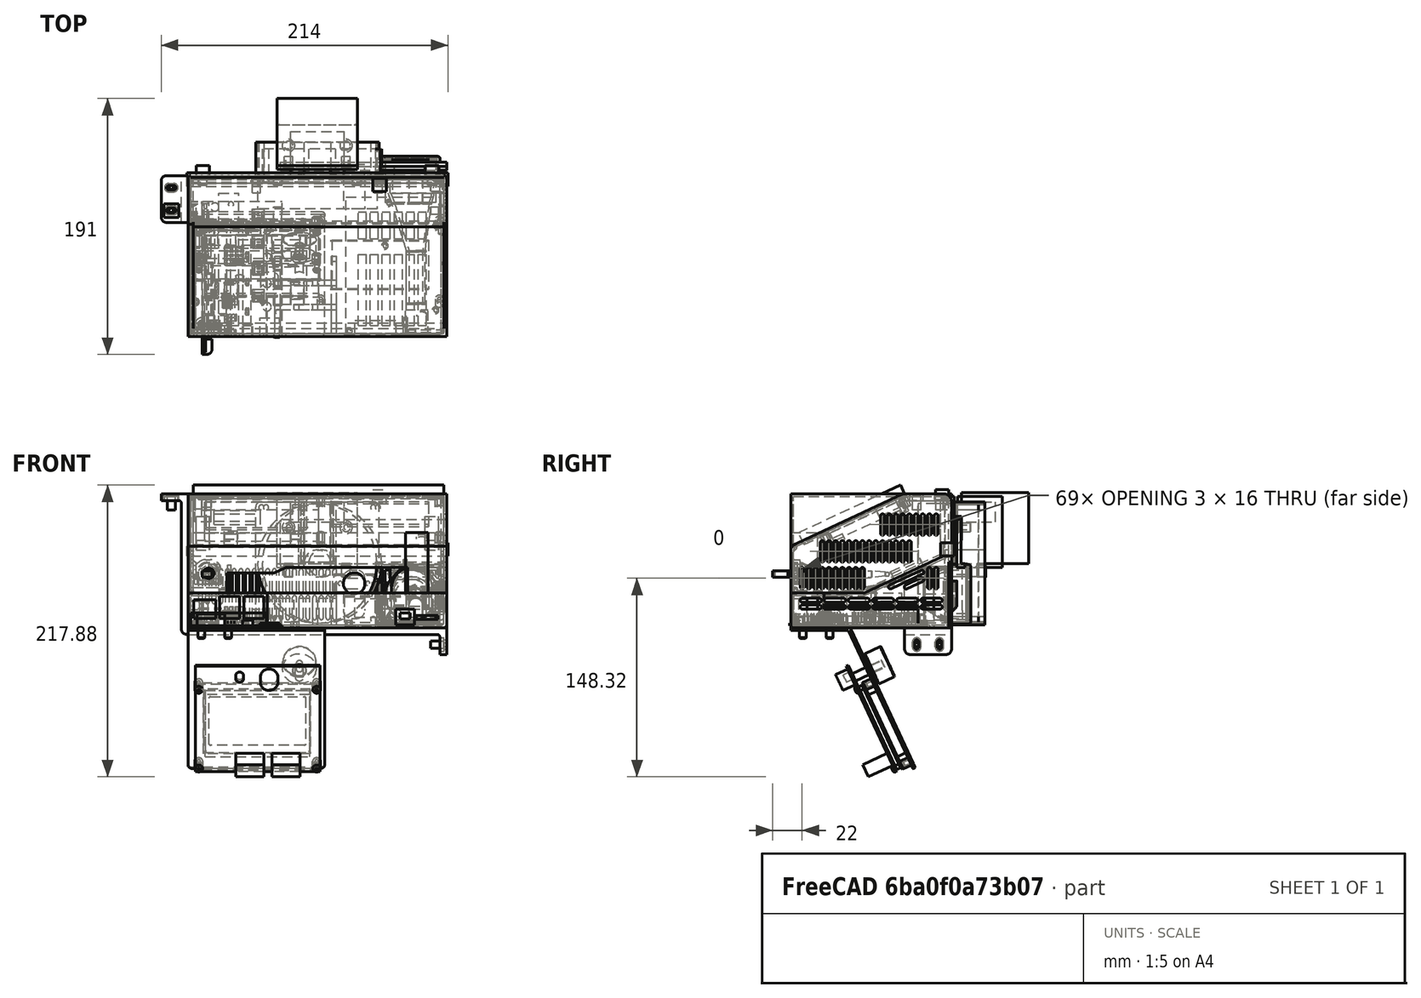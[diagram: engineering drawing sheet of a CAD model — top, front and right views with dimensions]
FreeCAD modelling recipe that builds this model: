
FCSTD DOCUMENT  (FreeCAD 0.19R24291 (Git))
Label: Ender 3 All in One Control Box
License: All rights reserved
LicenseURL: http://en.wikipedia.org/wiki/All_rights_reserved
objects: Part::Box×238, Part::Feature×143, Part::FeaturePython×143, Part::Fillet×105, Part::Cylinder×67, Part::Chamfer×64, Part::MultiFuse×60, Part::Cut×39, App::DocumentObjectGroup×21, Part::Loft×8, App::Part×4, Mesh::Feature×1, Part::Compound×1
note: 868 computed .brp shape members not serialized (recipe doc carries the construction recipe); baked Part::Feature solids carry a one-line shape summary decoded from their .brp

FEATURE [Part::Feature] Raspberry_Pi_3_B__Template001
  Placement = pos=(5.86,26.01,3) rot=(0,0,-1;1.5708rad)
  shape: bbox 58.5 x 89.15 x 20 mm, 4954 faces, 0 solids (baked)
FEATURE [Part::Feature] Part__Feature711  label="M3X8 Pan Head Screw_Standard002"
  Placement = pos=(8.05,48.2452,-46.9667) rot=(0.706961,0.647366,0.284821;3.1725rad)
  shape: bbox 7.142 x 14.51 x 10.14 mm, 23 faces (baked)
FEATURE [Part::Feature] Part__Feature712  label="M3X8 Pan Head Screw_Standard003"
  Placement = pos=(95.95,48.2452,-46.9667) rot=(0.703312,0.680906,0.204256;3.34615rad)
  shape: bbox 6.803 x 14.4 x 9.902 mm, 23 faces (baked)
FEATURE [Part::Feature] Part__Feature706  label="lcd Knob_Standard"
  Placement = pos=(83.1,60.6587,-30.6409) rot=(0.306507,-0.929305,-0.206022;1.25238rad)
  shape: bbox 25 x 22.14 x 27.94 mm, 13 faces (baked)
FEATURE [Part::Feature] Part__Feature707  label="M5X8Pan Head Screw004"
  Placement = pos=(10,9,2.75) rot=(-0.69142,-0.20947,0.69142;3.55456rad)
  shape: bbox 9.985 x 9.723 x 11.27 mm, 24 faces (baked)
FEATURE [Part::Feature] Part__Feature708  label="M5X8Pan Head Screw005"
  Placement = pos=(30,29,2.75) rot=(-0.685865,-0.243264,0.685865;3.61885rad)
  shape: bbox 9.925 x 9.785 x 11.27 mm, 24 faces (baked)
FEATURE [Part::Feature] Part__Feature709  label="M3X8 Pan Head Screw_Standard"
  Placement = pos=(95.95,75.6731,-105.786) rot=(0.698299,0.566548,0.437496;2.83001rad)
  shape: bbox 8.972 x 14.48 x 10.07 mm, 23 faces (baked)
FEATURE [Part::Feature] Part__Feature710  label="M3X8 Pan Head Screw_Standard001"
  Placement = pos=(8.05,75.6731,-105.786) rot=(0.70527,0.608703,0.36342;2.9976rad)
  shape: bbox 8.119 x 14.54 x 10.2 mm, 23 faces (baked)
FEATURE [Part::Feature] Part__Feature703  label="LCD support_Standard"
  Placement = pos=(0,0,0) rot=(0.57735,0.57735,0.57735;2.0944rad)
  shape: bbox 102 x 92.88 x 105.4 mm, 47 faces (baked)
FEATURE [Part::Feature] Part__Feature704  label="lcd_Standard"
  Placement = pos=(52,59.8623,-67.9755) rot=(-1,0,0;1.13446rad)
  shape: bbox 93 x 46.13 x 87.2 mm, 33 faces (baked)
FEATURE [Part::Feature] Part__Feature705  label="lcd_Standard001"
  Placement = pos=(52,59.8623,-67.9755) rot=(-1,0,0;1.13446rad)
  shape: bbox 93 x 34.72 x 64.08 mm, 32 faces (baked)
FEATURE [App::Part] lcd_Standard  label="lcd_Standard002"
  Group = -> [Part__Feature704,Part__Feature705]
  Origin = -> Origin078
FEATURE [App::Part] ASM_Display_Standard  label="ASM Display_Standard"
  Group = -> [Part__Feature703,lcd_Standard,Part__Feature706,Part__Feature707,Part__Feature708,Part__Feature709,Part__Feature710,Part__Feature711,Part__Feature712]
  Origin = -> Origin079
  Placement = pos=(125,1,157) rot=(0,0,1;0rad)
FEATURE [App::Part] _1_MAIN_ASM_Ender_3_Pro  label="01 MAIN ASM Ender 3 Pro"
  Group = -> [ASM_Display_Standard]
  Origin = -> Origin084
  Placement = pos=(-33.3,142.528,6.50199) rot=(1,0,0;1.5708rad)
FEATURE [Part::Box] Box005  label="Cube010"
  AttacherType = Attacher::AttachEngine3D
  Height = 9
  Length = 34.5
  Placement = pos=(7,48,0) rot=(0,0,1;0rad)
  Width = 6
FEATURE [Part::Box] Box004  label="Cube009"
  AttacherType = Attacher::AttachEngine3D
  Height = 6.5
  Length = 85
  Placement = pos=(0,0,9) rot=(0,0,1;0rad)
  Width = 55
FEATURE [Part::MultiFuse] Fusion001  label="Touchscreen"
  Placement = pos=(12.6,36,56.64) rot=(1,0,0;0.436332rad)
  Shapes = -> [Box004,Box005]
FEATURE [Part::Feature] Face034  label="Face005"
  Placement = pos=(0,55,26) rot=(1,0,0;0.436332rad)
  shape: bbox 210 x 125.1 x 58.32 mm, 1 faces, 0 solids (baked)
FEATURE [Part::Feature] Face033  label="Face004"
  Placement = pos=(0,-24,26) rot=(0,0,1;0rad)
  shape: bbox 210 x 138 x 2e-07 mm, 1 faces, 0 solids (baked)
FEATURE [Part::Feature] Face027  label="Face"
  Placement = pos=(5,-23,48.27) rot=(-1,0,0;1.13446rad)
  shape: bbox 216.4 x 183.1 x 85.37 mm, 1 faces, 0 solids (baked)
FEATURE [Part::Feature] Face032  label="Face003"
  Placement = pos=(0,-24,26) rot=(0,0,1;0rad)
  shape: bbox 210 x 2e-07 x 95 mm, 1 faces, 0 solids (baked)
FEATURE [Part::Box] Box  label="Cube"
  AttacherType = Attacher::AttachEngine3D
  Height = 100
  Length = 193
  Width = 120
FEATURE [Part::Cylinder] Cylinder
  Angle = 360
  AttacherType = Attacher::AttachEngine3D
  Height = 9.2
  Radius = 3
FEATURE [Part::Cylinder] Cylinder001
  Angle = 360
  AttacherType = Attacher::AttachEngine3D
  Height = 9.2
  Radius = 1.35
FEATURE [Part::Cut] Cut
  Base = -> Cylinder
  Placement = pos=(99.8,78.1,115.82) rot=(0,0,1;0rad)
  Tool = -> Cylinder001
FEATURE [Part::Feature] Cut001002005
  Placement = pos=(185.75,20.5,0) rot=(0,0,1;0rad)
  shape: bbox 5 x 5 x 4.2 mm, 4 faces (baked)
FEATURE [Part::Feature] Cut001002006
  Placement = pos=(185.75,82.85,0) rot=(0,0,1;0rad)
  shape: bbox 5 x 5 x 4.2 mm, 4 faces (baked)
FEATURE [Part::Feature] Cut001002007
  Placement = pos=(147.9,68.58,0) rot=(0,0,1;0rad)
  shape: bbox 5 x 5 x 4.2 mm, 4 faces (baked)
FEATURE [Part::Feature] Cut001002008
  Placement = pos=(150.5,100.5,0) rot=(0,0,1;0rad)
  shape: bbox 5 x 5 x 4.2 mm, 4 faces (baked)
FEATURE [Part::Cylinder] Cylinder015
  Angle = 360
  AttacherType = Attacher::AttachEngine3D
  Height = 4.2
  Radius = 2.5
FEATURE [Part::Feature] Cut001002004
  Placement = pos=(121.1,4.85,0) rot=(0,0,1;0rad)
  shape: bbox 5 x 5 x 4.2 mm, 4 faces (baked)
FEATURE [Part::Cylinder] Cylinder014
  Angle = 360
  AttacherType = Attacher::AttachEngine3D
  Height = 4.2
  Radius = 1.3
FEATURE [Part::Cut] Cut001002  label="Cut001003"
  Base = -> Cylinder015
  Placement = pos=(6,25.73,0) rot=(0,0,1;0rad)
  Tool = -> Cylinder014
FEATURE [Part::MultiFuse] Fusion002  label="SKR Mini E3 Screw Holes"
  Placement = pos=(-1,-1,1) rot=(0,0,1;0rad)
  Shapes = -> [Cut001002005,Cut001002006,Cut001002007,Cut001002008,Cut001002004]
FEATURE [Part::Cylinder] Cylinder018
  Angle = 360
  AttacherType = Attacher::AttachEngine3D
  Height = 3
  Placement = pos=(150.25,131.4,8) rot=(-1,0,0;1.5708rad)
  Radius = 1.3
FEATURE [Part::Cylinder] Cylinder019
  Angle = 360
  AttacherType = Attacher::AttachEngine3D
  Height = 3
  Placement = pos=(181.75,131.4,9) rot=(-1,0,0;1.5708rad)
  Radius = 1.3
FEATURE [Part::Cylinder] Cylinder020
  Angle = 360
  AttacherType = Attacher::AttachEngine3D
  Height = 3
  Placement = pos=(181.75,131.4,40.5) rot=(-1,0,0;1.5708rad)
  Radius = 1.3
FEATURE [Part::Cylinder] Cylinder021
  Angle = 360
  AttacherType = Attacher::AttachEngine3D
  Height = 3
  Placement = pos=(150.25,131.4,40.5) rot=(-1,0,0;1.5708rad)
  Radius = 1.3
FEATURE [Part::MultiFuse] Fusion004008003  label="Fan Screw Holes"
  Placement = pos=(0.2,0,-0.2) rot=(0,0,1;0rad)
  Shapes = -> [Cylinder018,Cylinder019,Cylinder020,Cylinder021]
FEATURE [Part::Cylinder] Cylinder017  label="Fan Hole"
  Angle = 360
  AttacherType = Attacher::AttachEngine3D
  Height = 25
  Placement = pos=(96.5,120,48) rot=(1,0,0;1.5708rad)
  Radius = 44.5
FEATURE [Part::Box] Box014  label="USB 1"
  AttacherType = Attacher::AttachEngine3D
  Height = 16.7
  Length = 15
  Placement = pos=(23.6,-2,6.788) rot=(0,0,1;0rad)
  Width = 10
FEATURE [Part::Box] Box015  label="USB 2"
  AttacherType = Attacher::AttachEngine3D
  Height = 16.7
  Length = 15
  Placement = pos=(41.7,-2,6.788) rot=(0,0,1;0rad)
  Width = 10
FEATURE [Part::Cylinder] Cylinder010  label="Cable Bundle Hole"
  Angle = 360
  AttacherType = Attacher::AttachEngine3D
  Height = 25
  Placement = pos=(124,120,33) rot=(1,0,0;1.5708rad)
  Radius = 8
FEATURE [Part::Box] Box010  label="MicroSD Slot"
  AttacherType = Attacher::AttachEngine3D
  Height = 2.8
  Length = 16.06
  Placement = pos=(170.4,-2,6.4) rot=(0,0,1;0rad)
  Width = 10
FEATURE [Part::Box] Box011  label="Cube016"
  AttacherType = Attacher::AttachEngine3D
  Height = 4
  Length = 10
  Placement = pos=(-2,72.75,4.94) rot=(0,0,1;0rad)
  Width = 8
FEATURE [Part::Box] Box012  label="Cube017"
  AttacherType = Attacher::AttachEngine3D
  Height = 6
  Length = 10
  Placement = pos=(-2,47.5,6) rot=(0,0,1;0rad)
  Width = 16
FEATURE [Part::Chamfer] Chamfer005  label="HDMI Port"
  Base = -> Box012
  Edges = 2 edges r=2: [Edge9,Edge11]
  Placement = pos=(0,0,1) rot=(0,0,1;0rad)
FEATURE [Part::Cylinder] Cylinder005  label="Headphone Jack"
  Angle = 360
  AttacherType = Attacher::AttachEngine3D
  Height = 10
  Placement = pos=(-1,33.75,9.498) rot=(0,1,0;1.5708rad)
  Radius = 3.75
FEATURE [Part::Box] Box013  label="Ethernet"
  AttacherType = Attacher::AttachEngine3D
  Height = 14
  Length = 16.4
  Placement = pos=(4.3,-2,6.998) rot=(0,0,1;0rad)
  Width = 10
FEATURE [Part::Box] Box007  label="Cube012"
  AttacherType = Attacher::AttachEngine3D
  Height = 6.5
  Length = 74.75
  Placement = pos=(0,-0.5,9) rot=(0,0,1;0rad)
  Width = 50
FEATURE [Part::Box] Box008  label="Cube013"
  AttacherType = Attacher::AttachEngine3D
  Height = 9
  Length = 34.5
  Placement = pos=(7.5,48,0) rot=(0,0,1;0rad)
  Width = 6
FEATURE [Part::MultiFuse] Fusion004008002002  label="Touchscreen Hole"
  Placement = pos=(13.5,36,62.7) rot=(1,0,0;0.436332rad)
  Shapes = -> [Box007,Box008]
FEATURE [Part::Box] Box009  label="Cube248"
  AttacherType = Attacher::AttachEngine3D
  Height = 20
  Length = 71
  Placement = pos=(117,1,4) rot=(0,0,1;0rad)
  Width = 1
FEATURE [Part::Box] Box029  label="Cube034"
  AttacherType = Attacher::AttachEngine3D
  Height = 16
  Length = 2
  Placement = pos=(0,12,29) rot=(0,0,1;0rad)
  Width = 3
FEATURE [Part::Fillet] Fillet005011
  Base = -> Box029
  Edges = 4 edges r=1.49: [Edge9,Edge10,Edge11,Edge12]
FEATURE [Part::Cylinder] Cylinder016
  Angle = 360
  AttacherType = Attacher::AttachEngine3D
  Height = 25
  Placement = pos=(100,140,48) rot=(1,0,0;1.5708rad)
  Radius = 44.5
FEATURE [Part::Box] Box002  label="Cube007"
  AttacherType = Attacher::AttachEngine3D
  Height = 92
  Length = 92
  Placement = pos=(54,115,2) rot=(0,0,1;0rad)
  Width = 25
FEATURE [Part::Fillet] Fillet
  Base = -> Box002
  Edges = 4 edges r=4: [Edge2,Edge4,Edge6,Edge8]
FEATURE [Part::Cylinder] Cylinder022
  Angle = 360
  AttacherType = Attacher::AttachEngine3D
  Height = 25
  Placement = pos=(58.25,140,6.25) rot=(1,0,0;1.5708rad)
  Radius = 2
FEATURE [Part::Cylinder] Cylinder023
  Angle = 360
  AttacherType = Attacher::AttachEngine3D
  Height = 25
  Placement = pos=(141.75,140,6.25) rot=(1,0,0;1.5708rad)
  Radius = 2
FEATURE [Part::Cylinder] Cylinder002
  Angle = 360
  AttacherType = Attacher::AttachEngine3D
  Height = 25
  Placement = pos=(141.75,140,89.75) rot=(1,0,0;1.5708rad)
  Radius = 2
FEATURE [Part::Cylinder] Cylinder003
  Angle = 360
  AttacherType = Attacher::AttachEngine3D
  Height = 25
  Placement = pos=(58.25,140,89.75) rot=(1,0,0;1.5708rad)
  Radius = 2
FEATURE [Part::Cylinder] Cylinder004
  Angle = 360
  AttacherType = Attacher::AttachEngine3D
  Height = 25
  Placement = pos=(100,140,48) rot=(1,0,0;1.5708rad)
  Radius = 10
FEATURE [Part::FeaturePython] Slice  # WARN: FeaturePython — macro-defined, semantics opaque (R4)
  Base = -> Fillet
  Mode = 1
  Tolerance = 0
  Tools = -> [Cylinder016,Cylinder022,Cylinder023,Cylinder002,Cylinder003,Cylinder004]
FEATURE [Part::FeaturePython] Slice_child6  label="Slice.6"  # WARN: FeaturePython — macro-defined, semantics opaque (R4)
  Base = -> Slice
  FilterType = 1
  Invert = false
  OverrideMaxVal = 0
  WindowFrom = 80
  WindowTo = 100
  items = 6
FEATURE [Part::FeaturePython] Slice_child0  label="Slice.0"  # WARN: FeaturePython — macro-defined, semantics opaque (R4)
  Base = -> Slice
  FilterType = 1
  Invert = false
  OverrideMaxVal = 0
  WindowFrom = 80
  WindowTo = 100
  items = 0
FEATURE [Part::MultiFuse] Fusion004008002002002001007002  label="92mm Fan"
  Placement = pos=(-3.5,5,0) rot=(0,0,1;0rad)
  Shapes = -> [Slice_child6,Slice_child0]
FEATURE [Part::Chamfer] Chamfer  label="Micro USB Port"
  Base = -> Box011
  Edges = 2 edges r=1: [Edge9,Edge11]
  Placement = pos=(0,0,1) rot=(0,0,1;0rad)
FEATURE [Part::Box] Box030  label="Cube035"
  AttacherType = Attacher::AttachEngine3D
  Height = 96
  Length = 189
  Placement = pos=(2,2,2) rot=(0,0,1;0rad)
  Width = 116
FEATURE [Part::Feature] Face081
  Placement = pos=(5,-23,50.27) rot=(-1,0,0;1.13446rad)
  shape: bbox 216.4 x 183.1 x 85.37 mm, 1 faces, 0 solids (baked)
FEATURE [Part::Box] Box068  label="Cube073"
  AttacherType = Attacher::AttachEngine3D
  Height = 12.2
  Length = 10
  Placement = pos=(6,-5,0) rot=(0,0,1;0rad)
  Width = 14
FEATURE [Part::Box] Box067  label="Cube072"
  AttacherType = Attacher::AttachEngine3D
  Height = 9.3
  Length = 86
  Placement = pos=(0,0,4.5) rot=(0,0,1;0rad)
  Width = 56
FEATURE [Part::Cut] Cut001002016
  Base = -> Box068
  Placement = pos=(10,0.25,1) rot=(0,0,1;0rad)
  Tool = -> Box067
FEATURE [Part::Box] Box073  label="Ender LCD Hole"
  AttacherType = Attacher::AttachEngine3D
  Height = 10
  Length = 72
  Placement = pos=(107.5,38.85,68.9) rot=(1,0,0;0.436332rad)
  Width = 40
FEATURE [Part::Cylinder] Cylinder024  label="LCD Control Knob Hole"
  Angle = 360
  AttacherType = Attacher::AttachEngine3D
  Height = 10
  Placement = pos=(174.5,17.75,61.25) rot=(1,0,0;0.436332rad)
  Radius = 4
FEATURE [Part::Box] Box074  label="Cube078"
  AttacherType = Attacher::AttachEngine3D
  Height = 4
  Length = 2
  Placement = pos=(2,4,24) rot=(0,0,1;0rad)
  Width = 51
FEATURE [Part::Box] Box075  label="Cube079"
  AttacherType = Attacher::AttachEngine3D
  Height = 4
  Length = 2
  Placement = pos=(189,4,24) rot=(0,0,1;0rad)
  Width = 51
FEATURE [Part::Box] Box076  label="Cube080"
  AttacherType = Attacher::AttachEngine3D
  Height = 4
  Length = 2
  Placement = pos=(2,55,24) rot=(1,0,0;0.436332rad)
  Width = 67.25
FEATURE [Part::Box] Box077  label="Cube081"
  AttacherType = Attacher::AttachEngine3D
  Height = 4
  Length = 2
  Placement = pos=(189,55,24) rot=(1,0,0;0.436332rad)
  Width = 67.25
FEATURE [Part::Box] Box078  label="Cube082"
  AttacherType = Attacher::AttachEngine3D
  Height = 43.5
  Length = 2
  Placement = pos=(2,112,52.5) rot=(0,0,1;0rad)
  Width = 6
FEATURE [Part::Box] Box079  label="Cube083"
  AttacherType = Attacher::AttachEngine3D
  Height = 43.5
  Length = 2
  Placement = pos=(189,112,52.5) rot=(0,0,1;0rad)
  Width = 6
FEATURE [Part::Box] Box081  label="Cube085"
  AttacherType = Attacher::AttachEngine3D
  Height = 6
  Length = 28.75
  Placement = pos=(162.25,2,24) rot=(0,0,1;0rad)
  Width = 3
FEATURE [Part::Fillet] Fillet005011013
  Base = -> Box081
  Edges = 1 edges r=1.999: [Edge5]
FEATURE [Part::Chamfer] Chamfer006
  Base = -> Box075
  Edges = 1 edges r=1.99: [Edge4]
FEATURE [Part::Chamfer] Chamfer007
  Base = -> Box077
  Edges = 1 edges r=1.99: [Edge4]
FEATURE [Part::Chamfer] Chamfer008
  Base = -> Box074
  Edges = 1 edges r=1.99: [Edge8]
FEATURE [Part::Chamfer] Chamfer009
  Base = -> Box076
  Edges = 1 edges r=1.99: [Edge8]
FEATURE [Part::Box] Box083  label="Cube087"
  AttacherType = Attacher::AttachEngine3D
  Height = 14
  Length = 31
  Placement = pos=(124.5,2,7.8) rot=(0,0,1;0rad)
  Width = 10
FEATURE [Part::Box] Box085004  label="Screen Slicin' Cube"
  AttacherType = Attacher::AttachEngine3D
  Height = 10
  Length = 187
  Placement = pos=(4,10,62) rot=(1,0,0;0.436332rad)
  Width = 84
FEATURE [Part::Cylinder] Cylinder025
  Angle = 360
  AttacherType = Attacher::AttachEngine3D
  Height = 72.5
  Radius = 2.4
FEATURE [Part::Chamfer] Chamfer011002
  Base = -> Cylinder025
  Edges = 1 edges: [Edge1 r1=10 r2=1]
FEATURE [Part::Cylinder] Cylinder026
  Angle = 360
  AttacherType = Attacher::AttachEngine3D
  Height = 3
  Placement = pos=(0,0,72.5) rot=(0,0,1;0rad)
  Radius = 1.4
FEATURE [Part::Fillet] Fillet005011017004
  Base = -> Cylinder026
  Edges = 1 edges r=1: [Edge1]
FEATURE [Part::Box] Box085008  label="Cube096"
  AttacherType = Attacher::AttachEngine3D
  Height = 11.5
  Length = 7.4
  Placement = pos=(-2.4,-2.4,-11.5) rot=(0,0,1;0rad)
  Width = 4.8
FEATURE [Part::Fillet] Fillet005011017005
  Base = -> Box085008
  Edges = 2 edges r=1: [Edge1,Edge3]
FEATURE [Part::Fillet] Fillet005011017006
  Base = -> Fillet005011017005
  Edges = 1 edges r=4: [Edge15]
FEATURE [Part::Box] Box085009  label="Cube097"
  AttacherType = Attacher::AttachEngine3D
  Height = 10
  Length = 1
  Placement = pos=(-1,-2.4,-10) rot=(0,0,1;0rad)
  Width = 4.8
FEATURE [Part::Cut] Cut001002016002
  Base = -> Fillet005011017006
  Tool = -> Box085009
FEATURE [Part::MultiFuse] Fusion004008002002002001007002002008  label="Stylus"
  Placement = pos=(13,-2,40) rot=(-1,0,0;1.5708rad)
  Shapes = -> [Chamfer011002,Fillet005011017004,Cut001002016002]
FEATURE [Part::Feature] Part__Feature713  label="X_Stepper_Connector001"
  Placement = pos=(64,84.3,1.6) rot=(0,0,1;0rad)
  shape: bbox 5.8 x 12.45 x 7.1 mm, 6 faces (baked)
FEATURE [Part::Feature] Part__Feature714  label="Y_Stepper_Connector001"
  Placement = pos=(64,63.45,1.6) rot=(0,0,1;0rad)
  shape: bbox 5.8 x 12.45 x 7.1 mm, 6 faces (baked)
FEATURE [Part::Feature] Part__Feature715  label="ZA_Stepper_Connector001"
  Placement = pos=(64,50,1.6) rot=(0,0,1;0rad)
  shape: bbox 5.8 x 12.45 x 7.1 mm, 6 faces (baked)
FEATURE [Part::Feature] Part__Feature716  label="ZB_Stepper_Connector001"
  Placement = pos=(64,36.55,1.6) rot=(0,0,1;0rad)
  shape: bbox 5.8 x 12.45 x 7.1 mm, 6 faces (baked)
FEATURE [Part::Feature] Part__Feature717  label="E_Stepper_Connector001"
  Placement = pos=(64,23.1,1.6) rot=(0,0,1;0rad)
  shape: bbox 5.8 x 12.45 x 7.1 mm, 6 faces (baked)
FEATURE [Part::Feature] Part__Feature718  label="Capacitor005"
  shape: bbox 6.711 x 6.711 x 7.9 mm, 4 faces (baked)
FEATURE [Part::Feature] Part__Feature719  label="Capacitor006"
  Placement = pos=(0,17.5,0) rot=(0,0,1;0rad)
  shape: bbox 6.711 x 6.711 x 7.9 mm, 4 faces (baked)
FEATURE [Part::Feature] Part__Feature720  label="Capacitor007"
  Placement = pos=(0,37,0) rot=(0,0,1;0rad)
  shape: bbox 6.711 x 6.711 x 7.9 mm, 4 faces (baked)
FEATURE [Part::Feature] Part__Feature721  label="Capacitor008"
  Placement = pos=(0,57.5,0) rot=(0,0,1;0rad)
  shape: bbox 6.711 x 6.711 x 7.9 mm, 4 faces (baked)
FEATURE [Part::Feature] Part__Feature722  label="Capacitor009"
  Placement = pos=(-39,74.5,0) rot=(0,0,1;0rad)
  shape: bbox 6.711 x 6.711 x 7.9 mm, 4 faces (baked)
FEATURE [Part::Feature] Part__Feature723  label="Board001"
  shape: bbox 70.25 x 100.8 x 1.6 mm, 11 faces (baked)
FEATURE [Part::Feature] Part__Feature724  label="X_Stepper_Driver001"
  Placement = pos=(50,88,1.6) rot=(0,0,1;0rad)
  shape: bbox 5 x 5 x 0.9 mm, 6 faces (baked)
FEATURE [Part::Feature] Part__Feature725  label="Y_Stepper_Driver001"
  Placement = pos=(50,67.5,1.6) rot=(0,0,1;0rad)
  shape: bbox 5 x 5 x 0.9 mm, 6 faces (baked)
FEATURE [Part::Feature] Part__Feature726  label="Z_Stepper_Driver001"
  Placement = pos=(50,47,1.6) rot=(0,0,1;0rad)
  shape: bbox 5 x 5 x 0.9 mm, 6 faces (baked)
FEATURE [Part::Feature] Part__Feature727  label="E_Stepper_Driver001"
  Placement = pos=(50,28,1.6) rot=(0,0,1;0rad)
  shape: bbox 5 x 5 x 0.9 mm, 6 faces (baked)
FEATURE [Part::Feature] Part__Feature728  label="Tall_Terminal003"
  Placement = pos=(-90.35,100.75,0) rot=(0,0,-1;1.5708rad)
  shape: bbox 10.4 x 10.6 x 18.4 mm, 17 faces (baked)
FEATURE [Part::Feature] Part__Feature729  label="Tall_Terminal004"
  Placement = pos=(0,-23.3,0) rot=(0,0,1;0rad)
  shape: bbox 10.6 x 10.4 x 18.4 mm, 17 faces (baked)
FEATURE [Part::Feature] Part__Feature730  label="Tall_Terminal005"
  Placement = pos=(0,-12.6,0) rot=(0,0,1;0rad)
  shape: bbox 10.6 x 10.4 x 18.4 mm, 17 faces (baked)
FEATURE [Part::Feature] Part__Feature731  label="Short_Terminal001"
  Placement = pos=(1.6,0,0) rot=(0,0,1;0rad)
  shape: bbox 7.5 x 9.9 x 10.55 mm, 12 faces (baked)
FEATURE [Part::Feature] Part__Feature732  label="Fan0_Terminal001"
  Placement = pos=(0,47.5,1.6) rot=(0,0,1;0rad)
  shape: bbox 5.8 x 7.5 x 7.2 mm, 6 faces (baked)
FEATURE [Part::Feature] Part__Feature733  label="X-Stop001"
  Placement = pos=(0,39,1.6) rot=(0,0,1;0rad)
  shape: bbox 5.8 x 7.5 x 7.2 mm, 6 faces (baked)
FEATURE [Part::Feature] Part__Feature734  label="Y-Stop001"
  Placement = pos=(0,30.5,1.6) rot=(0,0,1;0rad)
  shape: bbox 5.8 x 7.5 x 7.2 mm, 6 faces (baked)
FEATURE [Part::Feature] Part__Feature735  label="Z-Stop001"
  Placement = pos=(0,22,1.6) rot=(0,0,1;0rad)
  shape: bbox 5.8 x 7.5 x 7.2 mm, 6 faces (baked)
FEATURE [Part::Feature] Part__Feature736  label="THB001"
  Placement = pos=(0,13.5,1.6) rot=(0,0,1;0rad)
  shape: bbox 5.8 x 7.5 x 7.2 mm, 6 faces (baked)
FEATURE [Part::Feature] Part__Feature737  label="TH001"
  Placement = pos=(0,5,1.6) rot=(0,0,1;0rad)
  shape: bbox 5.8 x 7.5 x 7.2 mm, 6 faces (baked)
FEATURE [Part::Feature] Part__Feature738  label="Fan1_Terminal001"
  Placement = pos=(12.55,47.5,1.6) rot=(0,0,1;0rad)
  shape: bbox 5.8 x 7.5 x 7.2 mm, 6 faces (baked)
FEATURE [Part::Feature] Part__Feature739  label="PS-ON001"
  Placement = pos=(12.55,39,1.6) rot=(0,0,1;0rad)
  shape: bbox 5.8 x 7.5 x 7.2 mm, 6 faces (baked)
FEATURE [Part::Feature] Part__Feature740  label="PWR-DET001"
  Placement = pos=(12.55,28,1.6) rot=(0,0,1;0rad)
  shape: bbox 5.8 x 10 x 7.2 mm, 6 faces (baked)
FEATURE [Part::Feature] Part__Feature741  label="E0-STOP001"
  Placement = pos=(12.55,17,1.6) rot=(0,0,1;0rad)
  shape: bbox 5.8 x 10 x 7.2 mm, 6 faces (baked)
FEATURE [Part::Feature] Part__Feature742  label="Neopixel001"
  Placement = pos=(22.85,17,1.6) rot=(0,0,1;0rad)
  shape: bbox 5.8 x 10 x 7.2 mm, 6 faces (baked)
FEATURE [Part::Feature] Part__Feature743  label="Z-Probe001"
  Placement = pos=(12.55,10,1.6) rot=(0,0,1;0rad)
  shape: bbox 15 x 5.75 x 7.2 mm, 6 faces (baked)
FEATURE [Part::Feature] Part__Feature744  label="EXP002"
  Placement = pos=(6.8,0,1.6) rot=(0,0,1;0rad)
  shape: bbox 20.45 x 8.9 x 8.9 mm, 6 faces (baked)
FEATURE [Part::Feature] Part__Feature745  label="CPU001"
  Placement = pos=(28,39.5,1.6) rot=(0,0,1;0rad)
  shape: bbox 10 x 10 x 2 mm, 6 faces (baked)
FEATURE [Part::Feature] Part__Feature746  label="Q004"
  Placement = pos=(12.2,69.15,1.6) rot=(0,0,1;0rad)
  shape: bbox 10 x 10 x 6.4 mm, 6 faces (baked)
FEATURE [Part::Feature] Part__Feature747  label="Q005"
  Placement = pos=(11,59.65,1.6) rot=(0,0,1;0rad)
  shape: bbox 6.2 x 6.2 x 2.4 mm, 6 faces (baked)
FEATURE [Part::Feature] Part__Feature748  label="E_Stepper_Driver_Heatsink001"
  Placement = pos=(48,26,0) rot=(0,0,1;0rad)
  shape: bbox 9 x 9.15 x 12.17 mm, 94 faces (baked)
FEATURE [Part::Feature] Part__Feature749  label="Z_Stepper_Driver_Heatsink002"
  Placement = pos=(48,46,0) rot=(0,0,1;0rad)
  shape: bbox 9 x 9.15 x 12.17 mm, 94 faces (baked)
FEATURE [Part::Feature] Part__Feature750  label="Y_Stepper_Driver_Heatsink003"
  Placement = pos=(48,66,0) rot=(0,0,1;0rad)
  shape: bbox 9 x 9.15 x 12.17 mm, 94 faces (baked)
FEATURE [Part::Feature] Part__Feature751  label="X_Stepper_Driver_Heatsink004"
  Placement = pos=(48,86,0) rot=(0,0,1;0rad)
  shape: bbox 9 x 9.15 x 12.17 mm, 94 faces (baked)
FEATURE [Part::Feature] Part__Feature752  label="SPI002"
  Placement = pos=(0.6,0,0) rot=(0,0,1;0rad)
  shape: bbox 7.5 x 5 x 8.9 mm, 64 faces (baked)
FEATURE [Part::Feature] Part__Feature753  label="E0-DIAG001"
  Placement = pos=(43,16,0) rot=(0,0,1;0rad)
  shape: bbox 2.5 x 5 x 8.9 mm, 24 faces (baked)
FEATURE [Part::Feature] Part__Feature754  label="Z-DIAG001"
  Placement = pos=(43,38,0) rot=(0,0,1;0rad)
  shape: bbox 2.5 x 5 x 8.9 mm, 24 faces (baked)
FEATURE [Part::Feature] Part__Feature755  label="Y-DIAG001"
  Placement = pos=(43,58,0) rot=(0,0,1;0rad)
  shape: bbox 2.5 x 5 x 8.9 mm, 24 faces (baked)
FEATURE [Part::Feature] Part__Feature756  label="X-DIAG001"
  Placement = pos=(43,77,0) rot=(0,0,1;0rad)
  shape: bbox 2.5 x 5 x 8.9 mm, 24 faces (baked)
FEATURE [Part::Feature] Part__Feature757  label="SWD001"
  shape: bbox 12.5 x 2.5 x 8.9 mm, 57 faces (baked)
FEATURE [Part::Feature] Part__Feature758  label="TFT001"
  Placement = pos=(78,-5,0) rot=(0,0,1;1.5708rad)
  shape: bbox 2.5 x 12.5 x 8.9 mm, 57 faces (baked)
FEATURE [Part::Feature] Part__Feature759  label="GND-VOUT001"
  shape: bbox 7.5 x 7.5 x 8.9 mm, 75 faces (baked)
FEATURE [Part::Feature] Part__Feature760  label="VIN001"
  Placement = pos=(17,81.02,0) rot=(0,0,1;0rad)
  shape: bbox 5 x 5 x 8.9 mm, 44 faces (baked)
FEATURE [Part::Feature] Part__Feature761  label="Fuse001"
  shape: bbox 4.55 x 14.85 x 17.8 mm, 22 faces (baked)
FEATURE [Part::Feature] Part__Feature762  label="Mini-USB_Port001"
  shape: bbox 7.5 x 9.2 x 4.05 mm, 8 faces (baked)
FEATURE [Part::Feature] Part__Feature763  label="Micro-SD_Card_Reader001"
  shape: bbox 14.7 x 14.5 x 1.93 mm, 8 faces (baked)
FEATURE [App::Part] SKR_Mini_E3_v2_0_Dummy001  label="SKR_Mini_E3_v2_0_Dummy"
  Group = -> [Part__Feature713,Part__Feature714,Part__Feature715,Part__Feature716,Part__Feature717,Part__Feature718,Part__Feature719,Part__Feature720,Part__Feature721,Part__Feature722,Part__Feature723,Part__Feature724,Part__Feature725,Part__Feature726,Part__Feature727,Part__Feature728,Part__Feature729,Part__Feature730,Part__Feature731,Part__Feature732,Part__Feature733,Part__Feature734,Part__Feature735,+28 more]
  Origin = -> Origin085
  Placement = pos=(117.5,1,5.2) rot=(0,0,1;0rad)
FEATURE [Part::FeaturePython] Slice001  # WARN: FeaturePython — macro-defined, semantics opaque (R4)
  Base = -> Box030
  Mode = 1
  Tolerance = 0
  Tools = -> [Face027]
FEATURE [Part::FeaturePython] Slice001_child0  label="Slice001.0"  # WARN: FeaturePython — macro-defined, semantics opaque (R4)
  Base = -> Slice001
  FilterType = 1
  Invert = false
  OverrideMaxVal = 0
  WindowFrom = 80
  WindowTo = 100
  items = 0
FEATURE [Part::FeaturePython] Slice001_child1  label="Slice001.1"  # WARN: FeaturePython — macro-defined, semantics opaque (R4)
  Base = -> Slice001
  FilterType = 1
  Invert = false
  OverrideMaxVal = 0
  WindowFrom = 80
  WindowTo = 100
  items = 1
FEATURE [App::DocumentObjectGroup] GrExplode_Slice001  label="Exploded Slice001"
  Group = -> [Slice001_child0,Slice001_child1]
FEATURE [Part::Box] Box085012  label="Cube100"
  AttacherType = Attacher::AttachEngine3D
  Height = 9.3
  Length = 86
  Placement = pos=(0,0,4.5) rot=(0,0,1;0rad)
  Width = 56
FEATURE [Part::Box] Box085013  label="Cube101"
  AttacherType = Attacher::AttachEngine3D
  Height = 12.2
  Length = 20
  Placement = pos=(70,49,0) rot=(0,0,1;0rad)
  Width = 12
FEATURE [Part::Cut] Cut001002016004
  Base = -> Box085013
  Placement = pos=(55.25,-30.25,1) rot=(0,0,1;1.5708rad)
  Tool = -> Box085012
FEATURE [Part::Cylinder] Cylinder027
  Angle = 360
  AttacherType = Attacher::AttachEngine3D
  Height = 9.2
  Radius = 3
FEATURE [Part::Cylinder] Cylinder028
  Angle = 360
  AttacherType = Attacher::AttachEngine3D
  Height = 9.2
  Radius = 1.35
FEATURE [Part::Cut] Cut001002016005
  Base = -> Cylinder027
  Placement = pos=(188.15,78.1,115.82) rot=(0,0,1;0rad)
  Tool = -> Cylinder028
FEATURE [Part::Cylinder] Cylinder029
  Angle = 360
  AttacherType = Attacher::AttachEngine3D
  Height = 8.2
  Radius = 3
FEATURE [Part::Cylinder] Cylinder030
  Angle = 360
  AttacherType = Attacher::AttachEngine3D
  Height = 9.2
  Radius = 1.35
FEATURE [Part::Cut] Cut001002016006
  Base = -> Cylinder029
  Placement = pos=(188.15,143.2,115.82) rot=(0,0,1;0rad)
  Tool = -> Cylinder030
FEATURE [Part::Cylinder] Cylinder031
  Angle = 360
  AttacherType = Attacher::AttachEngine3D
  Height = 9.2
  Radius = 1.35
FEATURE [Part::Cylinder] Cylinder032
  Angle = 360
  AttacherType = Attacher::AttachEngine3D
  Height = 9.2
  Radius = 3
FEATURE [Part::Cut] Cut001002016007
  Base = -> Cylinder032
  Placement = pos=(99.8,143.2,115.82) rot=(0,0,1;0rad)
  Tool = -> Cylinder031
FEATURE [Part::MultiFuse] Fusion  label="Ender LED Screw Holes"
  Placement = pos=(-0.65,6.1,-75.25) rot=(1,0,0;0.436332rad)
  Shapes = -> [Cut,Cut001002016005,Cut001002016006,Cut001002016007]
FEATURE [Part::FeaturePython] Slice002  # WARN: FeaturePython — macro-defined, semantics opaque (R4)
  Base = -> Box
  Mode = 1
  Tolerance = 0
  Tools = -> [Face081]
FEATURE [Part::FeaturePython] Slice002_child0  label="Slice002.0"  # WARN: FeaturePython — macro-defined, semantics opaque (R4)
  Base = -> Slice002
  FilterType = 1
  Invert = false
  OverrideMaxVal = 0
  WindowFrom = 80
  WindowTo = 100
  items = 0
FEATURE [Part::FeaturePython] Slice002_child1  label="Slice002.1"  # WARN: FeaturePython — macro-defined, semantics opaque (R4)
  Base = -> Slice002
  FilterType = 1
  Invert = false
  OverrideMaxVal = 0
  WindowFrom = 80
  WindowTo = 100
  items = 1
FEATURE [App::DocumentObjectGroup] GrExplode_Slice002  label="Exploded Slice002"
  Group = -> [Slice002_child0,Slice002_child1]
FEATURE [Part::Chamfer] Chamfer011003
  Base = -> Slice001_child0
  Edges = 1 edges r=6: [Edge11]
FEATURE [Part::Fillet] Fillet005011017009
  Base = -> Chamfer011003
  Edges = 16 edges r=2: [Edge1,Edge2,Edge3,Edge4,Edge5,Edge6,Edge8,Edge9,Edge10,Edge11,Edge13,Edge14,Edge15,Edge16,Edge17,Edge18]
FEATURE [Part::Fillet] Fillet005011017010
  Base = -> Fillet005011017009
  Edges = 1 edges r=4: [Edge28]
FEATURE [Part::Fillet] Fillet005011017011
  Base = -> Fillet005011017010
  Edges = 1 edges r=8: [Edge5]
FEATURE [Part::Fillet] Fillet005011017012
  Base = -> Slice002_child0
  Edges = 2 edges r=6: [Edge7,Edge11]
FEATURE [Part::Fillet] Fillet005011017013
  Base = -> Fillet005011017012
  Edges = 1 edges r=8: [Edge16]
FEATURE [Part::Fillet] Fillet005011017014
  Base = -> Fillet005011017013
  Edges = 18 edges r=2: [Edge1,Edge2,Edge3,Edge4,Edge5,Edge6,Edge7,Edge8,Edge10,Edge12,Edge15,Edge16,Edge18,Edge19,Edge20,Edge22,Edge23,Edge24]
FEATURE [Part::Cut] Cut001002016008
  Base = -> Fillet005011017014
  Tool = -> Fillet005011017011
FEATURE [Part::Box] Box085014  label="Cube102"
  AttacherType = Attacher::AttachEngine3D
  Height = 6.2
  Length = 2.4
  Placement = pos=(47.9,107.2,98.2) rot=(0,1,0;1.5708rad)
  Width = 10.2
FEATURE [Part::Box] Box085015  label="Cube103"
  AttacherType = Attacher::AttachEngine3D
  Height = 6
  Length = 2
  Placement = pos=(1,95,38) rot=(0,0,1;0rad)
  Width = 5
FEATURE [Part::Chamfer] Chamfer011004
  Base = -> Box085015
  Edges = 2 edges: [Edge11 r1=0.5 r2=2.75,Edge12 r1=0.5 r2=2.75]
  Placement = pos=(10,17.2,99.001) rot=(0,1,0;1.5708rad)
FEATURE [Part::Box] Box085016  label="Cube104"
  AttacherType = Attacher::AttachEngine3D
  Height = 6
  Length = 2
  Placement = pos=(1,95,38) rot=(0,0,1;0rad)
  Width = 5
FEATURE [Part::Chamfer] Chamfer011005
  Base = -> Box085016
  Edges = 2 edges: [Edge11 r1=0.5 r2=2.75,Edge12 r1=0.5 r2=2.75]
  Placement = pos=(101,17.2,99.001) rot=(0,1,0;1.5708rad)
FEATURE [Part::Box] Box085017  label="Cube105"
  AttacherType = Attacher::AttachEngine3D
  Height = 6.23
  Length = 2.4
  Placement = pos=(138.9,107.2,98.2) rot=(0,1,0;1.5708rad)
  Width = 10.2
FEATURE [Part::Box] Box085023  label="Cube110"
  AttacherType = Attacher::AttachEngine3D
  Height = 1.7
  Length = 14.1
  Placement = pos=(27.4,53.2155,9.6005) rot=(0,0,1;0rad)
  Width = 14.1
FEATURE [Part::Box] Box085024  label="Cube111"
  AttacherType = Attacher::AttachEngine3D
  Height = 5.55
  Length = 2.3
  Placement = pos=(27.4,53.2155,11.3) rot=(0,0,1;0rad)
  Width = 1.55
FEATURE [Part::Chamfer] Chamfer011006
  Base = -> Box085024
  Edges = 2 edges: [Edge10 r1=5.5 r2=0.5,Edge12 r1=5.5 r2=0.5]
FEATURE [Part::Feature] Chamfer011006001
  Placement = pos=(3.93,0,0) rot=(0,0,1;0rad)
  shape: bbox 2.3 x 1.55 x 5.55 mm, 8 faces (baked)
FEATURE [Part::Feature] Chamfer011006002
  Placement = pos=(7.86,0,0) rot=(0,0,1;0rad)
  shape: bbox 2.3 x 1.55 x 5.55 mm, 8 faces (baked)
FEATURE [Part::Feature] Chamfer011006003
  Placement = pos=(11.8,0,0) rot=(0,0,1;0rad)
  shape: bbox 2.3 x 1.55 x 5.55 mm, 8 faces (baked)
FEATURE [Part::Feature] Chamfer011006004
  Placement = pos=(0,3.14,0) rot=(0,0,1;0rad)
  shape: bbox 2.3 x 1.55 x 5.55 mm, 8 faces (baked)
FEATURE [Part::Feature] Chamfer011006001001
  Placement = pos=(3.93,3.14,0) rot=(0,0,1;0rad)
  shape: bbox 2.3 x 1.55 x 5.55 mm, 8 faces (baked)
FEATURE [Part::Feature] Chamfer011006002001
  Placement = pos=(7.86,3.14,0) rot=(0,0,1;0rad)
  shape: bbox 2.3 x 1.55 x 5.55 mm, 8 faces (baked)
FEATURE [Part::Feature] Chamfer011006003001
  Placement = pos=(11.8,3.14,0) rot=(0,0,1;0rad)
  shape: bbox 2.3 x 1.55 x 5.55 mm, 8 faces (baked)
FEATURE [Part::Feature] Chamfer011006003002
  Placement = pos=(11.8,6.28,0) rot=(0,0,1;0rad)
  shape: bbox 2.3 x 1.55 x 5.55 mm, 8 faces (baked)
FEATURE [Part::Feature] Chamfer011006003003
  Placement = pos=(7.86,6.28,0) rot=(0,0,1;0rad)
  shape: bbox 2.3 x 1.55 x 5.55 mm, 8 faces (baked)
FEATURE [Part::Feature] Chamfer011006003004
  Placement = pos=(3.93,6.28,0) rot=(0,0,1;0rad)
  shape: bbox 2.3 x 1.55 x 5.55 mm, 8 faces (baked)
FEATURE [Part::Feature] Chamfer011006003005
  Placement = pos=(0,6.28,0) rot=(0,0,1;0rad)
  shape: bbox 2.3 x 1.55 x 5.55 mm, 8 faces (baked)
FEATURE [Part::Feature] Chamfer011006003006
  Placement = pos=(11.8,9.42,0) rot=(0,0,1;0rad)
  shape: bbox 2.3 x 1.55 x 5.55 mm, 8 faces (baked)
FEATURE [Part::Feature] Chamfer011006003007
  Placement = pos=(7.86,9.42,0) rot=(0,0,1;0rad)
  shape: bbox 2.3 x 1.55 x 5.55 mm, 8 faces (baked)
FEATURE [Part::Feature] Chamfer011006003008
  Placement = pos=(3.93,9.42,0) rot=(0,0,1;0rad)
  shape: bbox 2.3 x 1.55 x 5.55 mm, 8 faces (baked)
FEATURE [Part::Feature] Chamfer011006003009
  Placement = pos=(0,9.17,0) rot=(0,0,1;0rad)
  shape: bbox 2.3 x 1.55 x 5.55 mm, 8 faces (baked)
FEATURE [Part::Feature] Chamfer011006003010
  Placement = pos=(11.8,12.55,0) rot=(0,0,1;0rad)
  shape: bbox 2.3 x 1.55 x 5.55 mm, 8 faces (baked)
FEATURE [Part::Feature] Chamfer011006003011
  Placement = pos=(7.86,12.55,0) rot=(0,0,1;0rad)
  shape: bbox 2.3 x 1.55 x 5.55 mm, 8 faces (baked)
FEATURE [Part::Feature] Chamfer011006003012
  Placement = pos=(3.93,12.55,0) rot=(0,0,1;0rad)
  shape: bbox 2.3 x 1.55 x 5.55 mm, 8 faces (baked)
FEATURE [Part::Feature] Chamfer011006003013
  Placement = pos=(0,12.55,0) rot=(0,0,1;0rad)
  shape: bbox 2.3 x 1.55 x 5.55 mm, 8 faces (baked)
FEATURE [Part::MultiFuse] Fusion004008002002002001007002002013  label="RPi CPU Heatsink"
  Placement = pos=(0,0,-1) rot=(0,0,1;0rad)
  Shapes = -> [Box085023,Chamfer011006,Chamfer011006001,Chamfer011006002,Chamfer011006003,Chamfer011006004,Chamfer011006001001,Chamfer011006002001,Chamfer011006003001,Chamfer011006003002,Chamfer011006003003,Chamfer011006003004,Chamfer011006003005,Chamfer011006003006,Chamfer011006003007,Chamfer011006003008,Chamfer011006003009,Chamfer011006003010,Chamfer011006003011,Chamfer011006003012,Chamfer011006003013]
FEATURE [Part::Box] Box085025  label="Cube112"
  AttacherType = Attacher::AttachEngine3D
  Height = 1.7
  Length = 9
  Placement = pos=(25.897,21.115,8.3) rot=(0,0,1;0rad)
  Width = 9
FEATURE [Part::Box] Box085026  label="Cube113"
  AttacherType = Attacher::AttachEngine3D
  Height = 3.85
  Length = 9
  Placement = pos=(25.897,21.115,10) rot=(0,0,1;0rad)
  Width = 1
FEATURE [Part::Fillet] Fillet005011017017
  Base = -> Box085026
  Edges = 2 edges r=0.49: [Edge10,Edge12]
FEATURE [Part::Box] Box085027  label="Cube114"
  AttacherType = Attacher::AttachEngine3D
  Height = 3.85
  Length = 9
  Placement = pos=(25.897,21.115,10) rot=(0,0,1;0rad)
  Width = 1
FEATURE [Part::Fillet] Fillet005011017018
  Base = -> Box085027
  Edges = 2 edges r=0.49: [Edge10,Edge12]
  Placement = pos=(0,2,0) rot=(0,0,1;0rad)
FEATURE [Part::Box] Box085028  label="Cube115"
  AttacherType = Attacher::AttachEngine3D
  Height = 3.85
  Length = 9
  Placement = pos=(25.897,21.115,10) rot=(0,0,1;0rad)
  Width = 1
FEATURE [Part::Fillet] Fillet005011017019
  Base = -> Box085028
  Edges = 2 edges r=0.49: [Edge10,Edge12]
  Placement = pos=(0,4,0) rot=(0,0,1;0rad)
FEATURE [Part::Box] Box085029  label="Cube116"
  AttacherType = Attacher::AttachEngine3D
  Height = 3.85
  Length = 9
  Placement = pos=(25.897,21.115,10) rot=(0,0,1;0rad)
  Width = 1
FEATURE [Part::Fillet] Fillet005011017020
  Base = -> Box085029
  Edges = 2 edges r=0.49: [Edge10,Edge12]
  Placement = pos=(0,6,0) rot=(0,0,1;0rad)
FEATURE [Part::Box] Box085030  label="Cube117"
  AttacherType = Attacher::AttachEngine3D
  Height = 3.85
  Length = 9
  Placement = pos=(25.897,21.115,10) rot=(0,0,1;0rad)
  Width = 1
FEATURE [Part::Fillet] Fillet005011017021
  Base = -> Box085030
  Edges = 2 edges r=0.49: [Edge10,Edge12]
  Placement = pos=(0,8,0) rot=(0,0,1;0rad)
FEATURE [Part::MultiFuse] Fusion004008002002002001007002002014  label="Rpi LAN Heatsink"
  Placement = pos=(0,0,-1) rot=(0,0,1;0rad)
  Shapes = -> [Box085025,Fillet005011017017,Fillet005011017018,Fillet005011017019,Fillet005011017020,Fillet005011017021]
FEATURE [App::DocumentObjectGroup] Group007  label="Raspberry Pi"
  Group = -> [Fusion004008002002002001007002002013,Fusion004008002002002001007002002014,Raspberry_Pi_3_B__Template001]
FEATURE [Part::Box] Box085036  label="PiCam Ribbon Cable Slot"
  AttacherType = Attacher::AttachEngine3D
  Height = 1
  Length = 17
  Placement = pos=(8,118,14) rot=(0,0,1;0rad)
  Width = 2
FEATURE [Mesh::Feature] Drawer_Upper  label="Drawer Upper"
FEATURE [Part::Feature] Drawer_Upper001
  Placement = pos=(30.5,0,26) rot=(0,0,1;0rad)
  shape: bbox 134.6 x 72 x 18.75 mm, 540 faces, 0 solids (baked)
FEATURE [Part::Box] Box085041  label="Cube128"
  AttacherType = Attacher::AttachEngine3D
  Height = 12.2
  Length = 10
  Placement = pos=(6,-5,0) rot=(0,0,1;0rad)
  Width = 14
FEATURE [Part::Box] Box085042  label="Cube129"
  AttacherType = Attacher::AttachEngine3D
  Height = 9.3
  Length = 86
  Placement = pos=(0,0,4.5) rot=(0,0,1;0rad)
  Width = 56
FEATURE [Part::Cut] Cut001002016010
  Base = -> Box085041
  Placement = pos=(59.5,0.25,1) rot=(0,0,1;0rad)
  Tool = -> Box085042
FEATURE [Part::Cylinder] Cylinder033
  Angle = 360
  AttacherType = Attacher::AttachEngine3D
  Height = 10
  Placement = pos=(75,-2.5,0) rot=(1,0,0;0rad)
  Radius = 1.35
FEATURE [Part::Box] Box069  label="Cube074"
  AttacherType = Attacher::AttachEngine3D
  Height = 12.2
  Length = 10
  Placement = pos=(70,-5,0) rot=(0,0,1;0rad)
  Width = 5
FEATURE [Part::Box] Box085047  label="Cube134"
  AttacherType = Attacher::AttachEngine3D
  Height = 4.25
  Length = 98
  Placement = pos=(43.75,0,41.75) rot=(0,0,1;0rad)
  Width = 2
FEATURE [Part::Chamfer] Chamfer011006003014
  Base = -> Box085047
  Edges = 1 edges: [Edge2 r1=3.99 r2=9]
FEATURE [Part::Box] Box085046  label="Cube133"
  AttacherType = Attacher::AttachEngine3D
  Height = 15
  Length = 1.75
  Placement = pos=(8.5,0,27) rot=(0,0,1;0rad)
  Width = 1.5
FEATURE [Part::Box] Box085048  label="Cube135"
  AttacherType = Attacher::AttachEngine3D
  Height = 15
  Length = 131.5
  Placement = pos=(10.25,0,27) rot=(0,0,1;0rad)
  Width = 2
FEATURE [Part::Box] Box085049  label="Cube136"
  AttacherType = Attacher::AttachEngine3D
  Height = 19
  Length = 1.75
  Placement = pos=(141.75,0,27) rot=(0,0,1;0rad)
  Width = 1.5
FEATURE [Part::MultiFuse] Fusion004008002002002001007002002015  label="Drawer Hole"
  Placement = pos=(20.5,0,-1) rot=(0,0,1;0rad)
  Shapes = -> [Box085046,Chamfer011006003014,Box085048,Box085049]
FEATURE [Part::Box] Box085050  label="Cube137"
  AttacherType = Attacher::AttachEngine3D
  Height = 5.5
  Length = 6.2
  Placement = pos=(71.8,-5,0) rot=(0,0,1;0rad)
  Width = 5
FEATURE [Part::Box] Box085051  label="Cube138"
  AttacherType = Attacher::AttachEngine3D
  Height = 4.5
  Length = 6
  Placement = pos=(72,-5,0) rot=(0,0,1;0rad)
  Width = 11
FEATURE [Part::Cut] Cut001002016013
  Base = -> Box069
  Tool = -> Box085050
FEATURE [Part::Cylinder] Cylinder034
  Angle = 360
  AttacherType = Attacher::AttachEngine3D
  Height = 10
  Placement = pos=(75,-2.5,0) rot=(1,0,0;0rad)
  Radius = 1.35
FEATURE [Part::Cut] Cut001002016014  label="Touchscreen Stay Screw Top Base"
  Base = -> Box085051
  Placement = pos=(155,58,0) rot=(0,0,1;3.14159rad)
  Tool = -> Cylinder033
FEATURE [Part::Cut] Cut001002016015
  Base = -> Cut001002016013
  Placement = pos=(-4.5,61.25,0) rot=(0,0,1;0rad)
  Tool = -> Cylinder034
FEATURE [Part::MultiFuse] Fusion004008002002002001007002002006  label="Touchscreen Stays"
  Placement = pos=(11,32.55,61.25) rot=(1,0,0;0.436332rad)
  Shapes = -> [Cut001002016,Cut001002016004,Cut001002016010,Cut001002016015]
FEATURE [Part::Chamfer] Chamfer011006003015
  Base = -> Chamfer011004
  Edges = 4 edges r=0.5: [Edge1,Edge3,Edge8,Edge16]
FEATURE [Part::Chamfer] Chamfer011006003016
  Base = -> Chamfer011005
  Edges = 4 edges r=0.5: [Edge1,Edge3,Edge8,Edge16]
FEATURE [Part::Chamfer] Chamfer011006003017002
  Base = -> Fillet005011013
  Edges = 1 edges r=1.99: [Edge11]
FEATURE [Part::Box] Box085055  label="Cube141"
  AttacherType = Attacher::AttachEngine3D
  Height = 4
  Length = 4
  Placement = pos=(65,2,22) rot=(0,0,1;0rad)
  Width = 58
FEATURE [Part::Box] Box085056  label="Cube142"
  AttacherType = Attacher::AttachEngine3D
  Height = 4
  Length = 4
  Placement = pos=(107,2,22) rot=(0,0,1;0rad)
  Width = 58
FEATURE [Part::Box] Box085057  label="Cube143"
  AttacherType = Attacher::AttachEngine3D
  Height = 20
  Length = 4
  Placement = pos=(65,38,2) rot=(0,0,1;0rad)
  Width = 4
FEATURE [Part::Box] Box085058  label="Cube144"
  AttacherType = Attacher::AttachEngine3D
  Height = 20
  Length = 4
  Placement = pos=(65,2,2) rot=(0,0,1;0rad)
  Width = 4
FEATURE [Part::Box] Box085059  label="Cube145"
  AttacherType = Attacher::AttachEngine3D
  Height = 20
  Length = 4
  Placement = pos=(65,56,2) rot=(0,0,1;0rad)
  Width = 4
FEATURE [Part::Box] Box085060  label="Cube146"
  AttacherType = Attacher::AttachEngine3D
  Height = 20
  Length = 4
  Placement = pos=(107,38,2) rot=(0,0,1;0rad)
  Width = 4
FEATURE [Part::Box] Box085061  label="Cube147"
  AttacherType = Attacher::AttachEngine3D
  Height = 20
  Length = 4
  Placement = pos=(107,2,2) rot=(0,0,1;0rad)
  Width = 4
FEATURE [Part::Box] Box085062  label="Cube148"
  AttacherType = Attacher::AttachEngine3D
  Height = 20
  Length = 4
  Placement = pos=(107,56,2) rot=(0,0,1;0rad)
  Width = 4
FEATURE [Part::Box] Box085063  label="Cube149"
  AttacherType = Attacher::AttachEngine3D
  Height = 20
  Length = 4
  Placement = pos=(65,20,2) rot=(0,0,1;0rad)
  Width = 4
FEATURE [Part::Box] Box085064  label="Cube150"
  AttacherType = Attacher::AttachEngine3D
  Height = 20
  Length = 4
  Placement = pos=(107,20,2) rot=(0,0,1;0rad)
  Width = 4
FEATURE [Part::Box] Box085065  label="Cube151"
  AttacherType = Attacher::AttachEngine3D
  Height = 4
  Length = 38
  Placement = pos=(69,20,22) rot=(0,0,1;0rad)
  Width = 4
FEATURE [Part::Box] Box085066  label="Cube152"
  AttacherType = Attacher::AttachEngine3D
  Height = 4
  Length = 38
  Placement = pos=(69,38,22) rot=(0,0,1;0rad)
  Width = 4
FEATURE [Part::Box] Box085067  label="Cube153"
  AttacherType = Attacher::AttachEngine3D
  Height = 20
  Length = 4
  Placement = pos=(79,20,2) rot=(0,0,1;0rad)
  Width = 4
FEATURE [Part::Box] Box085068  label="Cube154"
  AttacherType = Attacher::AttachEngine3D
  Height = 20
  Length = 4
  Placement = pos=(93,20,2) rot=(0,0,1;0rad)
  Width = 4
FEATURE [Part::Box] Box085069  label="Cube155"
  AttacherType = Attacher::AttachEngine3D
  Height = 20
  Length = 4
  Placement = pos=(79,38,2) rot=(0,0,1;0rad)
  Width = 4
FEATURE [Part::Box] Box085070  label="Cube156"
  AttacherType = Attacher::AttachEngine3D
  Height = 20
  Length = 4
  Placement = pos=(93,38,2) rot=(0,0,1;0rad)
  Width = 4
FEATURE [Part::MultiFuse] Fusion004008002002002001007002002018  label="Drawer Rails"
  Shapes = -> [Box085055,Box085056,Box085057,Box085058,Box085059,Box085060,Box085061,Box085062,Box085063,Box085064,Box085065,Box085066,Box085067,Box085068,Box085069,Box085070]
FEATURE [Part::Cylinder] Cylinder035
  Angle = 360
  AttacherType = Attacher::AttachEngine3D
  Height = 50
  Placement = pos=(2.35,0,-2) rot=(0,0,1;0rad)
  Radius = 2.52
FEATURE [Part::Cylinder] Cylinder036
  Angle = 360
  AttacherType = Attacher::AttachEngine3D
  Height = 50
  Placement = pos=(2.35,0,-2) rot=(0,0,1;0rad)
  Radius = 4
FEATURE [Part::Cut] Cut001002016019
  Base = -> Cylinder036
  Placement = pos=(13,7,40) rot=(-1,0,0;1.5708rad)
  Tool = -> Cylinder035
FEATURE [Part::Box] Box082  label="Cube086"
  AttacherType = Attacher::AttachEngine3D
  Height = 6
  Length = 28.75
  Placement = pos=(2,2,24) rot=(0,0,1;0rad)
  Width = 3
FEATURE [Part::Cylinder] Cylinder039
  Angle = 360
  AttacherType = Attacher::AttachEngine3D
  Height = 3
  Placement = pos=(15.35,5,40) rot=(1,0,0;1.5708rad)
  Radius = 7.75
FEATURE [Part::Cylinder] Cylinder040
  Angle = 360
  AttacherType = Attacher::AttachEngine3D
  Height = 30
  Placement = pos=(15.35,32,40) rot=(1,0,0;1.5708rad)
  Radius = 2.52
FEATURE [Part::Cylinder] Cylinder041  label="Stylus Holder Hole"
  Angle = 360
  AttacherType = Attacher::AttachEngine3D
  Height = 7
  Placement = pos=(14.88,7,40.59) rot=(1,0,0;1.5708rad)
  Radius = 2.52
FEATURE [Part::Box] Box085073  label="Cube158"
  AttacherType = Attacher::AttachEngine3D
  Height = 2
  Length = 2
  Placement = pos=(2,77.06,36.5) rot=(1,0,0;0.436332rad)
  Width = 24
FEATURE [Part::Box] Box085074  label="Cube159"
  AttacherType = Attacher::AttachEngine3D
  Height = 6
  Length = 4
  Placement = pos=(2,77.06,36.5) rot=(1,0,0;0.436332rad)
  Width = 24
FEATURE [Part::Cut] Cut001002016021
  Base = -> Box085074
  Tool = -> Box085073
FEATURE [Part::Box] Box085075  label="Cube160"
  AttacherType = Attacher::AttachEngine3D
  Height = 4
  Length = 4
  Placement = pos=(187,77.06,36.5) rot=(1,0,0;0.436332rad)
  Width = 24
FEATURE [Part::Box] Box085076  label="Cube161"
  AttacherType = Attacher::AttachEngine3D
  Height = 2
  Length = 2
  Placement = pos=(189,77.06,36.5) rot=(1,0,0;0.436332rad)
  Width = 24
FEATURE [Part::Cut] Cut001002016022
  Base = -> Box085075
  Tool = -> Box085076
FEATURE [Part::Chamfer] Chamfer011006003017009
  Base = -> Cut001002016022
  Edges = 1 edges: [Edge2 r1=2 r2=3.99]
FEATURE [Part::Chamfer] Chamfer011006003017010
  Base = -> Cut001002016021
  Edges = 1 edges r=3.99: [Edge11]
FEATURE [Part::Feature] Fillet005011017034
  Placement = pos=(0,5,0) rot=(0,0,1;0rad)
  shape: bbox 2 x 3 x 16 mm, 10 faces (baked)
FEATURE [Part::Feature] Fillet005011017035
  Placement = pos=(0,10,0) rot=(0,0,1;0rad)
  shape: bbox 2 x 3 x 16 mm, 10 faces (baked)
FEATURE [Part::Feature] Fillet005011017036
  Placement = pos=(0,15,0) rot=(0,0,1;0rad)
  shape: bbox 2 x 3 x 16 mm, 10 faces (baked)
FEATURE [Part::MultiFuse] Fusion004008002002002001007002002026
  Placement = pos=(0,-5,0) rot=(0,0,1;0rad)
  Shapes = -> [Fillet005011,Fillet005011017034,Fillet005011017035,Fillet005011017036]
FEATURE [Part::Feature] Fusion004008002002002001007002002026001
  Placement = pos=(0,15,0) rot=(0,0,1;0rad)
  shape: bbox 2 x 18 x 16 mm, 40 faces, 4 solids (baked)
FEATURE [Part::Feature] Fusion004008002002002001007002002026002
  Placement = pos=(0,25,0) rot=(0,0,1;0rad)
  shape: bbox 2 x 18 x 16 mm, 40 faces, 4 solids (baked)
FEATURE [Part::MultiFuse] Fusion004008002002002001007002002026003
  Shapes = -> [Fusion004008002002002001007002002026002,Fusion004008002002002001007002002026,Fusion004008002002002001007002002026001]
FEATURE [Part::Feature] Fusion004008002002002001007002002026004
  Placement = pos=(0,10,20) rot=(0,0,1;0rad)
  shape: bbox 2 x 18 x 16 mm, 40 faces, 4 solids (baked)
FEATURE [Part::Feature] Fusion004008002002002001007002002026005
  Placement = pos=(0,30,20) rot=(0,0,1;0rad)
  shape: bbox 2 x 18 x 16 mm, 40 faces, 4 solids (baked)
FEATURE [Part::Feature] Fusion004008002002002001007002002026006
  Placement = pos=(0,50,20) rot=(0,0,1;0rad)
  shape: bbox 2 x 18 x 16 mm, 40 faces, 4 solids (baked)
FEATURE [Part::Feature] Fusion004008002002002001007002002026007
  Placement = pos=(0,60,20) rot=(0,0,1;0rad)
  shape: bbox 2 x 18 x 16 mm, 40 faces, 4 solids (baked)
FEATURE [Part::Feature] Fusion004008002002002001007002002026009
  Placement = pos=(0,55,40) rot=(0,0,1;0rad)
  shape: bbox 2 x 18 x 16 mm, 40 faces, 4 solids (baked)
FEATURE [Part::Feature] Fusion004008002002002001007002002026010
  Placement = pos=(0,75,40) rot=(0,0,1;0rad)
  shape: bbox 2 x 18 x 16 mm, 40 faces, 4 solids (baked)
FEATURE [Part::Feature] Fusion004008002002002001007002002026011
  Placement = pos=(0,80,40) rot=(0,0,1;0rad)
  shape: bbox 2 x 18 x 16 mm, 40 faces, 4 solids (baked)
FEATURE [Part::Cylinder] Cylinder046
  Angle = 360
  AttacherType = Attacher::AttachEngine3D
  Height = 4.2
  Radius = 2.5
FEATURE [Part::Cylinder] Cylinder047
  Angle = 360
  AttacherType = Attacher::AttachEngine3D
  Height = 4.2
  Radius = 1.3
FEATURE [Part::Cut] Cut001002016023
  Base = -> Cylinder046
  Placement = pos=(55,25.73,0) rot=(0,0,1;0rad)
  Tool = -> Cylinder047
FEATURE [Part::Cylinder] Cylinder048
  Angle = 360
  AttacherType = Attacher::AttachEngine3D
  Height = 4.2
  Radius = 2.5
FEATURE [Part::Cylinder] Cylinder049
  Angle = 360
  AttacherType = Attacher::AttachEngine3D
  Height = 4.2
  Radius = 1.3
FEATURE [Part::Cut] Cut001002016024
  Base = -> Cylinder048
  Placement = pos=(55,83.73,0) rot=(0,0,1;0rad)
  Tool = -> Cylinder049
FEATURE [Part::Cylinder] Cylinder050
  Angle = 360
  AttacherType = Attacher::AttachEngine3D
  Height = 4.2
  Radius = 2.5
FEATURE [Part::Cylinder] Cylinder051
  Angle = 360
  AttacherType = Attacher::AttachEngine3D
  Height = 4.2
  Radius = 1.3
FEATURE [Part::Cut] Cut001002016025
  Base = -> Cylinder050
  Placement = pos=(6,83.73,0) rot=(0,0,1;0rad)
  Tool = -> Cylinder051
FEATURE [Part::MultiFuse] Fusion003  label="Raspberry Pi 3B+ Screw Holes"
  Placement = pos=(0,0,1) rot=(0,0,1;0rad)
  Shapes = -> [Cut001002,Cut001002016023,Cut001002016024,Cut001002016025]
FEATURE [App::DocumentObjectGroup] Group002  label="Screw Holes"
  Group = -> [Fusion002,Fusion003]
FEATURE [App::DocumentObjectGroup] GrExplode_Slice016  label="Exploded Slice016"
FEATURE [Part::MultiFuse] Fusion004008002002002001007002002026012005  label="Tab Holes"
  Shapes = -> [Box085014,Box085017]
FEATURE [Part::MultiFuse] Fusion004008002002002001007002002026012007  label="Tabs"
  Shapes = -> [Chamfer011006003015,Chamfer011006003016]
FEATURE [Part::Box] Box085078  label="Cube163"
  AttacherType = Attacher::AttachEngine3D
  Height = 16
  Length = 15.75
  Placement = pos=(7.5,2,32.75) rot=(0,0,1;0rad)
  Width = 3.15
FEATURE [Part::Box] Box085079  label="Cube164"
  AttacherType = Attacher::AttachEngine3D
  Height = 18
  Length = 19.75
  Placement = pos=(5.5,2,32.75) rot=(0,0,1;0rad)
  Width = 5.2
FEATURE [Part::Fillet] Fillet005011017037
  Base = -> Box085078
  Edges = 2 edges r=7: [Edge2,Edge6]
FEATURE [Part::Fillet] Fillet005011017038
  Base = -> Box085079
  Edges = 2 edges r=8: [Edge2,Edge6]
FEATURE [Part::Cylinder] Cylinder052
  Angle = 360
  AttacherType = Attacher::AttachEngine3D
  Height = 30
  Placement = pos=(15.38,0,40.6) rot=(-1,0,0;1.5708rad)
  Radius = 4
FEATURE [Part::Box] Box085080  label="Cube165"
  AttacherType = Attacher::AttachEngine3D
  Height = 8
  Length = 8
  Placement = pos=(11.4,5.15,32.62) rot=(0,0,1;0rad)
  Width = 2.05
FEATURE [Part::Box] Box085084  label="Cube169"
  AttacherType = Attacher::AttachEngine3D
  Height = 15.8
  Length = 8.1
  Placement = pos=(15.9,118,17.9) rot=(0,0,1;0rad)
  Width = 10
FEATURE [Part::Fillet] Fillet005011017044
  Base = -> Box085084
  Edges = 2 edges r=3.25: [Edge2,Edge6]
FEATURE [Part::Cylinder] Cylinder053
  Angle = 360
  AttacherType = Attacher::AttachEngine3D
  Height = 10
  Placement = pos=(20,128,15.5) rot=(1,0,0;1.5708rad)
  Radius = 1.6
FEATURE [Part::Cylinder] Cylinder054
  Angle = 360
  AttacherType = Attacher::AttachEngine3D
  Height = 10
  Placement = pos=(20,128,36.1) rot=(1,0,0;1.5708rad)
  Radius = 1.6
FEATURE [Part::MultiFuse] Fusion004008002002002001007002002026012008  label="XT60E-M Holes"
  Placement = pos=(149.7,-4,13.1) rot=(0,-1,0;1.5708rad)
  Shapes = -> [Cylinder054,Fillet005011017044,Cylinder053]
FEATURE [Part::Box] Box085085  label="Cube170"
  AttacherType = Attacher::AttachEngine3D
  Height = 14
  Length = 8
  Placement = pos=(15.5,3,33.62) rot=(0,0,1;0rad)
  Width = 9.2
FEATURE [Part::Chamfer] Chamfer011006003017013
  Base = -> Box085085
  Edges = 2 edges r=3: [Edge11,Edge12]
FEATURE [Part::Cylinder] Cylinder055
  Angle = 360
  AttacherType = Attacher::AttachEngine3D
  Height = 4
  Placement = pos=(15.38,7.2,40.6) rot=(-1,0,0;1.5708rad)
  Radius = 7.75
FEATURE [Part::Chamfer] Chamfer011006003017014
  Base = -> Cylinder055
  Edges = 1 edges: [Edge1 r1=3 r2=2]
FEATURE [Part::FeaturePython] Slice017  # WARN: FeaturePython — macro-defined, semantics opaque (R4)
  Base = -> Fillet005011017038
  Mode = 1
  Tolerance = 0
  Tools = -> [Fillet005011017037,Cylinder052,Box085080]
FEATURE [Part::FeaturePython] Slice017_child0  label="Slice017.0"  # WARN: FeaturePython — macro-defined, semantics opaque (R4)
  Base = -> Slice017
  FilterType = 1
  Invert = false
  OverrideMaxVal = 0
  Placement = pos=(-0.5,0,0) rot=(0,0,1;0rad)
  WindowFrom = 80
  WindowTo = 100
  items = 0
FEATURE [Part::FeaturePython] Slice017_child1  label="Slice017.1"  # WARN: FeaturePython — macro-defined, semantics opaque (R4)
  Base = -> Slice017
  FilterType = 1
  Invert = false
  OverrideMaxVal = 0
  WindowFrom = 80
  WindowTo = 100
  items = 1
FEATURE [Part::FeaturePython] Slice017_child2  label="Slice017.2"  # WARN: FeaturePython — macro-defined, semantics opaque (R4)
  Base = -> Slice017
  FilterType = 1
  Invert = false
  OverrideMaxVal = 0
  WindowFrom = 80
  WindowTo = 100
  items = 2
FEATURE [Part::FeaturePython] Slice017_child3  label="Slice017.3"  # WARN: FeaturePython — macro-defined, semantics opaque (R4)
  Base = -> Slice017
  FilterType = 1
  Invert = false
  OverrideMaxVal = 0
  WindowFrom = 80
  WindowTo = 100
  items = 3
FEATURE [Part::FeaturePython] Slice017_child4  label="Slice017.4"  # WARN: FeaturePython — macro-defined, semantics opaque (R4)
  Base = -> Slice017
  FilterType = 1
  Invert = false
  OverrideMaxVal = 0
  WindowFrom = 80
  WindowTo = 100
  items = 4
FEATURE [Part::FeaturePython] Slice017_child5  label="Slice017.5"  # WARN: FeaturePython — macro-defined, semantics opaque (R4)
  Base = -> Slice017
  FilterType = 1
  Invert = false
  OverrideMaxVal = 0
  WindowFrom = 80
  WindowTo = 100
  items = 5
FEATURE [App::DocumentObjectGroup] GrExplode_Slice017  label="Exploded Slice017"
  Group = -> [Slice017_child1,Slice017_child2,Slice017_child3,Slice017_child4,Slice017_child5]
FEATURE [Part::Box] Box085101  label="Cube186"
  AttacherType = Attacher::AttachEngine3D
  Height = 6
  Length = 2.75
  Placement = pos=(160.75,2,45) rot=(0,0,1;0rad)
  Width = 12
FEATURE [Part::Chamfer] Chamfer011006003017037
  Base = -> Box085101
  Edges = 1 edges: [Edge12 r1=4.99 r2=11.99]
FEATURE [Part::Box] Box085102  label="Cube187"
  AttacherType = Attacher::AttachEngine3D
  Height = 6
  Length = 2.75
  Placement = pos=(29.5,2,41) rot=(0,1,0;0rad)
  Width = 12
FEATURE [Part::Chamfer] Chamfer011006003017038
  Base = -> Box085102
  Edges = 1 edges: [Edge12 r1=4.99 r2=11.99]
FEATURE [Part::Box] Box085103  label="False wall"
  AttacherType = Attacher::AttachEngine3D
  Height = 12
  Length = 14
  Placement = pos=(155,0,2) rot=(0,0,1;0rad)
  Width = 2
FEATURE [Part::Box] Box085104  label="False floor"
  AttacherType = Attacher::AttachEngine3D
  Height = 1
  Length = 71
  Placement = pos=(118,2,1) rot=(0,0,1;0rad)
  Width = 102
FEATURE [Part::Box] Box085105  label="False wall001"
  AttacherType = Attacher::AttachEngine3D
  Height = 10
  Length = 56.5
  Placement = pos=(2,0,1) rot=(0,0,1;0rad)
  Width = 2
FEATURE [Part::Box] Box085106  label="False floor001"
  AttacherType = Attacher::AttachEngine3D
  Height = 1
  Length = 56.5
  Placement = pos=(2,2,1) rot=(0,0,1;0rad)
  Width = 85
FEATURE [Part::Box] Box085107  label="Cube188"
  AttacherType = Attacher::AttachEngine3D
  Height = 26
  Length = 59
  Width = 83
FEATURE [Part::Cylinder] Cylinder058  label="40mm Fan Hole"
  Angle = 360
  AttacherType = Attacher::AttachEngine3D
  Height = 20
  Placement = pos=(166,137,25) rot=(1,0,0;1.5708rad)
  Radius = 19
FEATURE [Part::Box] Box085108  label="Cube189"
  AttacherType = Attacher::AttachEngine3D
  Height = 40
  Length = 40
  Width = 11.2
FEATURE [Part::Cylinder] Cylinder057
  Angle = 360
  AttacherType = Attacher::AttachEngine3D
  Height = 10
  Placement = pos=(20,10,20) rot=(1,0,0;1.5708rad)
  Radius = 18.5
FEATURE [Part::Cut] Cut001002016030
  Base = -> Box085108
  Tool = -> Cylinder057
FEATURE [Part::Fillet] Fillet005011017060  label="40mm Fan"
  Base = -> Cut001002016030
  Edges = 4 edges r=2: [Edge2,Edge4,Edge10,Edge13]
  Placement = pos=(151,106.8,6) rot=(0,0,1;0rad)
FEATURE [Part::Feature] Fillet005011017073 .. Fillet005011017078  x6 (patterned run collapsed; names and placements below)
  shape: bbox 2 x 16 x 3 mm, 10 faces (baked)
  placements: 6 in arithmetic series — first pos=(0,-22,34) rot=(-1,0,0;1.5708rad), step (0,18,-7.10543e-15), last pos=(0,68,34) rot=(-1,0,0;1.5708rad)
FEATURE [Part::Feature] Fillet005011017079
  Placement = pos=(0,95,0) rot=(0,0,1;0rad)
  shape: bbox 2 x 3 x 16 mm, 10 faces (baked)
FEATURE [Part::Feature] Fillet005011017080
  Placement = pos=(0,90,0) rot=(0,0,1;0rad)
  shape: bbox 2 x 3 x 16 mm, 10 faces (baked)
FEATURE [Part::Box] Box085121  label="Cube202"
  AttacherType = Attacher::AttachEngine3D
  Height = 29
  Length = 2
  Placement = pos=(0,12,29) rot=(1,0,0;3.14159rad)
  Width = 3
FEATURE [Part::Fillet] Fillet005011017082
  Base = -> Box085121
  Edges = 4 edges r=1.49: [Edge9,Edge10,Edge11,Edge12]
  Placement = pos=(0,68.631,39.37) rot=(-1,0,0;1.13446rad)
FEATURE [Part::Feature] Fillet005011017082001
  Placement = pos=(0,52.8713,29.77) rot=(-1,0,0;1.13446rad)
  shape: bbox 2 x 14.79 x 8.501 mm, 10 faces (baked)
FEATURE [Part::Cut] Cut001002016039
  Base = -> Cylinder039
  Tool = -> Cylinder040
FEATURE [Part::MultiFuse] Fusion004008002002002001007002002026012019  label="Stylus Holder"
  Placement = pos=(-0.5,0,0.5) rot=(0,0,1;0rad)
  Shapes = -> [Cut001002016019,Cut001002016039]
FEATURE [Part::Feature] Fillet005011017082002
  Placement = pos=(0,50,29) rot=(-1,0,0;1.5708rad)
  shape: bbox 2 x 16 x 3 mm, 10 faces (baked)
FEATURE [Part::Feature] Fillet005011017082003
  Placement = pos=(0,-22,29) rot=(-1,0,0;1.5708rad)
  shape: bbox 2 x 16 x 3 mm, 10 faces (baked)
FEATURE [Part::Feature] Fillet005011017082004
  Placement = pos=(0,14,29) rot=(-1,0,0;1.5708rad)
  shape: bbox 2 x 16 x 3 mm, 10 faces (baked)
FEATURE [Part::Feature] Fillet005011017082005
  Placement = pos=(0,-4,29) rot=(-1,0,0;1.5708rad)
  shape: bbox 2 x 16 x 3 mm, 10 faces (baked)
FEATURE [Part::Feature] Fillet005011017082006
  Placement = pos=(0,68,29) rot=(-1,0,0;1.5708rad)
  shape: bbox 2 x 16 x 3 mm, 10 faces (baked)
FEATURE [Part::Feature] Fillet005011017082007
  Placement = pos=(0,32,29) rot=(-1,0,0;1.5708rad)
  shape: bbox 2 x 16 x 3 mm, 10 faces (baked)
FEATURE [Part::MultiFuse] Fusion004008002002002001007002002026012  label="Left Side Vents"
  Shapes = -> [Fusion004008002002002001007002002026003,Fusion004008002002002001007002002026004,Fusion004008002002002001007002002026005,Fusion004008002002002001007002002026006,Fusion004008002002002001007002002026007,Fusion004008002002002001007002002026009,Fusion004008002002002001007002002026010,Fusion004008002002002001007002002026011,Fillet005011017082,Fillet005011017079,Fillet005011017077,Fillet005011017073,+12 more]
FEATURE [Part::Feature] Fusion004008002002002001007002002026012020  label="Right Side Vents"
  Placement = pos=(191,0,0) rot=(0,0,1;0rad)
  shape: large baked B-rep (36 MB .brp); summary skipped
FEATURE [Part::Box] Box085123  label="Cube204"
  AttacherType = Attacher::AttachEngine3D
  Height = 4.5
  Length = 28.1
  Placement = pos=(48.9,52,0) rot=(0,0,1;0rad)
  Width = 4.5
FEATURE [Part::MultiFuse] Fusion004008002002002001007002002026012021  label="Touchscreen Stay Screw Top"
  Shapes = -> [Box085123,Cut001002016014]
FEATURE [Part::Box] Box085124  label="Cube205"
  AttacherType = Attacher::AttachEngine3D
  Height = 6
  Length = 2
  Placement = pos=(1,95,38) rot=(0,0,1;0rad)
  Width = 3
FEATURE [Part::Chamfer] Chamfer011006003017044
  Base = -> Box085124
  Edges = 2 edges: [Edge11 r1=0.5 r2=2.75,Edge12 r1=0.5 r2=2.75]
  Placement = pos=(10,17.2,99.001) rot=(0,1,0;1.5708rad)
FEATURE [Part::Chamfer] Chamfer011006003017046
  Base = -> Chamfer011006003017044
  Edges = 4 edges r=0.5: [Edge1,Edge3,Edge8,Edge16]
  Placement = pos=(-25,-110.2,-70) rot=(0,0,1;0rad)
FEATURE [Part::Box] Box085126  label="Cube207"
  AttacherType = Attacher::AttachEngine3D
  Height = 6.2
  Length = 2.4
  Placement = pos=(22.9,2,28.2) rot=(0,1,0;1.5708rad)
  Width = 10.2
FEATURE [Part::Box] Box085128  label="Cube209"
  AttacherType = Attacher::AttachEngine3D
  Height = 6
  Length = 2
  Placement = pos=(1,95,38) rot=(0,0,1;0rad)
  Width = 3
FEATURE [Part::Chamfer] Chamfer011006003017047
  Base = -> Box085128
  Edges = 2 edges: [Edge11 r1=0.5 r2=2.75,Edge12 r1=0.5 r2=2.75]
  Placement = pos=(10,17.2,99.001) rot=(0,1,0;1.5708rad)
FEATURE [Part::Chamfer] Chamfer011006003017048
  Base = -> Chamfer011006003017047
  Edges = 4 edges r=0.5: [Edge1,Edge3,Edge8,Edge16]
  Placement = pos=(116,-110.2,-70) rot=(0,0,1;0rad)
FEATURE [Part::MultiFuse] Fusion004008002002002001007002002026012024  label="Front Tabs 1"
  Placement = pos=(0,0,1) rot=(0,0,1;0rad)
  Shapes = -> [Chamfer011006003017048,Chamfer011006003017046]
FEATURE [Part::Box] Box085129  label="Cube210"
  AttacherType = Attacher::AttachEngine3D
  Height = 6.2
  Length = 2.4
  Placement = pos=(163.9,2,28.2) rot=(0,1,0;1.5708rad)
  Width = 10.2
FEATURE [Part::MultiFuse] Fusion004008002002002001007002002026012025  label="Front Tab Holes"
  Placement = pos=(0,0,1) rot=(0,0,1;0rad)
  Shapes = -> [Box085126,Box085129]
FEATURE [Part::Box] Box085130  label="Cube211"
  AttacherType = Attacher::AttachEngine3D
  Height = 14.5
  Length = 29.5
  Placement = pos=(113.15,117,27.8) rot=(0,0,1;0rad)
  Width = 1
FEATURE [Part::Chamfer] Chamfer011006003017049
  Base = -> Box085130
  Edges = 4 edges r=0.98: [Edge1,Edge5,Edge9,Edge10]
  Placement = pos=(-4,0,-2) rot=(0,0,1;0rad)
FEATURE [Part::Cut] Cut001002016041
  Base = -> Chamfer011006003017049
  Tool = -> Fusion004008002002002001007002002026012008
FEATURE [Part::Box] Box085134  label="Cube215"
  AttacherType = Attacher::AttachEngine3D
  Height = 20
  Length = 2.2
  Placement = pos=(189,115.8,16) rot=(0,0,1;0rad)
  Width = 2.2
FEATURE [Part::Box] Box085135  label="Cube216"
  AttacherType = Attacher::AttachEngine3D
  Height = 24
  Length = 4
  Placement = pos=(189,114,12) rot=(0,0,1;0rad)
  Width = 4
FEATURE [Part::Chamfer] Chamfer011006003017053
  Base = -> Box085135
  Edges = 1 edges r=3.99: [Edge9]
FEATURE [Part::Cut] Cut001002016046
  Base = -> Chamfer011006003017053
  Tool = -> Box085134
FEATURE [Part::Fillet] Fillet005011017082014
  Base = -> Cut001002016046
  Edges = 1 edges r=2: [Edge8]
  Placement = pos=(-2,0,0) rot=(0,0,1;0rad)
FEATURE [Part::Box] Box085136  label="Cube217"
  AttacherType = Attacher::AttachEngine3D
  Height = 20
  Length = 2.2
  Placement = pos=(144.8,115.8,16) rot=(0,0,1;0rad)
  Width = 2.2
FEATURE [Part::Box] Box085137  label="Cube218"
  AttacherType = Attacher::AttachEngine3D
  Height = 24
  Length = 4
  Placement = pos=(143,114,12) rot=(0,0,1;0rad)
  Width = 4
FEATURE [Part::Chamfer] Chamfer011006003017054
  Base = -> Box085137
  Edges = 1 edges r=3.99: [Edge9]
FEATURE [Part::Cut] Cut001002016047
  Base = -> Chamfer011006003017054
  Tool = -> Box085136
FEATURE [Part::Fillet] Fillet005011017082015
  Base = -> Cut001002016047
  Edges = 1 edges r=2: [Edge1]
  Placement = pos=(-2,0,0) rot=(0,0,1;0rad)
FEATURE [Part::Box] Box085140  label="Cube221"
  AttacherType = Attacher::AttachEngine3D
  Height = 42
  Length = 50
  Placement = pos=(141,118,3) rot=(0,0,1;0rad)
  Width = 1
FEATURE [Part::Feature] Face083  label="Face084"
  Placement = pos=(143,112,7) rot=(0,0,1;0rad)
  shape: bbox 46 x 2e-07 x 38 mm, 1 faces, 0 solids (baked)
FEATURE [Part::Cylinder] Cylinder066
  Angle = 360
  AttacherType = Attacher::AttachEngine3D
  Height = 21
  Placement = pos=(166,121,24) rot=(1,0,0;1.5708rad)
  Radius = 19
FEATURE [Part::Chamfer] Chamfer011006003017057
  Base = -> Cylinder066
  Edges = 1 edges: [Edge1 r1=18.99 r2=5]
FEATURE [Part::Cut] Cut001002016050
  Base = -> Box085140
  Tool = -> Chamfer011006003017057
FEATURE [Part::Box] Box085142  label="Cube223"
  AttacherType = Attacher::AttachEngine3D
  Height = 38
  Length = 38
  Placement = pos=(147,117,5) rot=(0,0,1;0rad)
  Width = 1
FEATURE [Part::Box] Box085143  label="Cube224"
  AttacherType = Attacher::AttachEngine3D
  Height = 24
  Length = 30
  Placement = pos=(152,99,14) rot=(0,0,1;0rad)
  Width = 1
FEATURE [Part::Box] Box085144  label="Cube225"
  AttacherType = Attacher::AttachEngine3D
  Height = 22
  Length = 26
  Placement = pos=(154,99,14) rot=(0,0,1;0rad)
  Width = 1
FEATURE [Part::Box] Box085145  label="Cube226"
  AttacherType = Attacher::AttachEngine3D
  Height = 17
  Length = 14
  Placement = pos=(163,63,14) rot=(0,0,1;0rad)
  Width = 1
FEATURE [Part::Box] Box085146  label="Cube227"
  AttacherType = Attacher::AttachEngine3D
  Height = 15
  Length = 10
  Placement = pos=(165,63,14) rot=(0,0,1;0rad)
  Width = 1
FEATURE [Part::Box] Box085147  label="Cube228"
  AttacherType = Attacher::AttachEngine3D
  Height = 10
  Length = 14
  Placement = pos=(163,24,14) rot=(0,0,1;0rad)
  Width = 1
FEATURE [Part::Box] Box085148  label="Cube229"
  AttacherType = Attacher::AttachEngine3D
  Height = 8
  Length = 10
  Placement = pos=(165,24,14) rot=(0,0,1;0rad)
  Width = 1
FEATURE [Part::Box] Box085141  label="Cube222"
  AttacherType = Attacher::AttachEngine3D
  Height = 42
  Length = 42
  Placement = pos=(145,117,3) rot=(0,0,1;0rad)
  Width = 1
FEATURE [Part::Box] Box085149  label="Cube230"
  AttacherType = Attacher::AttachEngine3D
  Height = 42
  Length = 42
  Placement = pos=(145,117,3) rot=(0,0,1;0rad)
  Width = 1
FEATURE [Part::Box] Box085150  label="Cube231"
  AttacherType = Attacher::AttachEngine3D
  Height = 38
  Length = 38
  Placement = pos=(147,117,5) rot=(0,0,1;0rad)
  Width = 1
FEATURE [Part::Box] Box085151  label="Cube232"
  AttacherType = Attacher::AttachEngine3D
  Height = 31
  Length = 30
  Placement = pos=(152,99,14) rot=(0,0,1;0rad)
  Width = 1
FEATURE [Part::Box] Box085152  label="Cube233"
  AttacherType = Attacher::AttachEngine3D
  Height = 29
  Length = 26
  Placement = pos=(154,99,14) rot=(0,0,1;0rad)
  Width = 1
FEATURE [Part::Box] Box085153  label="Cube234"
  AttacherType = Attacher::AttachEngine3D
  Height = 17
  Length = 15
  Placement = pos=(163,63,14) rot=(0,0,1;0rad)
  Width = 1
FEATURE [Part::Box] Box085154  label="Cube235"
  AttacherType = Attacher::AttachEngine3D
  Height = 15
  Length = 11
  Placement = pos=(165,63,14) rot=(0,0,1;0rad)
  Width = 1
FEATURE [Part::Box] Box085155  label="Cube236"
  AttacherType = Attacher::AttachEngine3D
  Height = 10
  Length = 14
  Placement = pos=(163,24,14) rot=(0,0,1;0rad)
  Width = 1
FEATURE [Part::Box] Box085156  label="Cube237"
  AttacherType = Attacher::AttachEngine3D
  Height = 8
  Length = 10
  Placement = pos=(165,24,14) rot=(0,0,1;0rad)
  Width = 1
FEATURE [Part::Fillet] Fillet005011017082029
  Base = -> Box085155
  Edges = 2 edges r=6.99: [Edge2,Edge6]
FEATURE [Part::Fillet] Fillet005011017082030
  Base = -> Box085153
  Edges = 2 edges r=7.49: [Edge2,Edge6]
FEATURE [Part::Fillet] Fillet005011017082031
  Base = -> Box085150
  Edges = 2 edges r=18.9: [Edge2,Edge6]
FEATURE [Part::Fillet] Fillet005011017082032
  Base = -> Box085154
  Edges = 2 edges r=5.49: [Edge2,Edge6]
FEATURE [Part::Fillet] Fillet005011017082033
  Base = -> Box085156
  Edges = 2 edges r=4.99: [Edge2,Edge6]
FEATURE [Part::Fillet] Fillet005011017082034
  Base = -> Box085151
  Edges = 2 edges r=14.99: [Edge2,Edge6]
FEATURE [Part::Fillet] Fillet005011017082035
  Base = -> Box085152
  Edges = 2 edges r=12.99: [Edge2,Edge6]
FEATURE [Part::Fillet] Fillet005011017082036
  Base = -> Box085149
  Edges = 2 edges r=20.99: [Edge2,Edge6]
FEATURE [Part::Feature] Face087  label="Face089"
  Placement = pos=(147,117,5) rot=(0,0,1;0rad)
  shape: bbox 38 x 2e-07 x 38 mm, 1 faces, 0 solids (baked)
FEATURE [Part::Feature] Face091  label="Face093"
  Placement = pos=(145,117,3) rot=(0,0,1;0rad)
  shape: bbox 42 x 2e-07 x 42 mm, 1 faces, 0 solids (baked)
FEATURE [Part::Feature] Face095  label="Face097"
  Placement = pos=(154,99,14) rot=(0,0,1;0rad)
  shape: bbox 26 x 2e-07 x 22 mm, 1 faces, 0 solids (baked)
FEATURE [Part::Feature] Face099  label="Face101"
  Placement = pos=(152,99,14) rot=(0,0,1;0rad)
  shape: bbox 30 x 2e-07 x 24 mm, 1 faces, 0 solids (baked)
FEATURE [Part::Feature] Face103  label="Face105"
  Placement = pos=(165,63,14) rot=(0,0,1;0rad)
  shape: bbox 10 x 2e-07 x 15 mm, 1 faces, 0 solids (baked)
FEATURE [Part::Feature] Face107  label="Face109"
  Placement = pos=(163,63,14) rot=(0,0,1;0rad)
  shape: bbox 14 x 2e-07 x 17 mm, 1 faces, 0 solids (baked)
FEATURE [Part::Feature] Face111  label="Face113"
  Placement = pos=(165,24,14) rot=(0,0,1;0rad)
  shape: bbox 10 x 2e-07 x 8 mm, 1 faces, 0 solids (baked)
FEATURE [Part::Feature] Face115  label="Face117"
  Placement = pos=(163,24,14) rot=(0,0,1;0rad)
  shape: bbox 14 x 2e-07 x 10 mm, 1 faces, 0 solids (baked)
FEATURE [Part::Box] Box085157  label="Cube238"
  AttacherType = Attacher::AttachEngine3D
  Height = 19.9
  Length = 6
  Placement = pos=(143,116,14.1) rot=(0,0,1;0rad)
  Width = 2
FEATURE [Part::Fillet] Fillet005011017082037
  Base = -> Box085157
  Edges = 2 edges r=2: [Edge2,Edge4]
FEATURE [Part::Box] Box085158  label="Cube239"
  AttacherType = Attacher::AttachEngine3D
  Height = 19.9
  Length = 6
  Placement = pos=(183,116,14.1) rot=(0,0,1;0rad)
  Width = 2
FEATURE [Part::Fillet] Fillet005011017082038
  Base = -> Box085158
  Edges = 2 edges r=1.99: [Edge6,Edge8]
FEATURE [Part::MultiFuse] Fusion004008002002002001007002002026012028
  Shapes = -> [Fillet005011017082037,Fillet005011017082038]
FEATURE [Part::Feature] Cut001002016053001
  shape: bbox 42 x 93 x 42 mm, 38 faces (baked)
FEATURE [Part::FeaturePython] Slice018  # WARN: FeaturePython — macro-defined, semantics opaque (R4)
  Base = -> Fusion004008002002002001007002002026012028
  Mode = 1
  Tolerance = 0
  Tools = -> [Cut001002016053001]
FEATURE [Part::FeaturePython] Slice018_child0  label="Slice018.0"  # WARN: FeaturePython — macro-defined, semantics opaque (R4)
  Base = -> Slice018
  FilterType = 1
  Invert = false
  OverrideMaxVal = 0
  WindowFrom = 80
  WindowTo = 100
  items = 0
FEATURE [Part::FeaturePython] Slice018_child1  label="Slice018.1"  # WARN: FeaturePython — macro-defined, semantics opaque (R4)
  Base = -> Slice018
  FilterType = 1
  Invert = false
  OverrideMaxVal = 0
  WindowFrom = 80
  WindowTo = 100
  items = 1
FEATURE [Part::FeaturePython] Slice018_child2  label="Slice018.2"  # WARN: FeaturePython — macro-defined, semantics opaque (R4)
  Base = -> Slice018
  FilterType = 1
  Invert = false
  OverrideMaxVal = 0
  WindowFrom = 80
  WindowTo = 100
  items = 2
FEATURE [Part::FeaturePython] Slice018_child3  label="Slice018.3"  # WARN: FeaturePython — macro-defined, semantics opaque (R4)
  Base = -> Slice018
  FilterType = 1
  Invert = false
  OverrideMaxVal = 0
  WindowFrom = 80
  WindowTo = 100
  items = 3
FEATURE [Part::FeaturePython] Slice018_child4  label="Slice018.4"  # WARN: FeaturePython — macro-defined, semantics opaque (R4)
  Base = -> Slice018
  FilterType = 1
  Invert = false
  OverrideMaxVal = 0
  WindowFrom = 80
  WindowTo = 100
  items = 4
FEATURE [Part::FeaturePython] Slice018_child5  label="Slice018.5"  # WARN: FeaturePython — macro-defined, semantics opaque (R4)
  Base = -> Slice018
  FilterType = 1
  Invert = false
  OverrideMaxVal = 0
  WindowFrom = 80
  WindowTo = 100
  items = 5
FEATURE [App::DocumentObjectGroup] GrExplode_Slice018  label="Exploded Slice018"
  Group = -> [Slice018_child1,Slice018_child2,Slice018_child4,Slice018_child5]
FEATURE [Part::Box] Box085159  label="Cube240"
  AttacherType = Attacher::AttachEngine3D
  Height = 11
  Length = 10
  Placement = pos=(165,100,5) rot=(0,0,1;0rad)
  Width = 18
FEATURE [Part::Feature] Face119  label="Face121"
  Placement = pos=(154,99,16) rot=(0,0,1;0rad)
  shape: bbox 26 x 2e-07 x 20 mm, 1 faces, 0 solids (baked)
FEATURE [Part::Feature] Face123  label="Face125"
  Placement = pos=(152,99,14) rot=(0,0,1;0rad)
  shape: bbox 30 x 2e-07 x 24 mm, 1 faces, 0 solids (baked)
FEATURE [Part::Loft] Loft
  Closed = false
  MaxDegree = 5
  Ruled = true
  Sections = -> [Face087,Face119]
  Solid = true
FEATURE [Part::Loft] Loft001
  Closed = false
  MaxDegree = 5
  Ruled = true
  Sections = -> [Face091,Face123]
  Solid = true
FEATURE [Part::Cut] Cut001002016053002
  Base = -> Loft001
  Tool = -> Loft
FEATURE [Part::Loft] Loft002
  Closed = false
  MaxDegree = 5
  Ruled = true
  Sections = -> [Face095,Face103,Face111]
  Solid = true
FEATURE [Part::Loft] Loft003
  Closed = false
  MaxDegree = 5
  Ruled = true
  Sections = -> [Face099,Face107,Face115]
  Solid = true
FEATURE [Part::Cut] Cut001002016053003
  Base = -> Loft003
  Tool = -> Loft002
FEATURE [Part::Cut] Cut001002016053004
  Base = -> Cut001002016053002
  Tool = -> Box085159
FEATURE [Part::MultiFuse] Fusion004008002002002001007002002026012029  label="SKR Board Duct Old"
  Shapes = -> [Cut001002016053003,Cut001002016053004]
FEATURE [Part::Box] Box085160  label="Cube241"
  AttacherType = Attacher::AttachEngine3D
  Height = 6
  Length = 1.25
  Placement = pos=(29.5,2,35) rot=(0,1,0;0rad)
  Width = 12
FEATURE [Part::Box] Box085161  label="Cube242"
  AttacherType = Attacher::AttachEngine3D
  Height = 6
  Length = 1.25
  Placement = pos=(162.25,2,39) rot=(0,0,1;0rad)
  Width = 12
FEATURE [Part::MultiFuse] Fusion004008002002002001007002002026012030
  Shapes = -> [Chamfer011006003017037,Box085161]
FEATURE [Part::MultiFuse] Fusion004008002002002001007002002026012031
  Shapes = -> [Chamfer011006003017038,Box085160]
FEATURE [Part::Feature] Face124
  Placement = pos=(145,117,3) rot=(0,0,1;0rad)
  shape: bbox 42 x 2e-07 x 42 mm, 1 faces, 0 solids (baked)
FEATURE [Part::Feature] Face125  label="Face126"
  Placement = pos=(147,117,5) rot=(0,0,1;0rad)
  shape: bbox 38 x 2e-07 x 38 mm, 1 faces, 0 solids (baked)
FEATURE [Part::Feature] Face126  label="Face127"
  Placement = pos=(165,63,14) rot=(0,0,1;0rad)
  shape: bbox 10 x 2e-07 x 15 mm, 1 faces, 0 solids (baked)
FEATURE [Part::Feature] Face127  label="Face128"
  Placement = pos=(165,24,14) rot=(0,0,1;0rad)
  shape: bbox 10 x 2e-07 x 8 mm, 1 faces, 0 solids (baked)
FEATURE [Part::Feature] Face128  label="Face129"
  Placement = pos=(163,24,14) rot=(0,0,1;0rad)
  shape: bbox 14 x 2e-07 x 10 mm, 1 faces, 0 solids (baked)
FEATURE [Part::Feature] Face129  label="Face130"
  Placement = pos=(163,63,14) rot=(0,0,1;0rad)
  shape: bbox 14 x 2e-07 x 17 mm, 1 faces, 0 solids (baked)
FEATURE [Part::Feature] Face133  label="Face135"
  Placement = pos=(154,99,14) rot=(0,0,1;0rad)
  shape: bbox 26 x 2e-07 x 29 mm, 1 faces, 0 solids (baked)
FEATURE [Part::Feature] Face137  label="Face139"
  Placement = pos=(152,99,14) rot=(0,0,1;0rad)
  shape: bbox 30 x 2e-07 x 31 mm, 1 faces, 0 solids (baked)
FEATURE [Part::Box] Box085162  label="Cube243"
  AttacherType = Attacher::AttachEngine3D
  Height = 27
  Length = 26
  Placement = pos=(154,99,16) rot=(0,0,1;0rad)
  Width = 1
FEATURE [Part::Fillet] Fillet005011017082039
  Base = -> Box085162
  Edges = 2 edges r=12.99: [Edge2,Edge6]
FEATURE [App::DocumentObjectGroup] Group011  label="Duct Backup"
  Group = -> [Fillet005011017082036,Fillet005011017082029,Fillet005011017082034,Fillet005011017082030,Fillet005011017082033,Fillet005011017082031,Fillet005011017082035,Fillet005011017082032,Box085141,Box085142,Box085143,Box085144,Box085145,Box085146,Box085147,Box085148,Fillet005011017082039]
FEATURE [Part::Feature] Face141  label="Face143"
  Placement = pos=(154,99,16) rot=(0,0,1;0rad)
  shape: bbox 26 x 2e-07 x 27 mm, 1 faces, 0 solids (baked)
FEATURE [Part::Loft] Loft005
  Closed = false
  MaxDegree = 5
  Ruled = true
  Sections = -> [Face137,Face124]
  Solid = true
FEATURE [Part::Feature] Face145  label="Face147"
  Placement = pos=(152,99,14) rot=(0,0,1;0rad)
  shape: bbox 30 x 2e-07 x 31 mm, 1 faces, 0 solids (baked)
FEATURE [Part::Loft] Loft006
  Closed = false
  MaxDegree = 5
  Ruled = true
  Sections = -> [Face128,Face129,Face145]
  Solid = true
FEATURE [Part::Loft] Loft007
  Closed = false
  MaxDegree = 5
  Ruled = true
  Sections = -> [Face133,Face126,Face127]
  Solid = true
FEATURE [Part::Cut] Cut001002016053005
  Base = -> Loft006
  Tool = -> Loft007
FEATURE [Part::Loft] Loft008
  Closed = false
  MaxDegree = 5
  Ruled = true
  Sections = -> [Face125,Face141]
  Solid = true
FEATURE [Part::Cut] Cut001002016053006
  Base = -> Loft005
  Tool = -> Loft008
FEATURE [Part::Cut] Cut001002016053007
  Base = -> Cut001002016053006
  Tool = -> Box085159
FEATURE [Part::Box] Box085166  label="Cube247"
  AttacherType = Attacher::AttachEngine3D
  Height = 49
  Length = 53
  Placement = pos=(140,118,0) rot=(-0.707107,0,0.707107;0rad)
  Width = 2
FEATURE [Part::Cylinder] Cylinder071
  Angle = 360
  AttacherType = Attacher::AttachEngine3D
  Height = 19
  Placement = pos=(166,119,24) rot=(1,0,0;1.5708rad)
  Radius = 19
FEATURE [Part::MultiFuse] Fusion004008002002002001007002002026012033  label="SKR Board Duct"
  Placement = pos=(0,0,1) rot=(0,0,1;0rad)
  Shapes = -> [Cut001002016053005,Cut001002016053007,Slice018_child3,Slice018_child0]
FEATURE [Part::MultiFuse] Fusion004008002002002001007002002026012034  label="Duct Mounts"
  Shapes = -> [Fillet005011017082014,Fillet005011017082015]
FEATURE [Part::Chamfer] Chamfer011006003017058  label="Front Tabs"
  Base = -> Fusion004008002002002001007002002026012024
  Edges = 2 edges: [Edge3 r1=2 r2=0.5,Edge29 r1=2 r2=0.5]
FEATURE [Part::Chamfer] Chamfer011006003017059  label="Top Tabs Old"
  Base = -> Fusion004008002002002001007002002026012007
  Edges = 2 edges: [Edge3 r1=3 r2=0.5,Edge29 r1=3 r2=0.5]
FEATURE [Part::MultiFuse] Fusion004008002002002001007002002026012035  label="Drawer Guides"
  Shapes = -> [Fusion004008002002002001007002002026012030,Fusion004008002002002001007002002026012031]
FEATURE [Part::Box] Box085167  label="Cube249"
  AttacherType = Attacher::AttachEngine3D
  Height = 4.35
  Length = 7.8
  Placement = pos=(158.1,0,5.7) rot=(0,0,1;0rad)
  Width = 2
FEATURE [Part::Chamfer] Chamfer011006003017060  label="Mini USB Port"
  Base = -> Box085167
  Edges = 2 edges: [Edge4 r1=1.25 r2=0.5,Edge8 r1=1.25 r2=0.5]
  Placement = pos=(0,0,1) rot=(0,0,1;0rad)
FEATURE [Part::Box] Box085175  label="Cube257"
  AttacherType = Attacher::AttachEngine3D
  Height = 20
  Length = 2.2
  Placement = pos=(189,115.8,14) rot=(0,0,1;0rad)
  Width = 2.2
FEATURE [Part::Box] Box085176  label="Cube258"
  AttacherType = Attacher::AttachEngine3D
  Height = 24
  Length = 4
  Placement = pos=(189,114,10) rot=(0,0,1;0rad)
  Width = 4
FEATURE [Part::Chamfer] Chamfer011006003017061
  Base = -> Box085176
  Edges = 1 edges r=3.99: [Edge9]
FEATURE [Part::Cut] Cut001002016053008
  Base = -> Chamfer011006003017061
  Tool = -> Box085175
FEATURE [Part::Fillet] Fillet005011017082044
  Base = -> Cut001002016053008
  Edges = 1 edges r=2: [Edge8]
  Placement = pos=(-2,0,0) rot=(0,0,1;0rad)
FEATURE [Part::Box] Box085177  label="Cube259"
  AttacherType = Attacher::AttachEngine3D
  Height = 20
  Length = 2.2
  Placement = pos=(144.8,115.8,14) rot=(0,0,1;0rad)
  Width = 2.2
FEATURE [Part::Box] Box085178  label="Cube260"
  AttacherType = Attacher::AttachEngine3D
  Height = 24
  Length = 4
  Placement = pos=(143,114,10) rot=(0,0,1;0rad)
  Width = 4
FEATURE [Part::Chamfer] Chamfer011006003017062
  Base = -> Box085178
  Edges = 1 edges r=3.99: [Edge9]
FEATURE [Part::Cut] Cut001002016053009
  Base = -> Chamfer011006003017062
  Tool = -> Box085177
FEATURE [Part::Fillet] Fillet005011017082045
  Base = -> Cut001002016053009
  Edges = 1 edges r=2: [Edge1]
  Placement = pos=(-2,0,0) rot=(0,0,1;0rad)
FEATURE [Part::MultiFuse] Fusion004008002002002001007002002026012036  label="Duct Mounts001"
  Shapes = -> [Fillet005011017082044,Fillet005011017082045]
FEATURE [Part::Box] Box085179  label="Cube261"
  AttacherType = Attacher::AttachEngine3D
  Height = 19.9
  Length = 2
  Placement = pos=(141.8,120,15.05) rot=(0,0,1;0rad)
  Width = 2
FEATURE [Part::Fillet] Fillet005011017082046
  Base = -> Box085179
  Edges = 2 edges r=1.99: [Edge2,Edge4]
FEATURE [Part::Box] Box085180  label="Cube262"
  AttacherType = Attacher::AttachEngine3D
  Height = 19.9
  Length = 2
  Placement = pos=(188.2,120,15.05) rot=(0,0,1;0rad)
  Width = 2
FEATURE [Part::Fillet] Fillet005011017082047
  Base = -> Box085180
  Edges = 2 edges r=1.99: [Edge6,Edge8]
FEATURE [Part::MultiFuse] Fusion004008002002002001007002002026012037  label="Fan Case Tabs"
  Shapes = -> [Fillet005011017082046,Fillet005011017082047]
FEATURE [Part::Box] Box085181  label="Cube263"
  AttacherType = Attacher::AttachEngine3D
  Height = 20
  Length = 2.2
  Placement = pos=(188.2,119,14.95) rot=(0,0,1;0rad)
  Width = 3.2
FEATURE [Part::Box] Box085182  label="Cube264"
  AttacherType = Attacher::AttachEngine3D
  Height = 24
  Length = 4
  Placement = pos=(188.2,119,10.95) rot=(0,0,1;0rad)
  Width = 5
FEATURE [Part::Box] Box085183  label="Cube265"
  AttacherType = Attacher::AttachEngine3D
  Height = 20
  Length = 2.2
  Placement = pos=(141.6,120,14.95) rot=(0,0,1;0rad)
  Width = 2.2
FEATURE [Part::Box] Box085184  label="Cube266"
  AttacherType = Attacher::AttachEngine3D
  Height = 24
  Length = 4
  Placement = pos=(139.8,120,10.95) rot=(0,0,1;0rad)
  Width = 4
FEATURE [Part::Cut] Cut001002016053010
  Base = -> Box085182
  Tool = -> Box085181
FEATURE [Part::Cut] Cut001002016053011
  Base = -> Box085184
  Tool = -> Box085183
FEATURE [Part::Chamfer] Chamfer011006003017064
  Base = -> Cut001002016053011
  Edges = 1 edges r=3.99: [Edge14]
FEATURE [Part::Fillet] Fillet005011017082048
  Base = -> Chamfer011006003017064
  Edges = 1 edges r=2: [Edge1]
FEATURE [Part::Chamfer] Chamfer011006003017065
  Base = -> Cut001002016053010
  Edges = 1 edges r=4.99: [Edge19]
FEATURE [Part::Fillet] Fillet005011017082049
  Base = -> Chamfer011006003017065
  Edges = 1 edges r=2: [Edge8]
FEATURE [Part::MultiFuse] Fusion004008002002002001007002002026012038  label="Fan Case Mounts"
  Shapes = -> [Fillet005011017082048,Fillet005011017082049]
FEATURE [Part::Chamfer] Chamfer011006003017066  label="Top Tab Holes Old"
  Base = -> Fusion004008002002002001007002002026012005
  Edges = 2 edges: [Edge3 r1=3.49 r2=0.5,Edge15 r1=3.49 r2=0.5]
FEATURE [Part::MultiFuse] Fusion004008002002002001007002002026012039  label="Rail Guides"
  Shapes = -> [Chamfer011006003017009,Chamfer011006003017010]
FEATURE [Part::Box] Box085185  label="Cube267"
  AttacherType = Attacher::AttachEngine3D
  Height = 10
  Length = 10
  Placement = pos=(138,108,93) rot=(0,0,1;0rad)
  Width = 10
FEATURE [Part::Box] Box085186  label="Cube268"
  AttacherType = Attacher::AttachEngine3D
  Height = 45
  Length = 17
  Placement = pos=(162.25,0,26) rot=(0,0,1;0rad)
  Width = 20
FEATURE [App::DocumentObjectGroup] Group012  label="Slicin' Stuff"
  Group = -> [Box085103,Box085104,Box085105,Box085106,Box085107,Box085004,Box083,Cylinder071,Box085186,Box085185,Box085166]
FEATURE [Part::Fillet] Fillet005011012
  Base = -> Box082
  Edges = 1 edges r=1.99: [Edge1]
FEATURE [Part::Chamfer] Chamfer011006003017012
  Base = -> Fillet005011012
  Edges = 1 edges r=1.99: [Edge11]
FEATURE [Part::Chamfer] Chamfer011006003017067  label="SKR Board Recess"
  Base = -> Box009
  Edges = 1 edges r=0.99: [Edge10]
FEATURE [Part::MultiFuse] Fusion004008002002002001007002002026012002  label="All Holes"
  Shapes = -> [Cylinder005,Box013,Box014,Box015,Fusion004008002002,Chamfer005,Chamfer,Box073,Cylinder024,Cylinder041,Fusion004008002002002001007002002015,Fusion004008002002002001007002002026012,Box010,Box085036,Cylinder058,Fusion004008002002002001007002002026012020,Chamfer011006003017060,Chamfer011006003017067]
FEATURE [Part::Cut] Cut001002016026
  Base = -> Cut001002016008
  Tool = -> Fusion004008002002002001007002002026012002
FEATURE [Part::FeaturePython] Slice015  # WARN: FeaturePython — macro-defined, semantics opaque (R4)
  Base = -> Cut001002016026
  Mode = 1
  Tolerance = 0
  Tools = -> [Face032,Face033]
FEATURE [Part::FeaturePython] Slice015_child0  label="Slice015.0"  # WARN: FeaturePython — macro-defined, semantics opaque (R4)
  Base = -> Slice015
  FilterType = 1
  Invert = false
  OverrideMaxVal = 0
  WindowFrom = 80
  WindowTo = 100
  items = 0
FEATURE [Part::FeaturePython] Slice015_child1  label="Slice015.1"  # WARN: FeaturePython — macro-defined, semantics opaque (R4)
  Base = -> Slice015
  FilterType = 1
  Invert = false
  OverrideMaxVal = 0
  WindowFrom = 80
  WindowTo = 100
  items = 1
FEATURE [App::DocumentObjectGroup] GrExplode_Slice015  label="Exploded Slice015"
  Group = -> [Slice015_child1]
FEATURE [Part::FeaturePython] Slice016  # WARN: FeaturePython — macro-defined, semantics opaque (R4)
  Base = -> Slice015_child1
  Mode = 1
  Tolerance = 0
  Tools = -> [Face034]
FEATURE [Part::FeaturePython] Slice016_child0  label="Slice016.0"  # WARN: FeaturePython — macro-defined, semantics opaque (R4)
  Base = -> Slice016
  FilterType = 1
  Invert = false
  OverrideMaxVal = 0
  WindowFrom = 80
  WindowTo = 100
  items = 0
FEATURE [Part::FeaturePython] Slice016_child1  label="Slice016.1"  # WARN: FeaturePython — macro-defined, semantics opaque (R4)
  Base = -> Slice016
  FilterType = 1
  Invert = false
  OverrideMaxVal = 0
  WindowFrom = 80
  WindowTo = 100
  items = 1
FEATURE [Part::FeaturePython] Slice016_child2  label="Slice016.2"  # WARN: FeaturePython — macro-defined, semantics opaque (R4)
  Base = -> Slice016
  FilterType = 1
  Invert = false
  OverrideMaxVal = 0
  WindowFrom = 80
  WindowTo = 100
  items = 2
FEATURE [Part::MultiFuse] Fusion004008002002002001007002002026012040
  Shapes = -> [Fusion,Fusion004008002002002001007002002006,Slice016_child0,Slice017_child0,Chamfer011006003017058,Fusion004008002002002001007002002026012035,Fusion004008002002002001007002002026012039]
FEATURE [Part::Box] Box085187  label="Cube269"
  AttacherType = Attacher::AttachEngine3D
  Height = 2
  Length = 6
  Placement = pos=(8,113,96) rot=(0,0,1;0rad)
  Width = 4
FEATURE [Part::Chamfer] Chamfer011006003017068
  Base = -> Box085187
  Edges = 1 edges r=1.1: [Edge9]
FEATURE [Part::Chamfer] Chamfer011006003017069
  Base = -> Chamfer011006003017068
  Edges = 1 edges: [Edge11 r1=3 r2=1]
FEATURE [Part::Box] Box085188  label="Cube270"
  AttacherType = Attacher::AttachEngine3D
  Height = 2
  Length = 6
  Placement = pos=(64,113,96) rot=(0,0,1;0rad)
  Width = 4
FEATURE [Part::Chamfer] Chamfer011006003017070
  Base = -> Box085188
  Edges = 1 edges r=1.1: [Edge9]
FEATURE [Part::Chamfer] Chamfer011006003017071
  Base = -> Chamfer011006003017070
  Edges = 1 edges: [Edge11 r1=3 r2=1]
FEATURE [Part::Box] Box085189  label="Cube271"
  AttacherType = Attacher::AttachEngine3D
  Height = 2
  Length = 6
  Placement = pos=(123,113,96) rot=(0,0,1;0rad)
  Width = 4
FEATURE [Part::Chamfer] Chamfer011006003017072
  Base = -> Box085189
  Edges = 1 edges r=1.1: [Edge9]
FEATURE [Part::Chamfer] Chamfer011006003017073
  Base = -> Chamfer011006003017072
  Edges = 1 edges: [Edge11 r1=3 r2=1]
FEATURE [Part::Box] Box085190  label="Cube272"
  AttacherType = Attacher::AttachEngine3D
  Height = 2
  Length = 6
  Placement = pos=(179,113,96) rot=(0,0,1;0rad)
  Width = 4
FEATURE [Part::Chamfer] Chamfer011006003017074
  Base = -> Box085190
  Edges = 1 edges r=1.1: [Edge9]
FEATURE [Part::Chamfer] Chamfer011006003017075
  Base = -> Chamfer011006003017074
  Edges = 1 edges: [Edge11 r1=3 r2=1]
FEATURE [Part::Box] Box085191  label="Cube273"
  AttacherType = Attacher::AttachEngine3D
  Height = 2.4
  Length = 6.4
  Placement = pos=(7.8,113,95.8) rot=(0,0,1;0rad)
  Width = 4.2
FEATURE [Part::Chamfer] Chamfer011006003017076
  Base = -> Box085191
  Edges = 1 edges r=1.1: [Edge9]
FEATURE [Part::Chamfer] Chamfer011006003017077
  Base = -> Chamfer011006003017076
  Edges = 1 edges: [Edge11 r1=3 r2=1]
FEATURE [Part::Box] Box085192  label="Cube274"
  AttacherType = Attacher::AttachEngine3D
  Height = 2.4
  Length = 6.4
  Placement = pos=(63.8,113,95.8) rot=(0,0,1;0rad)
  Width = 4.2
FEATURE [Part::Chamfer] Chamfer011006003017079
  Base = -> Box085192
  Edges = 1 edges r=1.1: [Edge9]
FEATURE [Part::Chamfer] Chamfer011006003017078
  Base = -> Chamfer011006003017079
  Edges = 1 edges: [Edge11 r1=3 r2=1]
FEATURE [Part::Box] Box085193  label="Cube275"
  AttacherType = Attacher::AttachEngine3D
  Height = 2.4
  Length = 6.4
  Placement = pos=(122.8,113,95.8) rot=(0,0,1;0rad)
  Width = 4.2
FEATURE [Part::Chamfer] Chamfer011006003017081
  Base = -> Box085193
  Edges = 1 edges r=1.1: [Edge9]
FEATURE [Part::Chamfer] Chamfer011006003017080
  Base = -> Chamfer011006003017081
  Edges = 1 edges: [Edge11 r1=3 r2=1]
FEATURE [Part::Box] Box085194  label="Cube276"
  AttacherType = Attacher::AttachEngine3D
  Height = 2.4
  Length = 6.4
  Placement = pos=(178.8,113,95.8) rot=(0,0,1;0rad)
  Width = 4.2
FEATURE [Part::Chamfer] Chamfer011006003017083
  Base = -> Box085194
  Edges = 1 edges r=1.1: [Edge9]
FEATURE [Part::Chamfer] Chamfer011006003017082
  Base = -> Chamfer011006003017083
  Edges = 1 edges: [Edge11 r1=3 r2=1]
FEATURE [Part::MultiFuse] Fusion004008002002002001007002002026012041
  Shapes = -> [Chamfer011006003017077,Chamfer011006003017078,Chamfer011006003017080,Chamfer011006003017082]
FEATURE [Part::MultiFuse] Fusion004008002002002001007002002026012042
  Shapes = -> [Chamfer011006003017075,Chamfer011006003017073,Chamfer011006003017071,Chamfer011006003017069]
FEATURE [Part::Fillet] Fillet005011017082051  label="Top Tabs"
  Base = -> Fusion004008002002002001007002002026012042
  Edges = 8 edges r=1: [Edge1,Edge7,Edge19,Edge25,Edge37,Edge43,Edge55,Edge61]
FEATURE [Part::Fillet] Fillet005011017082052  label="Top Tab Holes"
  Base = -> Fusion004008002002002001007002002026012041
  Edges = 8 edges r=1: [Edge1,Edge7,Edge19,Edge25,Edge37,Edge43,Edge55,Edge61]
FEATURE [App::DocumentObjectGroup] Group  label="Holes"
  Group = -> [Box012,Cylinder017,Fusion004008003,Box009,Box085167,Fusion004008002002002001007002002026012008,Fillet005011017082052]
FEATURE [Part::Fillet] Fillet005011017082053
  Base = -> Fusion004008002002002001007002002026012040
  Edges = 2 edges r=1.49: [Edge848,Edge855]
FEATURE [Part::Fillet] Fillet005011017082054
  Base = -> Fillet005011017082053
  Edges = 8 edges r=1: [Edge1079,Edge1080,Edge1081,Edge1082,Edge1084,Edge1085,Edge1086,Edge1087]
FEATURE [Part::Box] Box085170  label="Cube252"
  AttacherType = Attacher::AttachEngine3D
  Height = 44.4
  Length = 44.4
  Placement = pos=(143.8,120,2.8) rot=(0,0,1;0rad)
  Width = 14.4
FEATURE [Part::Box] Box085171  label="Cube253"
  AttacherType = Attacher::AttachEngine3D
  Height = 40.4
  Length = 40.4
  Placement = pos=(145.8,120,4.8) rot=(0,0,1;0rad)
  Width = 12.4
FEATURE [Part::Box] Box085172  label="Cube254"
  AttacherType = Attacher::AttachEngine3D
  Height = 44.8
  Length = 24
  Placement = pos=(154,120,2.8) rot=(0,0,1;0rad)
  Width = 12
FEATURE [Part::FeaturePython] Slice020  # WARN: FeaturePython — macro-defined, semantics opaque (R4)
  Base = -> Box085170
  Mode = 1
  Tolerance = 0
  Tools = -> [Box085171,Box085172,Fusion004008003,Cylinder058]
FEATURE [Part::FeaturePython] Slice020_child0  label="Slice020.0"  # WARN: FeaturePython — macro-defined, semantics opaque (R4)
  Base = -> Slice020
  FilterType = 1
  Invert = false
  OverrideMaxVal = 0
  WindowFrom = 80
  WindowTo = 100
  items = 0
FEATURE [Part::FeaturePython] Slice020_child1  label="Slice020.1"  # WARN: FeaturePython — macro-defined, semantics opaque (R4)
  Base = -> Slice020
  FilterType = 1
  Invert = false
  OverrideMaxVal = 0
  WindowFrom = 80
  WindowTo = 100
  items = 1
FEATURE [Part::FeaturePython] Slice020_child2  label="Slice020.2"  # WARN: FeaturePython — macro-defined, semantics opaque (R4)
  Base = -> Slice020
  FilterType = 1
  Invert = false
  OverrideMaxVal = 0
  WindowFrom = 80
  WindowTo = 100
  items = 2
FEATURE [Part::FeaturePython] Slice020_child3  label="Slice020.3"  # WARN: FeaturePython — macro-defined, semantics opaque (R4)
  Base = -> Slice020
  FilterType = 1
  Invert = false
  OverrideMaxVal = 0
  WindowFrom = 80
  WindowTo = 100
  items = 3
FEATURE [Part::FeaturePython] Slice020_child4  label="Slice020.4"  # WARN: FeaturePython — macro-defined, semantics opaque (R4)
  Base = -> Slice020
  FilterType = 1
  Invert = false
  OverrideMaxVal = 0
  WindowFrom = 80
  WindowTo = 100
  items = 4
FEATURE [Part::FeaturePython] Slice020_child5  label="Slice020.5"  # WARN: FeaturePython — macro-defined, semantics opaque (R4)
  Base = -> Slice020
  FilterType = 1
  Invert = false
  OverrideMaxVal = 0
  WindowFrom = 80
  WindowTo = 100
  items = 5
FEATURE [Part::FeaturePython] Slice020_child6  label="Slice020.6"  # WARN: FeaturePython — macro-defined, semantics opaque (R4)
  Base = -> Slice020
  FilterType = 1
  Invert = false
  OverrideMaxVal = 0
  WindowFrom = 80
  WindowTo = 100
  items = 6
FEATURE [Part::FeaturePython] Slice020_child7  label="Slice020.7"  # WARN: FeaturePython — macro-defined, semantics opaque (R4)
  Base = -> Slice020
  FilterType = 1
  Invert = false
  OverrideMaxVal = 0
  WindowFrom = 80
  WindowTo = 100
  items = 7
FEATURE [Part::FeaturePython] Slice020_child8  label="Slice020.8"  # WARN: FeaturePython — macro-defined, semantics opaque (R4)
  Base = -> Slice020
  FilterType = 1
  Invert = false
  OverrideMaxVal = 0
  WindowFrom = 80
  WindowTo = 100
  items = 8
FEATURE [Part::FeaturePython] Slice020_child9  label="Slice020.9"  # WARN: FeaturePython — macro-defined, semantics opaque (R4)
  Base = -> Slice020
  FilterType = 1
  Invert = false
  OverrideMaxVal = 0
  WindowFrom = 80
  WindowTo = 100
  items = 9
FEATURE [Part::FeaturePython] Slice020_child10  label="Slice020.10"  # WARN: FeaturePython — macro-defined, semantics opaque (R4)
  Base = -> Slice020
  FilterType = 1
  Invert = false
  OverrideMaxVal = 0
  WindowFrom = 80
  WindowTo = 100
  items = 10
FEATURE [Part::FeaturePython] Slice020_child11  label="Slice020.11"  # WARN: FeaturePython — macro-defined, semantics opaque (R4)
  Base = -> Slice020
  FilterType = 1
  Invert = false
  OverrideMaxVal = 0
  WindowFrom = 80
  WindowTo = 100
  items = 11
FEATURE [Part::FeaturePython] Slice020_child12  label="Slice020.12"  # WARN: FeaturePython — macro-defined, semantics opaque (R4)
  Base = -> Slice020
  FilterType = 1
  Invert = false
  OverrideMaxVal = 0
  WindowFrom = 80
  WindowTo = 100
  items = 12
FEATURE [Part::FeaturePython] Slice020_child13  label="Slice020.13"  # WARN: FeaturePython — macro-defined, semantics opaque (R4)
  Base = -> Slice020
  FilterType = 1
  Invert = false
  OverrideMaxVal = 0
  WindowFrom = 80
  WindowTo = 100
  items = 13
FEATURE [Part::FeaturePython] Slice020_child14  label="Slice020.14"  # WARN: FeaturePython — macro-defined, semantics opaque (R4)
  Base = -> Slice020
  FilterType = 1
  Invert = false
  OverrideMaxVal = 0
  WindowFrom = 80
  WindowTo = 100
  items = 14
FEATURE [Part::FeaturePython] Slice020_child15  label="Slice020.15"  # WARN: FeaturePython — macro-defined, semantics opaque (R4)
  Base = -> Slice020
  FilterType = 1
  Invert = false
  OverrideMaxVal = 0
  WindowFrom = 80
  WindowTo = 100
  items = 15
FEATURE [Part::FeaturePython] Slice020_child16  label="Slice020.16"  # WARN: FeaturePython — macro-defined, semantics opaque (R4)
  Base = -> Slice020
  FilterType = 1
  Invert = false
  OverrideMaxVal = 0
  WindowFrom = 80
  WindowTo = 100
  items = 16
FEATURE [App::DocumentObjectGroup] GrExplode_Slice020  label="Exploded Slice020"
  Group = -> [Slice020_child0,Slice020_child1,Slice020_child2,Slice020_child3,Slice020_child4,Slice020_child5,Slice020_child6,Slice020_child7,Slice020_child8,Slice020_child9,Slice020_child10,Slice020_child11,Slice020_child12,Slice020_child13,Slice020_child14,Slice020_child15,Slice020_child16]
FEATURE [Part::Fillet] Fillet005011017082055
  Base = -> Slice020_child0
  Edges = 12 edges r=1.99: [Edge2,Edge3,Edge4,Edge12,Edge13,Edge15,Edge17,Edge18,Edge19,Edge25,Edge27,Edge29]
FEATURE [Part::Fillet] Fillet005011017082056  label="Fan Case 12mm Thickness"
  Base = -> Fillet005011017082055
  Edges = 1 edges r=1: [Edge70]
FEATURE [Part::Box] Box085195  label="Cube277"
  AttacherType = Attacher::AttachEngine3D
  Height = 44.4
  Length = 44.4
  Placement = pos=(143.8,120,2.8) rot=(0,0,1;0rad)
  Width = 13.4
FEATURE [Part::Box] Box085196  label="Cube278"
  AttacherType = Attacher::AttachEngine3D
  Height = 40.4
  Length = 40.4
  Placement = pos=(145.8,120,4.8) rot=(0,0,1;0rad)
  Width = 11.4
FEATURE [Part::Box] Box085197  label="Cube279"
  AttacherType = Attacher::AttachEngine3D
  Height = 44.8
  Length = 24
  Placement = pos=(154,120,2.8) rot=(0,0,1;0rad)
  Width = 11
FEATURE [Part::FeaturePython] Slice021  # WARN: FeaturePython — macro-defined, semantics opaque (R4)
  Base = -> Box085195
  Mode = 1
  Tolerance = 0
  Tools = -> [Box085196,Box085197,Cylinder058,Fusion004008003]
FEATURE [Part::FeaturePython] Slice021_child0  label="Slice021.0"  # WARN: FeaturePython — macro-defined, semantics opaque (R4)
  Base = -> Slice021
  FilterType = 1
  Invert = false
  OverrideMaxVal = 0
  WindowFrom = 80
  WindowTo = 100
  items = 0
FEATURE [Part::FeaturePython] Slice021_child1  label="Slice021.1"  # WARN: FeaturePython — macro-defined, semantics opaque (R4)
  Base = -> Slice021
  FilterType = 1
  Invert = false
  OverrideMaxVal = 0
  WindowFrom = 80
  WindowTo = 100
  items = 1
FEATURE [Part::FeaturePython] Slice021_child2  label="Slice021.2"  # WARN: FeaturePython — macro-defined, semantics opaque (R4)
  Base = -> Slice021
  FilterType = 1
  Invert = false
  OverrideMaxVal = 0
  WindowFrom = 80
  WindowTo = 100
  items = 2
FEATURE [Part::FeaturePython] Slice021_child3  label="Slice021.3"  # WARN: FeaturePython — macro-defined, semantics opaque (R4)
  Base = -> Slice021
  FilterType = 1
  Invert = false
  OverrideMaxVal = 0
  WindowFrom = 80
  WindowTo = 100
  items = 3
FEATURE [Part::FeaturePython] Slice021_child4  label="Slice021.4"  # WARN: FeaturePython — macro-defined, semantics opaque (R4)
  Base = -> Slice021
  FilterType = 1
  Invert = false
  OverrideMaxVal = 0
  WindowFrom = 80
  WindowTo = 100
  items = 4
FEATURE [Part::FeaturePython] Slice021_child5  label="Slice021.5"  # WARN: FeaturePython — macro-defined, semantics opaque (R4)
  Base = -> Slice021
  FilterType = 1
  Invert = false
  OverrideMaxVal = 0
  WindowFrom = 80
  WindowTo = 100
  items = 5
FEATURE [Part::FeaturePython] Slice021_child6  label="Slice021.6"  # WARN: FeaturePython — macro-defined, semantics opaque (R4)
  Base = -> Slice021
  FilterType = 1
  Invert = false
  OverrideMaxVal = 0
  WindowFrom = 80
  WindowTo = 100
  items = 6
FEATURE [Part::FeaturePython] Slice021_child7  label="Slice021.7"  # WARN: FeaturePython — macro-defined, semantics opaque (R4)
  Base = -> Slice021
  FilterType = 1
  Invert = false
  OverrideMaxVal = 0
  WindowFrom = 80
  WindowTo = 100
  items = 7
FEATURE [Part::FeaturePython] Slice021_child8  label="Slice021.8"  # WARN: FeaturePython — macro-defined, semantics opaque (R4)
  Base = -> Slice021
  FilterType = 1
  Invert = false
  OverrideMaxVal = 0
  WindowFrom = 80
  WindowTo = 100
  items = 8
FEATURE [Part::FeaturePython] Slice021_child9  label="Slice021.9"  # WARN: FeaturePython — macro-defined, semantics opaque (R4)
  Base = -> Slice021
  FilterType = 1
  Invert = false
  OverrideMaxVal = 0
  WindowFrom = 80
  WindowTo = 100
  items = 9
FEATURE [Part::FeaturePython] Slice021_child10  label="Slice021.10"  # WARN: FeaturePython — macro-defined, semantics opaque (R4)
  Base = -> Slice021
  FilterType = 1
  Invert = false
  OverrideMaxVal = 0
  WindowFrom = 80
  WindowTo = 100
  items = 10
FEATURE [Part::FeaturePython] Slice021_child11  label="Slice021.11"  # WARN: FeaturePython — macro-defined, semantics opaque (R4)
  Base = -> Slice021
  FilterType = 1
  Invert = false
  OverrideMaxVal = 0
  WindowFrom = 80
  WindowTo = 100
  items = 11
FEATURE [Part::FeaturePython] Slice021_child12  label="Slice021.12"  # WARN: FeaturePython — macro-defined, semantics opaque (R4)
  Base = -> Slice021
  FilterType = 1
  Invert = false
  OverrideMaxVal = 0
  WindowFrom = 80
  WindowTo = 100
  items = 12
FEATURE [App::DocumentObjectGroup] GrExplode_Slice021  label="Exploded Slice021"
  Group = -> [Slice021_child0,Slice021_child1,Slice021_child2,Slice021_child3,Slice021_child4,Slice021_child5,Slice021_child6,Slice021_child7,Slice021_child8,Slice021_child9,Slice021_child10,Slice021_child11,Slice021_child12]
FEATURE [App::DocumentObjectGroup] Group010  label="Old Slices"
  Group = -> [GrExplode_Slice001,GrExplode_Slice002,Chamfer011004,Chamfer011005,GrExplode_Slice016,GrExplode_Slice015,GrExplode_Slice017,Chamfer011006003017013,Chamfer011006003017014,GrExplode_Slice018,GrExplode_Slice020,GrExplode_Slice021]
FEATURE [Part::Fillet] Fillet005011017082057
  Base = -> Slice021_child0
  Edges = 12 edges r=1.99: [Edge2,Edge3,Edge4,Edge12,Edge13,Edge15,Edge17,Edge18,Edge19,Edge25,Edge27,Edge29]
FEATURE [Part::Fillet] Fillet005011017082058  label="Fan Case 11mm Thickness Old"
  Base = -> Fillet005011017082057
  Edges = 1 edges r=1: [Edge70]
FEATURE [App::DocumentObjectGroup] Group013  label="Fan Cases"
  Group = -> [Fusion004008002002002001007002002026012037,Fillet005011017082056,Fillet005011017082058]
FEATURE [Part::Box] Box085198  label="Cube280"
  AttacherType = Attacher::AttachEngine3D
  Height = 44.5
  Length = 189
  Placement = pos=(2,112,53.5) rot=(0,0,1;0rad)
  Width = 10
FEATURE [Part::Box] Box085199  label="Cube281"
  AttacherType = Attacher::AttachEngine3D
  Height = 10
  Length = 3
  Placement = pos=(-1,112,53.5) rot=(0,0,1;0rad)
  Width = 10
FEATURE [Part::Box] Box085200  label="Cube282"
  AttacherType = Attacher::AttachEngine3D
  Height = 10
  Length = 3
  Placement = pos=(191,112,53.5) rot=(0,0,1;0rad)
  Width = 10
FEATURE [Part::MultiFuse] Fusion004008002002002001007002002026012043  label="Bottom Cutter"
  Shapes = -> [Box085198,Box085199,Box085200]
FEATURE [Part::Chamfer] Chamfer011006003017084
  Base = -> Box078
  Edges = 1 edges r=1.99: [Edge8]
FEATURE [Part::Chamfer] Chamfer011006003017085
  Base = -> Box079
  Edges = 1 edges r=1.99: [Edge4]
FEATURE [Part::MultiFuse] Fusion004008002002002001007002002026012004  label="Rails"
  Shapes = -> [Chamfer011006003017012,Chamfer011006003017002,Chamfer006,Chamfer007,Chamfer008,Chamfer009,Chamfer011006003017084,Chamfer011006003017085]
FEATURE [Part::Cut] Cut001002016053012  label="Cut Rails"
  Base = -> Fusion004008002002002001007002002026012004
  Tool = -> Fusion004008002002002001007002002026012025
FEATURE [Part::MultiFuse] Fusion004008002002002001007002002026012026
  Shapes = -> [Slice016_child1,Slice016_child2,Fusion004008002002002001007002002026012038,Fusion004008002002002001007002002026012034,Slice015_child0,Cut001002016053012]
FEATURE [Part::Feature] Shell
  shape: bbox 195 x 10 x 34.5 mm, 5 faces, 0 solids (baked)
FEATURE [Part::FeaturePython] Slice022  # WARN: FeaturePython — macro-defined, semantics opaque (R4)
  Base = -> Fusion004008002002002001007002002026012026
  Mode = 1
  Tolerance = 0
  Tools = -> [Shell]
FEATURE [Part::FeaturePython] Slice022_child0  label="Slice022.0"  # WARN: FeaturePython — macro-defined, semantics opaque (R4)
  Base = -> Slice022
  FilterType = 1
  Invert = false
  OverrideMaxVal = 0
  WindowFrom = 80
  WindowTo = 100
  items = 0
FEATURE [Part::FeaturePython] Slice022_child1  label="Slice022.1"  # WARN: FeaturePython — macro-defined, semantics opaque (R4)
  Base = -> Slice022
  FilterType = 1
  Invert = false
  OverrideMaxVal = 0
  WindowFrom = 80
  WindowTo = 100
  items = 1
FEATURE [Part::Fillet] Fillet005011017082060
  Base = -> Slice022_child1
  Edges = 2 edges r=1: [Edge6,Edge32]
FEATURE [Part::Cylinder] Cylinder072
  Angle = 360
  AttacherType = Attacher::AttachEngine3D
  Height = 99
  Placement = pos=(47,116,98) rot=(0,1,0;1.5708rad)
  Radius = 0.9
FEATURE [Part::Cylinder] Cylinder073
  Angle = 360
  AttacherType = Attacher::AttachEngine3D
  Height = 189
  Placement = pos=(2,116,98) rot=(0,1,0;1.5708rad)
  Radius = 1
FEATURE [Part::Box] Box085201  label="Cube283"
  AttacherType = Attacher::AttachEngine3D
  Height = 26
  Length = 3
  Placement = pos=(8,118,18) rot=(0,0,1;0rad)
  Width = 2
FEATURE [Part::Cylinder] Cylinder075
  Angle = 360
  AttacherType = Attacher::AttachEngine3D
  Height = 10
  Placement = pos=(118,124,75) rot=(-1,0,0;1.5708rad)
  Radius = 3.2
FEATURE [Part::Cylinder] Cylinder074
  Angle = 360
  AttacherType = Attacher::AttachEngine3D
  Height = 10
  Placement = pos=(75,124,75) rot=(-1,0,0;1.5708rad)
  Radius = 3.2
FEATURE [Part::Chamfer] Chamfer011006003017086
  Base = -> Slice022_child0
  Edges = 1 edges r=1: [Edge666]
FEATURE [Part::Fillet] Fillet005011017082061
  Base = -> Cylinder072
  Edges = 2 edges r=0.5: [Edge1,Edge3]
FEATURE [Part::MultiFuse] Fusion004008002002002001007002002026012044
  Shapes = -> [Fillet005011017082060,Fillet005011017082054,Fillet005011017082061]
FEATURE [App::DocumentObjectGroup] Group003  label="Top"
  Group = -> [Fusion004008002002002001007002002026012019,Fusion004008002002002001007002002026012021,Slice022_child1,Fusion004008002002002001007002002026012044,Cylinder072]
FEATURE [Part::Box] Box085202  label="Cube284"
  AttacherType = Attacher::AttachEngine3D
  Height = 2
  Length = 6
  Placement = pos=(14,8,0) rot=(0,0,1;0rad)
  Width = 71
FEATURE [Part::Box] Box085203  label="Cube285"
  AttacherType = Attacher::AttachEngine3D
  Height = 2
  Length = 6
  Placement = pos=(23,8,0) rot=(0,0,1;0rad)
  Width = 71
FEATURE [Part::Box] Box085204  label="Cube286"
  AttacherType = Attacher::AttachEngine3D
  Height = 2
  Length = 6
  Placement = pos=(32,8,0) rot=(0,0,1;0rad)
  Width = 71
FEATURE [Part::Box] Box085205  label="Cube287"
  AttacherType = Attacher::AttachEngine3D
  Height = 2
  Length = 6
  Placement = pos=(41,8,0) rot=(0,0,1;0rad)
  Width = 71
FEATURE [Part::Box] Box085206  label="Cube288"
  AttacherType = Attacher::AttachEngine3D
  Height = 2
  Length = 15
  Placement = pos=(23,82,0) rot=(0,0,1;0rad)
  Width = 25
FEATURE [Part::Box] Box085207  label="Cube289"
  AttacherType = Attacher::AttachEngine3D
  Height = 2
  Length = 6
  Placement = pos=(127,8,0) rot=(0,0,1;0rad)
  Width = 53
FEATURE [Part::Box] Box085208  label="Cube290"
  AttacherType = Attacher::AttachEngine3D
  Height = 2
  Length = 6
  Placement = pos=(127,73,0) rot=(0,0,1;0rad)
  Width = 20
FEATURE [Part::Box] Box085209  label="Cube291"
  AttacherType = Attacher::AttachEngine3D
  Height = 2
  Length = 6
  Placement = pos=(136,8,0) rot=(0,0,1;0rad)
  Width = 53
FEATURE [Part::Box] Box085210  label="Cube292"
  AttacherType = Attacher::AttachEngine3D
  Height = 2
  Length = 6
  Placement = pos=(145,8,0) rot=(0,0,1;0rad)
  Width = 53
FEATURE [Part::Box] Box085211  label="Cube293"
  AttacherType = Attacher::AttachEngine3D
  Height = 2
  Length = 6
  Placement = pos=(154,8,0) rot=(0,0,1;0rad)
  Width = 53
FEATURE [Part::Box] Box085212  label="Cube294"
  AttacherType = Attacher::AttachEngine3D
  Height = 2
  Length = 6
  Placement = pos=(163,8,0) rot=(0,0,1;0rad)
  Width = 53
FEATURE [Part::Box] Box085213  label="Cube295"
  AttacherType = Attacher::AttachEngine3D
  Height = 2
  Length = 6
  Placement = pos=(172,8,0) rot=(0,0,1;0rad)
  Width = 53
FEATURE [Part::Box] Box085214  label="Cube296"
  AttacherType = Attacher::AttachEngine3D
  Height = 2
  Length = 6
  Placement = pos=(136,73,0) rot=(0,0,1;0rad)
  Width = 20
FEATURE [Part::Box] Box085215  label="Cube297"
  AttacherType = Attacher::AttachEngine3D
  Height = 2
  Length = 6
  Placement = pos=(145,73,0) rot=(0,0,1;0rad)
  Width = 20
FEATURE [Part::Box] Box085216  label="Cube298"
  AttacherType = Attacher::AttachEngine3D
  Height = 2
  Length = 6
  Placement = pos=(154,73,0) rot=(0,0,1;0rad)
  Width = 20
FEATURE [Part::Box] Box085217  label="Cube299"
  AttacherType = Attacher::AttachEngine3D
  Height = 2
  Length = 6
  Placement = pos=(163,73,0) rot=(0,0,1;0rad)
  Width = 20
FEATURE [Part::Box] Box085218  label="Cube300"
  AttacherType = Attacher::AttachEngine3D
  Height = 2
  Length = 6
  Placement = pos=(172,73,0) rot=(0,0,1;0rad)
  Width = 20
FEATURE [Part::MultiFuse] Fusion004008002002002001007002002026012046  label="Raspberrry Pi Vents"
  Shapes = -> [Box085202,Box085203,Box085204,Box085205,Box085206]
FEATURE [Part::MultiFuse] Fusion004008002002002001007002002026012047  label="SKR Mini E3 Vents"
  Shapes = -> [Box085207,Box085208,Box085209,Box085210,Box085211,Box085212,Box085213,Box085214,Box085215,Box085216,Box085217,Box085218]
FEATURE [Part::Fillet] Fillet005011017082062
  Base = -> Box085201
  Edges = 4 edges r=1.49: [Edge2,Edge4,Edge6,Edge8]
FEATURE [Part::Box] Box085219  label="Cube301"
  AttacherType = Attacher::AttachEngine3D
  Height = 26
  Length = 3
  Placement = pos=(13,118,18) rot=(0,0,1;0rad)
  Width = 2
FEATURE [Part::Fillet] Fillet005011017082063
  Base = -> Box085219
  Edges = 4 edges r=1.49: [Edge2,Edge4,Edge6,Edge8]
FEATURE [Part::Box] Box085220  label="Cube302"
  AttacherType = Attacher::AttachEngine3D
  Height = 26
  Length = 3
  Placement = pos=(18,118,18) rot=(0,0,1;0rad)
  Width = 2
FEATURE [Part::Fillet] Fillet005011017082064
  Base = -> Box085220
  Edges = 4 edges r=1.49: [Edge2,Edge4,Edge6,Edge8]
FEATURE [Part::Box] Box085221  label="Cube303"
  AttacherType = Attacher::AttachEngine3D
  Height = 26
  Length = 3
  Placement = pos=(23,118,18) rot=(0,0,1;0rad)
  Width = 2
FEATURE [Part::Fillet] Fillet005011017082065
  Base = -> Box085221
  Edges = 4 edges r=1.49: [Edge2,Edge4,Edge6,Edge8]
FEATURE [Part::Box] Box085222  label="Cube304"
  AttacherType = Attacher::AttachEngine3D
  Height = 18
  Length = 3
  Placement = pos=(28,118,6) rot=(0,0,1;0rad)
  Width = 2
FEATURE [Part::Fillet] Fillet005011017082066
  Base = -> Box085222
  Edges = 4 edges r=1.49: [Edge2,Edge4,Edge6,Edge8]
FEATURE [Part::Box] Box085223  label="Cube305"
  AttacherType = Attacher::AttachEngine3D
  Height = 18
  Length = 3
  Placement = pos=(33,118,6) rot=(0,0,1;0rad)
  Width = 2
FEATURE [Part::Fillet] Fillet005011017082067
  Base = -> Box085223
  Edges = 4 edges r=1.49: [Edge2,Edge4,Edge6,Edge8]
FEATURE [Part::Box] Box085224  label="Cube306"
  AttacherType = Attacher::AttachEngine3D
  Height = 18
  Length = 3
  Placement = pos=(43,118,6) rot=(0,0,1;0rad)
  Width = 2
FEATURE [Part::Fillet] Fillet005011017082069
  Base = -> Box085224
  Edges = 4 edges r=1.49: [Edge2,Edge4,Edge6,Edge8]
FEATURE [Part::Box] Box085225  label="Cube307"
  AttacherType = Attacher::AttachEngine3D
  Height = 18
  Length = 3
  Placement = pos=(38,118,6) rot=(0,0,1;0rad)
  Width = 2
FEATURE [Part::Fillet] Fillet005011017082068
  Base = -> Box085225
  Edges = 4 edges r=1.49: [Edge2,Edge4,Edge6,Edge8]
FEATURE [Part::Box] Box085226  label="Cube308"
  AttacherType = Attacher::AttachEngine3D
  Height = 18
  Length = 3
  Placement = pos=(53,118,6) rot=(0,0,1;0rad)
  Width = 2
FEATURE [Part::Fillet] Fillet005011017082071
  Base = -> Box085226
  Edges = 4 edges r=1.49: [Edge2,Edge4,Edge6,Edge8]
FEATURE [Part::Box] Box085227  label="Cube309"
  AttacherType = Attacher::AttachEngine3D
  Height = 18
  Length = 3
  Placement = pos=(48,118,6) rot=(0,0,1;0rad)
  Width = 2
FEATURE [Part::Fillet] Fillet005011017082070
  Base = -> Box085227
  Edges = 4 edges r=1.49: [Edge2,Edge4,Edge6,Edge8]
FEATURE [Part::Box] Box085228  label="Cube310"
  AttacherType = Attacher::AttachEngine3D
  Height = 18
  Length = 3
  Placement = pos=(63,118,6) rot=(0,0,1;0rad)
  Width = 2
FEATURE [Part::Box] Box085229  label="Cube311"
  AttacherType = Attacher::AttachEngine3D
  Height = 18
  Length = 3
  Placement = pos=(58,118,6) rot=(0,0,1;0rad)
  Width = 2
FEATURE [Part::Fillet] Fillet005011017082072
  Base = -> Box085229
  Edges = 4 edges r=1.49: [Edge2,Edge4,Edge6,Edge8]
FEATURE [Part::Fillet] Fillet005011017082073
  Base = -> Box085228
  Edges = 4 edges r=1.49: [Edge2,Edge4,Edge6,Edge8]
FEATURE [Part::Box] Box085230  label="Cube312"
  AttacherType = Attacher::AttachEngine3D
  Height = 18
  Length = 3
  Placement = pos=(93,118,6) rot=(0,0,1;0rad)
  Width = 2
FEATURE [Part::Box] Box085231  label="Cube313"
  AttacherType = Attacher::AttachEngine3D
  Height = 18
  Length = 3
  Placement = pos=(98,118,6) rot=(0,0,1;0rad)
  Width = 2
FEATURE [Part::Fillet] Fillet005011017082074
  Base = -> Box085231
  Edges = 4 edges r=1.49: [Edge2,Edge4,Edge6,Edge8]
FEATURE [Part::Box] Box085232  label="Cube314"
  AttacherType = Attacher::AttachEngine3D
  Height = 18
  Length = 3
  Placement = pos=(68,118,6) rot=(0,0,1;0rad)
  Width = 2
FEATURE [Part::Fillet] Fillet005011017082076
  Base = -> Box085232
  Edges = 4 edges r=1.49: [Edge2,Edge4,Edge6,Edge8]
FEATURE [Part::Box] Box085233  label="Cube315"
  AttacherType = Attacher::AttachEngine3D
  Height = 18
  Length = 3
  Placement = pos=(73,118,6) rot=(0,0,1;0rad)
  Width = 2
FEATURE [Part::Fillet] Fillet005011017082075
  Base = -> Box085233
  Edges = 4 edges r=1.49: [Edge2,Edge4,Edge6,Edge8]
FEATURE [Part::Box] Box085234  label="Cube316"
  AttacherType = Attacher::AttachEngine3D
  Height = 18
  Length = 3
  Placement = pos=(88,118,6) rot=(0,0,1;0rad)
  Width = 2
FEATURE [Part::Box] Box085235  label="Cube317"
  AttacherType = Attacher::AttachEngine3D
  Height = 18
  Length = 3
  Placement = pos=(83,118,6) rot=(0,0,1;0rad)
  Width = 2
FEATURE [Part::Box] Box085236  label="Cube318"
  AttacherType = Attacher::AttachEngine3D
  Height = 18
  Length = 3
  Placement = pos=(78,118,6) rot=(0,0,1;0rad)
  Width = 2
FEATURE [Part::Box] Box085237  label="Cube319"
  AttacherType = Attacher::AttachEngine3D
  Height = 18
  Length = 3
  Placement = pos=(103,118,6) rot=(0,0,1;0rad)
  Width = 2
FEATURE [Part::Fillet] Fillet005011017082077
  Base = -> Box085237
  Edges = 4 edges r=1.49: [Edge2,Edge4,Edge6,Edge8]
FEATURE [Part::Fillet] Fillet005011017082078
  Base = -> Box085234
  Edges = 4 edges r=1.49: [Edge2,Edge4,Edge6,Edge8]
FEATURE [Part::Fillet] Fillet005011017082079
  Base = -> Box085236
  Edges = 4 edges r=1.49: [Edge2,Edge4,Edge6,Edge8]
FEATURE [Part::Fillet] Fillet005011017082080
  Base = -> Box085235
  Edges = 4 edges r=1.49: [Edge2,Edge4,Edge6,Edge8]
FEATURE [Part::Fillet] Fillet005011017082081
  Base = -> Box085230
  Edges = 4 edges r=1.49: [Edge2,Edge4,Edge6,Edge8]
FEATURE [Part::Box] Box085238  label="Cube320"
  AttacherType = Attacher::AttachEngine3D
  Height = 18
  Length = 3
  Placement = pos=(108,118,6) rot=(0,0,1;0rad)
  Width = 2
FEATURE [Part::Fillet] Fillet005011017082082
  Base = -> Box085238
  Edges = 4 edges r=1.49: [Edge2,Edge4,Edge6,Edge8]
FEATURE [Part::Box] Box085239  label="Cube321"
  AttacherType = Attacher::AttachEngine3D
  Height = 18
  Length = 3
  Placement = pos=(53,118,26) rot=(0,0,1;0rad)
  Width = 2
FEATURE [Part::Box] Box085240  label="Cube322"
  AttacherType = Attacher::AttachEngine3D
  Height = 18
  Length = 3
  Placement = pos=(88,118,26) rot=(0,0,1;0rad)
  Width = 2
FEATURE [Part::Box] Box085241  label="Cube323"
  AttacherType = Attacher::AttachEngine3D
  Height = 18
  Length = 3
  Placement = pos=(93,118,26) rot=(0,0,1;0rad)
  Width = 2
FEATURE [Part::Fillet] Fillet005011017082083
  Base = -> Box085241
  Edges = 4 edges r=1.49: [Edge2,Edge4,Edge6,Edge8]
FEATURE [Part::Box] Box085242  label="Cube324"
  AttacherType = Attacher::AttachEngine3D
  Height = 18
  Length = 3
  Placement = pos=(83,118,26) rot=(0,0,1;0rad)
  Width = 2
FEATURE [Part::Box] Box085243  label="Cube325"
  AttacherType = Attacher::AttachEngine3D
  Height = 18
  Length = 3
  Placement = pos=(73,118,26) rot=(0,0,1;0rad)
  Width = 2
FEATURE [Part::Box] Box085244  label="Cube326"
  AttacherType = Attacher::AttachEngine3D
  Height = 18
  Length = 3
  Placement = pos=(58,118,26) rot=(0,0,1;0rad)
  Width = 2
FEATURE [Part::Fillet] Fillet005011017082084
  Base = -> Box085244
  Edges = 4 edges r=1.49: [Edge2,Edge4,Edge6,Edge8]
FEATURE [Part::Box] Box085245  label="Cube327"
  AttacherType = Attacher::AttachEngine3D
  Height = 18
  Length = 3
  Placement = pos=(78,118,26) rot=(0,0,1;0rad)
  Width = 2
FEATURE [Part::Fillet] Fillet005011017082085
  Base = -> Box085245
  Edges = 4 edges r=1.49: [Edge2,Edge4,Edge6,Edge8]
FEATURE [Part::Box] Box085246  label="Cube328"
  AttacherType = Attacher::AttachEngine3D
  Height = 18
  Length = 3
  Placement = pos=(103,118,26) rot=(0,0,1;0rad)
  Width = 2
FEATURE [Part::Box] Box085247  label="Cube329"
  AttacherType = Attacher::AttachEngine3D
  Height = 18
  Length = 3
  Placement = pos=(28,118,26) rot=(0,0,1;0rad)
  Width = 2
FEATURE [Part::Fillet] Fillet005011017082087
  Base = -> Box085247
  Edges = 4 edges r=1.49: [Edge2,Edge4,Edge6,Edge8]
FEATURE [Part::Box] Box085248  label="Cube330"
  AttacherType = Attacher::AttachEngine3D
  Height = 18
  Length = 3
  Placement = pos=(108,118,26) rot=(0,0,1;0rad)
  Width = 2
FEATURE [Part::Box] Box085249  label="Cube331"
  AttacherType = Attacher::AttachEngine3D
  Height = 18
  Length = 3
  Placement = pos=(33,118,26) rot=(0,0,1;0rad)
  Width = 2
FEATURE [Part::Fillet] Fillet005011017082086
  Base = -> Box085249
  Edges = 4 edges r=1.49: [Edge2,Edge4,Edge6,Edge8]
FEATURE [Part::Box] Box085250  label="Cube332"
  AttacherType = Attacher::AttachEngine3D
  Height = 18
  Length = 3
  Placement = pos=(48,118,26) rot=(0,0,1;0rad)
  Width = 2
FEATURE [Part::Box] Box085251  label="Cube333"
  AttacherType = Attacher::AttachEngine3D
  Height = 18
  Length = 3
  Placement = pos=(43,118,26) rot=(0,0,1;0rad)
  Width = 2
FEATURE [Part::Box] Box085252  label="Cube334"
  AttacherType = Attacher::AttachEngine3D
  Height = 18
  Length = 3
  Placement = pos=(38,118,26) rot=(0,0,1;0rad)
  Width = 2
FEATURE [Part::Box] Box085253  label="Cube335"
  AttacherType = Attacher::AttachEngine3D
  Height = 18
  Length = 3
  Placement = pos=(63,118,26) rot=(0,0,1;0rad)
  Width = 2
FEATURE [Part::Fillet] Fillet005011017082088
  Base = -> Box085253
  Edges = 4 edges r=1.49: [Edge2,Edge4,Edge6,Edge8]
FEATURE [Part::Fillet] Fillet005011017082090
  Base = -> Box085250
  Edges = 4 edges r=1.49: [Edge2,Edge4,Edge6,Edge8]
FEATURE [Part::Box] Box085254  label="Cube336"
  AttacherType = Attacher::AttachEngine3D
  Height = 18
  Length = 3
  Placement = pos=(98,118,26) rot=(0,0,1;0rad)
  Width = 2
FEATURE [Part::Fillet] Fillet005011017082089
  Base = -> Box085254
  Edges = 4 edges r=1.49: [Edge2,Edge4,Edge6,Edge8]
FEATURE [Part::Box] Box085255  label="Cube337"
  AttacherType = Attacher::AttachEngine3D
  Height = 18
  Length = 3
  Placement = pos=(68,118,26) rot=(0,0,1;0rad)
  Width = 2
FEATURE [Part::Fillet] Fillet005011017082091
  Base = -> Box085248
  Edges = 4 edges r=1.49: [Edge2,Edge4,Edge6,Edge8]
FEATURE [Part::Fillet] Fillet005011017082092
  Base = -> Box085240
  Edges = 4 edges r=1.49: [Edge2,Edge4,Edge6,Edge8]
FEATURE [Part::Fillet] Fillet005011017082093
  Base = -> Box085242
  Edges = 4 edges r=1.49: [Edge2,Edge4,Edge6,Edge8]
FEATURE [Part::Fillet] Fillet005011017082094
  Base = -> Box085252
  Edges = 4 edges r=1.49: [Edge2,Edge4,Edge6,Edge8]
FEATURE [Part::Fillet] Fillet005011017082095
  Base = -> Box085251
  Edges = 4 edges r=1.49: [Edge2,Edge4,Edge6,Edge8]
FEATURE [Part::Fillet] Fillet005011017082096
  Base = -> Box085239
  Edges = 4 edges r=1.49: [Edge2,Edge4,Edge6,Edge8]
FEATURE [Part::Fillet] Fillet005011017082097
  Base = -> Box085243
  Edges = 4 edges r=1.49: [Edge2,Edge4,Edge6,Edge8]
FEATURE [Part::Fillet] Fillet005011017082098
  Base = -> Box085255
  Edges = 4 edges r=1.49: [Edge2,Edge4,Edge6,Edge8]
FEATURE [Part::Fillet] Fillet005011017082099
  Base = -> Box085246
  Edges = 4 edges r=1.49: [Edge2,Edge4,Edge6,Edge8]
FEATURE [Part::MultiFuse] Fusion004008002002002001007002002026012048  label="Rear Vents"
  Shapes = -> [Fillet005011017082062,Fillet005011017082063,Fillet005011017082064,Fillet005011017082065,Fillet005011017082066,Fillet005011017082067,Fillet005011017082068,Fillet005011017082069,Fillet005011017082070,Fillet005011017082071,Fillet005011017082072,Fillet005011017082073,Fillet005011017082074,Fillet005011017082075,Fillet005011017082076,Fillet005011017082077,Fillet005011017082078,Fillet005011017082079,+20 more]
FEATURE [Part::Box] Box085256  label="Cube338"
  AttacherType = Attacher::AttachEngine3D
  Height = 36
  Length = 16
  Placement = pos=(116,118,7) rot=(0,0,1;0rad)
  Width = 10
FEATURE [Part::Fillet] Fillet005011017082100  label="Rear Cable Hole"
  Base = -> Box085256
  Edges = 4 edges r=6: [Edge2,Edge4,Edge6,Edge8]
FEATURE [Part::FeaturePython] Slice023  # WARN: FeaturePython — macro-defined, semantics opaque (R4)
  Base = -> Chamfer011006003017086
  Mode = 1
  Tolerance = 0
  Tools = -> [Cylinder073,Fusion004008002002002001007002002026012046,Fusion004008002002002001007002002026012047,Fusion004008002002002001007002002026012048,Fillet005011017082100]
FEATURE [Part::FeaturePython] Slice023_child0  label="Slice023.0"  # WARN: FeaturePython — macro-defined, semantics opaque (R4)
  Base = -> Slice023
  FilterType = 1
  Invert = false
  OverrideMaxVal = 0
  WindowFrom = 80
  WindowTo = 100
  items = 0
FEATURE [Part::FeaturePython] Slice023_child1  label="Slice023.1"  # WARN: FeaturePython — macro-defined, semantics opaque (R4)
  Base = -> Slice023
  FilterType = 1
  Invert = false
  OverrideMaxVal = 0
  WindowFrom = 80
  WindowTo = 100
  items = 1
FEATURE [Part::FeaturePython] Slice023_child2  label="Slice023.2"  # WARN: FeaturePython — macro-defined, semantics opaque (R4)
  Base = -> Slice023
  FilterType = 1
  Invert = false
  OverrideMaxVal = 0
  WindowFrom = 80
  WindowTo = 100
  items = 2
FEATURE [Part::FeaturePython] Slice023_child3  label="Slice023.3"  # WARN: FeaturePython — macro-defined, semantics opaque (R4)
  Base = -> Slice023
  FilterType = 1
  Invert = false
  OverrideMaxVal = 0
  WindowFrom = 80
  WindowTo = 100
  items = 3
FEATURE [Part::FeaturePython] Slice023_child4  label="Slice023.4"  # WARN: FeaturePython — macro-defined, semantics opaque (R4)
  Base = -> Slice023
  FilterType = 1
  Invert = false
  OverrideMaxVal = 0
  WindowFrom = 80
  WindowTo = 100
  items = 4
FEATURE [Part::FeaturePython] Slice023_child5  label="Slice023.5"  # WARN: FeaturePython — macro-defined, semantics opaque (R4)
  Base = -> Slice023
  FilterType = 1
  Invert = false
  OverrideMaxVal = 0
  WindowFrom = 80
  WindowTo = 100
  items = 5
FEATURE [Part::FeaturePython] Slice023_child6  label="Slice023.6"  # WARN: FeaturePython — macro-defined, semantics opaque (R4)
  Base = -> Slice023
  FilterType = 1
  Invert = false
  OverrideMaxVal = 0
  WindowFrom = 80
  WindowTo = 100
  items = 6
FEATURE [Part::FeaturePython] Slice023_child7  label="Slice023.7"  # WARN: FeaturePython — macro-defined, semantics opaque (R4)
  Base = -> Slice023
  FilterType = 1
  Invert = false
  OverrideMaxVal = 0
  WindowFrom = 80
  WindowTo = 100
  items = 7
FEATURE [Part::FeaturePython] Slice023_child8  label="Slice023.8"  # WARN: FeaturePython — macro-defined, semantics opaque (R4)
  Base = -> Slice023
  FilterType = 1
  Invert = false
  OverrideMaxVal = 0
  WindowFrom = 80
  WindowTo = 100
  items = 8
FEATURE [Part::FeaturePython] Slice023_child9  label="Slice023.9"  # WARN: FeaturePython — macro-defined, semantics opaque (R4)
  Base = -> Slice023
  FilterType = 1
  Invert = false
  OverrideMaxVal = 0
  WindowFrom = 80
  WindowTo = 100
  items = 9
FEATURE [Part::FeaturePython] Slice023_child10  label="Slice023.10"  # WARN: FeaturePython — macro-defined, semantics opaque (R4)
  Base = -> Slice023
  FilterType = 1
  Invert = false
  OverrideMaxVal = 0
  WindowFrom = 80
  WindowTo = 100
  items = 10
FEATURE [Part::FeaturePython] Slice023_child11  label="Slice023.11"  # WARN: FeaturePython — macro-defined, semantics opaque (R4)
  Base = -> Slice023
  FilterType = 1
  Invert = false
  OverrideMaxVal = 0
  WindowFrom = 80
  WindowTo = 100
  items = 11
FEATURE [Part::FeaturePython] Slice023_child12  label="Slice023.12"  # WARN: FeaturePython — macro-defined, semantics opaque (R4)
  Base = -> Slice023
  FilterType = 1
  Invert = false
  OverrideMaxVal = 0
  WindowFrom = 80
  WindowTo = 100
  items = 12
FEATURE [Part::FeaturePython] Slice023_child13  label="Slice023.13"  # WARN: FeaturePython — macro-defined, semantics opaque (R4)
  Base = -> Slice023
  FilterType = 1
  Invert = false
  OverrideMaxVal = 0
  WindowFrom = 80
  WindowTo = 100
  items = 13
FEATURE [Part::FeaturePython] Slice023_child14  label="Slice023.14"  # WARN: FeaturePython — macro-defined, semantics opaque (R4)
  Base = -> Slice023
  FilterType = 1
  Invert = false
  OverrideMaxVal = 0
  WindowFrom = 80
  WindowTo = 100
  items = 14
FEATURE [Part::FeaturePython] Slice023_child15  label="Slice023.15"  # WARN: FeaturePython — macro-defined, semantics opaque (R4)
  Base = -> Slice023
  FilterType = 1
  Invert = false
  OverrideMaxVal = 0
  WindowFrom = 80
  WindowTo = 100
  items = 15
FEATURE [Part::FeaturePython] Slice023_child16  label="Slice023.16"  # WARN: FeaturePython — macro-defined, semantics opaque (R4)
  Base = -> Slice023
  FilterType = 1
  Invert = false
  OverrideMaxVal = 0
  WindowFrom = 80
  WindowTo = 100
  items = 16
FEATURE [Part::FeaturePython] Slice023_child17  label="Slice023.17"  # WARN: FeaturePython — macro-defined, semantics opaque (R4)
  Base = -> Slice023
  FilterType = 1
  Invert = false
  OverrideMaxVal = 0
  WindowFrom = 80
  WindowTo = 100
  items = 17
FEATURE [Part::FeaturePython] Slice023_child18  label="Slice023.18"  # WARN: FeaturePython — macro-defined, semantics opaque (R4)
  Base = -> Slice023
  FilterType = 1
  Invert = false
  OverrideMaxVal = 0
  WindowFrom = 80
  WindowTo = 100
  items = 18
FEATURE [Part::FeaturePython] Slice023_child19  label="Slice023.19"  # WARN: FeaturePython — macro-defined, semantics opaque (R4)
  Base = -> Slice023
  FilterType = 1
  Invert = false
  OverrideMaxVal = 0
  WindowFrom = 80
  WindowTo = 100
  items = 19
FEATURE [Part::FeaturePython] Slice023_child20  label="Slice023.20"  # WARN: FeaturePython — macro-defined, semantics opaque (R4)
  Base = -> Slice023
  FilterType = 1
  Invert = false
  OverrideMaxVal = 0
  WindowFrom = 80
  WindowTo = 100
  items = 20
FEATURE [Part::FeaturePython] Slice023_child21  label="Slice023.21"  # WARN: FeaturePython — macro-defined, semantics opaque (R4)
  Base = -> Slice023
  FilterType = 1
  Invert = false
  OverrideMaxVal = 0
  WindowFrom = 80
  WindowTo = 100
  items = 21
FEATURE [Part::FeaturePython] Slice023_child22  label="Slice023.22"  # WARN: FeaturePython — macro-defined, semantics opaque (R4)
  Base = -> Slice023
  FilterType = 1
  Invert = false
  OverrideMaxVal = 0
  WindowFrom = 80
  WindowTo = 100
  items = 22
FEATURE [Part::FeaturePython] Slice023_child23  label="Slice023.23"  # WARN: FeaturePython — macro-defined, semantics opaque (R4)
  Base = -> Slice023
  FilterType = 1
  Invert = false
  OverrideMaxVal = 0
  WindowFrom = 80
  WindowTo = 100
  items = 23
FEATURE [Part::FeaturePython] Slice023_child24  label="Slice023.24"  # WARN: FeaturePython — macro-defined, semantics opaque (R4)
  Base = -> Slice023
  FilterType = 1
  Invert = false
  OverrideMaxVal = 0
  WindowFrom = 80
  WindowTo = 100
  items = 24
FEATURE [Part::FeaturePython] Slice023_child25  label="Slice023.25"  # WARN: FeaturePython — macro-defined, semantics opaque (R4)
  Base = -> Slice023
  FilterType = 1
  Invert = false
  OverrideMaxVal = 0
  WindowFrom = 80
  WindowTo = 100
  items = 25
FEATURE [Part::FeaturePython] Slice023_child26  label="Slice023.26"  # WARN: FeaturePython — macro-defined, semantics opaque (R4)
  Base = -> Slice023
  FilterType = 1
  Invert = false
  OverrideMaxVal = 0
  WindowFrom = 80
  WindowTo = 100
  items = 26
FEATURE [Part::FeaturePython] Slice023_child27  label="Slice023.27"  # WARN: FeaturePython — macro-defined, semantics opaque (R4)
  Base = -> Slice023
  FilterType = 1
  Invert = false
  OverrideMaxVal = 0
  WindowFrom = 80
  WindowTo = 100
  items = 27
FEATURE [Part::FeaturePython] Slice023_child28  label="Slice023.28"  # WARN: FeaturePython — macro-defined, semantics opaque (R4)
  Base = -> Slice023
  FilterType = 1
  Invert = false
  OverrideMaxVal = 0
  WindowFrom = 80
  WindowTo = 100
  items = 28
FEATURE [Part::FeaturePython] Slice023_child29  label="Slice023.29"  # WARN: FeaturePython — macro-defined, semantics opaque (R4)
  Base = -> Slice023
  FilterType = 1
  Invert = false
  OverrideMaxVal = 0
  WindowFrom = 80
  WindowTo = 100
  items = 29
FEATURE [Part::FeaturePython] Slice023_child30  label="Slice023.30"  # WARN: FeaturePython — macro-defined, semantics opaque (R4)
  Base = -> Slice023
  FilterType = 1
  Invert = false
  OverrideMaxVal = 0
  WindowFrom = 80
  WindowTo = 100
  items = 30
FEATURE [Part::FeaturePython] Slice023_child31  label="Slice023.31"  # WARN: FeaturePython — macro-defined, semantics opaque (R4)
  Base = -> Slice023
  FilterType = 1
  Invert = false
  OverrideMaxVal = 0
  WindowFrom = 80
  WindowTo = 100
  items = 31
FEATURE [Part::FeaturePython] Slice023_child32  label="Slice023.32"  # WARN: FeaturePython — macro-defined, semantics opaque (R4)
  Base = -> Slice023
  FilterType = 1
  Invert = false
  OverrideMaxVal = 0
  WindowFrom = 80
  WindowTo = 100
  items = 32
FEATURE [Part::FeaturePython] Slice023_child33  label="Slice023.33"  # WARN: FeaturePython — macro-defined, semantics opaque (R4)
  Base = -> Slice023
  FilterType = 1
  Invert = false
  OverrideMaxVal = 0
  WindowFrom = 80
  WindowTo = 100
  items = 33
FEATURE [Part::FeaturePython] Slice023_child34  label="Slice023.34"  # WARN: FeaturePython — macro-defined, semantics opaque (R4)
  Base = -> Slice023
  FilterType = 1
  Invert = false
  OverrideMaxVal = 0
  WindowFrom = 80
  WindowTo = 100
  items = 34
FEATURE [Part::FeaturePython] Slice023_child35  label="Slice023.35"  # WARN: FeaturePython — macro-defined, semantics opaque (R4)
  Base = -> Slice023
  FilterType = 1
  Invert = false
  OverrideMaxVal = 0
  WindowFrom = 80
  WindowTo = 100
  items = 35
FEATURE [Part::FeaturePython] Slice023_child36  label="Slice023.36"  # WARN: FeaturePython — macro-defined, semantics opaque (R4)
  Base = -> Slice023
  FilterType = 1
  Invert = false
  OverrideMaxVal = 0
  WindowFrom = 80
  WindowTo = 100
  items = 36
FEATURE [Part::FeaturePython] Slice023_child37  label="Slice023.37"  # WARN: FeaturePython — macro-defined, semantics opaque (R4)
  Base = -> Slice023
  FilterType = 1
  Invert = false
  OverrideMaxVal = 0
  WindowFrom = 80
  WindowTo = 100
  items = 37
FEATURE [Part::FeaturePython] Slice023_child38  label="Slice023.38"  # WARN: FeaturePython — macro-defined, semantics opaque (R4)
  Base = -> Slice023
  FilterType = 1
  Invert = false
  OverrideMaxVal = 0
  WindowFrom = 80
  WindowTo = 100
  items = 38
FEATURE [Part::FeaturePython] Slice023_child39  label="Slice023.39"  # WARN: FeaturePython — macro-defined, semantics opaque (R4)
  Base = -> Slice023
  FilterType = 1
  Invert = false
  OverrideMaxVal = 0
  WindowFrom = 80
  WindowTo = 100
  items = 39
FEATURE [Part::FeaturePython] Slice023_child40  label="Slice023.40"  # WARN: FeaturePython — macro-defined, semantics opaque (R4)
  Base = -> Slice023
  FilterType = 1
  Invert = false
  OverrideMaxVal = 0
  WindowFrom = 80
  WindowTo = 100
  items = 40
FEATURE [Part::FeaturePython] Slice023_child41  label="Slice023.41"  # WARN: FeaturePython — macro-defined, semantics opaque (R4)
  Base = -> Slice023
  FilterType = 1
  Invert = false
  OverrideMaxVal = 0
  WindowFrom = 80
  WindowTo = 100
  items = 41
FEATURE [Part::FeaturePython] Slice023_child42  label="Slice023.42"  # WARN: FeaturePython — macro-defined, semantics opaque (R4)
  Base = -> Slice023
  FilterType = 1
  Invert = false
  OverrideMaxVal = 0
  WindowFrom = 80
  WindowTo = 100
  items = 42
FEATURE [Part::FeaturePython] Slice023_child43  label="Slice023.43"  # WARN: FeaturePython — macro-defined, semantics opaque (R4)
  Base = -> Slice023
  FilterType = 1
  Invert = false
  OverrideMaxVal = 0
  WindowFrom = 80
  WindowTo = 100
  items = 43
FEATURE [Part::FeaturePython] Slice023_child44  label="Slice023.44"  # WARN: FeaturePython — macro-defined, semantics opaque (R4)
  Base = -> Slice023
  FilterType = 1
  Invert = false
  OverrideMaxVal = 0
  WindowFrom = 80
  WindowTo = 100
  items = 44
FEATURE [Part::FeaturePython] Slice023_child45  label="Slice023.45"  # WARN: FeaturePython — macro-defined, semantics opaque (R4)
  Base = -> Slice023
  FilterType = 1
  Invert = false
  OverrideMaxVal = 0
  WindowFrom = 80
  WindowTo = 100
  items = 45
FEATURE [Part::FeaturePython] Slice023_child46  label="Slice023.46"  # WARN: FeaturePython — macro-defined, semantics opaque (R4)
  Base = -> Slice023
  FilterType = 1
  Invert = false
  OverrideMaxVal = 0
  WindowFrom = 80
  WindowTo = 100
  items = 46
FEATURE [Part::FeaturePython] Slice023_child47  label="Slice023.47"  # WARN: FeaturePython — macro-defined, semantics opaque (R4)
  Base = -> Slice023
  FilterType = 1
  Invert = false
  OverrideMaxVal = 0
  WindowFrom = 80
  WindowTo = 100
  items = 47
FEATURE [Part::FeaturePython] Slice023_child48  label="Slice023.48"  # WARN: FeaturePython — macro-defined, semantics opaque (R4)
  Base = -> Slice023
  FilterType = 1
  Invert = false
  OverrideMaxVal = 0
  WindowFrom = 80
  WindowTo = 100
  items = 48
FEATURE [Part::FeaturePython] Slice023_child49  label="Slice023.49"  # WARN: FeaturePython — macro-defined, semantics opaque (R4)
  Base = -> Slice023
  FilterType = 1
  Invert = false
  OverrideMaxVal = 0
  WindowFrom = 80
  WindowTo = 100
  items = 49
FEATURE [Part::FeaturePython] Slice023_child50  label="Slice023.50"  # WARN: FeaturePython — macro-defined, semantics opaque (R4)
  Base = -> Slice023
  FilterType = 1
  Invert = false
  OverrideMaxVal = 0
  WindowFrom = 80
  WindowTo = 100
  items = 50
FEATURE [Part::FeaturePython] Slice023_child51  label="Slice023.51"  # WARN: FeaturePython — macro-defined, semantics opaque (R4)
  Base = -> Slice023
  FilterType = 1
  Invert = false
  OverrideMaxVal = 0
  WindowFrom = 80
  WindowTo = 100
  items = 51
FEATURE [Part::FeaturePython] Slice023_child52  label="Slice023.52"  # WARN: FeaturePython — macro-defined, semantics opaque (R4)
  Base = -> Slice023
  FilterType = 1
  Invert = false
  OverrideMaxVal = 0
  WindowFrom = 80
  WindowTo = 100
  items = 52
FEATURE [Part::FeaturePython] Slice023_child53  label="Slice023.53"  # WARN: FeaturePython — macro-defined, semantics opaque (R4)
  Base = -> Slice023
  FilterType = 1
  Invert = false
  OverrideMaxVal = 0
  WindowFrom = 80
  WindowTo = 100
  items = 53
FEATURE [Part::FeaturePython] Slice023_child54  label="Slice023.54"  # WARN: FeaturePython — macro-defined, semantics opaque (R4)
  Base = -> Slice023
  FilterType = 1
  Invert = false
  OverrideMaxVal = 0
  WindowFrom = 80
  WindowTo = 100
  items = 54
FEATURE [Part::FeaturePython] Slice023_child55  label="Slice023.55"  # WARN: FeaturePython — macro-defined, semantics opaque (R4)
  Base = -> Slice023
  FilterType = 1
  Invert = false
  OverrideMaxVal = 0
  WindowFrom = 80
  WindowTo = 100
  items = 55
FEATURE [Part::FeaturePython] Slice023_child56  label="Slice023.56"  # WARN: FeaturePython — macro-defined, semantics opaque (R4)
  Base = -> Slice023
  FilterType = 1
  Invert = false
  OverrideMaxVal = 0
  WindowFrom = 80
  WindowTo = 100
  items = 56
FEATURE [Part::FeaturePython] Slice023_child57  label="Slice023.57"  # WARN: FeaturePython — macro-defined, semantics opaque (R4)
  Base = -> Slice023
  FilterType = 1
  Invert = false
  OverrideMaxVal = 0
  WindowFrom = 80
  WindowTo = 100
  items = 57
FEATURE [App::DocumentObjectGroup] GrExplode_Slice023  label="Exploded Slice023"
  Group = -> [Slice023_child1,Slice023_child2,Slice023_child3,Slice023_child4,Slice023_child5,Slice023_child6,Slice023_child7,Slice023_child8,Slice023_child9,Slice023_child10,Slice023_child11,Slice023_child12,Slice023_child13,Slice023_child14,Slice023_child15,Slice023_child16,Slice023_child17,Slice023_child18,Slice023_child19,Slice023_child20,Slice023_child21,Slice023_child22,Slice023_child23,Slice023_child24,+33 more]
FEATURE [Part::Box] Box085257  label="Cube339"
  AttacherType = Attacher::AttachEngine3D
  Height = 53
  Length = 60
  Placement = pos=(66.5,124.5,45) rot=(0,0,1;0rad)
  Width = 33.4
FEATURE [Part::Box] Box085258  label="Cube340"
  AttacherType = Attacher::AttachEngine3D
  Height = 53
  Length = 60
  Placement = pos=(66.5,127.5,48) rot=(0,0,1;0rad)
  Width = 50
FEATURE [Part::Box] Box085259  label="Cube341"
  AttacherType = Attacher::AttachEngine3D
  Height = 44.8
  Length = 19.7
  Placement = pos=(86.65,122,49.2) rot=(0,0,1;0rad)
  Width = 2.5
FEATURE [Part::Box] Box085260  label="Cube342"
  AttacherType = Attacher::AttachEngine3D
  Height = 44.8
  Length = 24.1
  Placement = pos=(84.45,120,49.2) rot=(0,0,1;0rad)
  Width = 2.1
FEATURE [Part::Box] Box085261  label="Cube343"
  AttacherType = Attacher::AttachEngine3D
  Height = 45
  Length = 2.2
  Placement = pos=(106.5,120,48.95) rot=(0,0,1;0rad)
  Width = 2.2
FEATURE [Part::Box] Box085262  label="Cube344"
  AttacherType = Attacher::AttachEngine3D
  Height = 49
  Length = 4
  Placement = pos=(106.5,120,44.95) rot=(0,0,1;0rad)
  Width = 4
FEATURE [Part::Box] Box085263  label="Cube345"
  AttacherType = Attacher::AttachEngine3D
  Height = 45
  Length = 2.2
  Placement = pos=(84.3,120,48.95) rot=(0,0,1;0rad)
  Width = 2.2
FEATURE [Part::Box] Box085264  label="Cube346"
  AttacherType = Attacher::AttachEngine3D
  Height = 49
  Length = 4
  Placement = pos=(82.5,120,44.95) rot=(0,0,1;0rad)
  Width = 4
FEATURE [Part::Cut] Cut001002016053013
  Base = -> Box085262
  Tool = -> Box085261
FEATURE [Part::Cut] Cut001002016053014
  Base = -> Box085264
  Tool = -> Box085263
FEATURE [Part::Chamfer] Chamfer011006003017087
  Base = -> Cut001002016053014
  Edges = 1 edges r=3.99: [Edge14]
FEATURE [Part::Fillet] Fillet005011017082101
  Base = -> Chamfer011006003017087
  Edges = 1 edges r=2: [Edge1]
FEATURE [Part::Chamfer] Chamfer011006003017088
  Base = -> Cut001002016053013
  Edges = 1 edges r=2.99: [Edge19]
FEATURE [Part::Fillet] Fillet005011017082102
  Base = -> Chamfer011006003017088
  Edges = 1 edges r=2: [Edge8]
FEATURE [Part::Cylinder] Cylinder076
  Angle = 360
  AttacherType = Attacher::AttachEngine3D
  Height = 10
  Placement = pos=(75,142.4,38) rot=(0,0,1;1.5708rad)
  Radius = 3.2
FEATURE [Part::Cylinder] Cylinder077
  Angle = 360
  AttacherType = Attacher::AttachEngine3D
  Height = 10
  Placement = pos=(118,142.4,38) rot=(0,0,1;1.5708rad)
  Radius = 3.2
FEATURE [Part::MultiFuse] Fusion004008002002002001007002002026012045  label="Mounting Screw Holes"
  Shapes = -> [Cylinder074,Cylinder075,Cylinder076,Cylinder077]
FEATURE [Part::FeaturePython] Slice024  # WARN: FeaturePython — macro-defined, semantics opaque (R4)
  Base = -> Box085257
  Mode = 1
  Tolerance = 0
  Tools = -> [Box085258,Fusion004008002002002001007002002026012045]
FEATURE [Part::FeaturePython] Slice024_child0  label="Slice024.0"  # WARN: FeaturePython — macro-defined, semantics opaque (R4)
  Base = -> Slice024
  FilterType = 1
  Invert = false
  OverrideMaxVal = 0
  WindowFrom = 80
  WindowTo = 100
  items = 0
FEATURE [Part::FeaturePython] Slice024_child1  label="Slice024.1"  # WARN: FeaturePython — macro-defined, semantics opaque (R4)
  Base = -> Slice024
  FilterType = 1
  Invert = false
  OverrideMaxVal = 0
  WindowFrom = 80
  WindowTo = 100
  items = 1
FEATURE [Part::FeaturePython] Slice024_child2  label="Slice024.2"  # WARN: FeaturePython — macro-defined, semantics opaque (R4)
  Base = -> Slice024
  FilterType = 1
  Invert = false
  OverrideMaxVal = 0
  WindowFrom = 80
  WindowTo = 100
  items = 2
FEATURE [Part::FeaturePython] Slice024_child3  label="Slice024.3"  # WARN: FeaturePython — macro-defined, semantics opaque (R4)
  Base = -> Slice024
  FilterType = 1
  Invert = false
  OverrideMaxVal = 0
  WindowFrom = 80
  WindowTo = 100
  items = 3
FEATURE [Part::FeaturePython] Slice024_child4  label="Slice024.4"  # WARN: FeaturePython — macro-defined, semantics opaque (R4)
  Base = -> Slice024
  FilterType = 1
  Invert = false
  OverrideMaxVal = 0
  WindowFrom = 80
  WindowTo = 100
  items = 4
FEATURE [Part::FeaturePython] Slice024_child5  label="Slice024.5"  # WARN: FeaturePython — macro-defined, semantics opaque (R4)
  Base = -> Slice024
  FilterType = 1
  Invert = false
  OverrideMaxVal = 0
  WindowFrom = 80
  WindowTo = 100
  items = 5
FEATURE [App::DocumentObjectGroup] GrExplode_Slice024  label="Exploded Slice024"
  Group = -> [Slice024_child1,Slice024_child2,Slice024_child3,Slice024_child4,Slice024_child5]
FEATURE [Part::MultiFuse] Fusion004008002002002001007002002026012050
  Shapes = -> [Slice024_child0,Box085260,Box085259]
FEATURE [Part::Box] Box085265  label="Cube347"
  AttacherType = Attacher::AttachEngine3D
  Height = 36
  Length = 124
  Placement = pos=(69,124,45) rot=(0,0,1;0rad)
  Width = 3
FEATURE [Part::Box] Box085266  label="Cube348"
  AttacherType = Attacher::AttachEngine3D
  Height = 3
  Length = 124
  Placement = pos=(69,127,45) rot=(0,0,1;0rad)
  Width = 3
FEATURE [Part::Box] Box085267  label="Cube349"
  AttacherType = Attacher::AttachEngine3D
  Height = 15
  Length = 40
  Placement = pos=(76.5,119.5,79) rot=(0,0,1;0rad)
  Width = 33.4
FEATURE [Part::Cylinder] Cylinder078
  Angle = 360
  AttacherType = Attacher::AttachEngine3D
  Height = 10
  Placement = pos=(75,124,75) rot=(-1,0,0;1.5708rad)
  Radius = 1.75
FEATURE [Part::Cylinder] Cylinder079
  Angle = 360
  AttacherType = Attacher::AttachEngine3D
  Height = 10
  Placement = pos=(118,124,75) rot=(-1,0,0;1.5708rad)
  Radius = 1.75
FEATURE [Part::FeaturePython] Slice027  # WARN: FeaturePython — macro-defined, semantics opaque (R4)
  Base = -> Box085265
  Mode = 1
  Tolerance = 0
  Tools = -> [Cylinder078,Cylinder079]
FEATURE [Part::FeaturePython] Slice027_child0  label="Slice027.0"  # WARN: FeaturePython — macro-defined, semantics opaque (R4)
  Base = -> Slice027
  FilterType = 1
  Invert = false
  OverrideMaxVal = 0
  WindowFrom = 80
  WindowTo = 100
  items = 0
FEATURE [Part::FeaturePython] Slice027_child1  label="Slice027.1"  # WARN: FeaturePython — macro-defined, semantics opaque (R4)
  Base = -> Slice027
  FilterType = 1
  Invert = false
  OverrideMaxVal = 0
  WindowFrom = 80
  WindowTo = 100
  items = 1
FEATURE [Part::FeaturePython] Slice027_child2  label="Slice027.2"  # WARN: FeaturePython — macro-defined, semantics opaque (R4)
  Base = -> Slice027
  FilterType = 1
  Invert = false
  OverrideMaxVal = 0
  WindowFrom = 80
  WindowTo = 100
  items = 2
FEATURE [Part::MultiFuse] Fusion004008002002002001007002002026012051
  Shapes = -> [Slice027_child0,Box085266]
FEATURE [App::DocumentObjectGroup] GrExplode_Slice027  label="Exploded Slice027"
  Group = -> [Slice027_child1,Slice027_child2,Fusion004008002002002001007002002026012051]
FEATURE [Part::Fillet] Fillet005011017082106  label="Enclosure Mount Screw Hole Finder"
  Base = -> Fusion004008002002002001007002002026012051
  Edges = 4 edges r=2: [Edge2,Edge5,Edge12,Edge15]
FEATURE [Part::Box] Box085268  label="Cube350"
  AttacherType = Attacher::AttachEngine3D
  Height = 25
  Length = 10
  Placement = pos=(6,120,58) rot=(0,0,1;0rad)
  Width = 7.5
FEATURE [Part::Chamfer] Chamfer011006003017090
  Base = -> Box085268
  Edges = 1 edges r=7.49: [Edge11]
FEATURE [Part::Box] Box085269  label="Cube351"
  AttacherType = Attacher::AttachEngine3D
  Height = 25
  Length = 10
  Placement = pos=(177,120,58) rot=(0,0,1;0rad)
  Width = 7.5
FEATURE [Part::Chamfer] Chamfer011006003017091
  Base = -> Box085269
  Edges = 1 edges r=7.49: [Edge11]
FEATURE [Part::MultiFuse] Fusion004008002002002001007002002026012049  label="Box Mounts"
  Shapes = -> [Fillet005011017082101,Fillet005011017082102]
FEATURE [Part::Compound] Compound
  Links = -> [Slice023_child0,Fusion004008002002002001007002002018,Fusion003,Fusion002,Fusion004008002002002001007002002026012049,Chamfer011006003017090,Chamfer011006003017091]
FEATURE [App::DocumentObjectGroup] Group004  label="Bottom"
  Group = -> [Group002,Fusion004008002002002001007002002018,Fusion004008002002002001007002002026012026,Fusion004008002002002001007002002026012033,Group013,Fusion004008002002002001007002002026012043,Slice022_child0,Cylinder010,Slice023_child0,Compound]
FEATURE [Part::Box] Box085270  label="Cube352"
  AttacherType = Attacher::AttachEngine3D
  Height = 53
  Length = 60
  Placement = pos=(66.5,127.5,48) rot=(0,0,1;0rad)
  Width = 50
FEATURE [Part::Box] Box085271  label="Cube353"
  AttacherType = Attacher::AttachEngine3D
  Height = 44.8
  Length = 19.4
  Placement = pos=(86.8,122,49.2) rot=(0,0,1;0rad)
  Width = 2.5
FEATURE [Part::Box] Box085272  label="Cube354"
  AttacherType = Attacher::AttachEngine3D
  Height = 53
  Length = 60
  Placement = pos=(66.5,124.5,45) rot=(0,0,1;0rad)
  Width = 33.4
FEATURE [Part::Box] Box085273  label="Cube355"
  AttacherType = Attacher::AttachEngine3D
  Height = 44.8
  Length = 23.8
  Placement = pos=(84.6,120.1,49.2) rot=(0,0,1;0rad)
  Width = 1.9
FEATURE [Part::Cylinder] Cylinder080
  Angle = 360
  AttacherType = Attacher::AttachEngine3D
  Height = 10
  Placement = pos=(75,142.4,38) rot=(0,0,1;1.5708rad)
  Radius = 3.2
FEATURE [Part::Cylinder] Cylinder081
  Angle = 360
  AttacherType = Attacher::AttachEngine3D
  Height = 10
  Placement = pos=(118,142.4,38) rot=(0,0,1;1.5708rad)
  Radius = 3.2
FEATURE [Part::Cylinder] Cylinder082
  Angle = 360
  AttacherType = Attacher::AttachEngine3D
  Height = 10
  Placement = pos=(118,124,75) rot=(-1,0,0;1.5708rad)
  Radius = 3.2
FEATURE [Part::Cylinder] Cylinder083
  Angle = 360
  AttacherType = Attacher::AttachEngine3D
  Height = 10
  Placement = pos=(75,124,75) rot=(-1,0,0;1.5708rad)
  Radius = 3.2
FEATURE [Part::MultiFuse] Fusion004008002002002001007002002026012053  label="Mounting Screw Holes001"
  Shapes = -> [Cylinder083,Cylinder082,Cylinder080,Cylinder081]
FEATURE [Part::FeaturePython] Slice028  # WARN: FeaturePython — macro-defined, semantics opaque (R4)
  Base = -> Box085272
  Mode = 1
  Tolerance = 0
  Tools = -> [Box085270,Fusion004008002002002001007002002026012053]
FEATURE [Part::FeaturePython] Slice024_child006  label="Slice024.006"  # WARN: FeaturePython — macro-defined, semantics opaque (R4)
  Base = -> Slice028
  FilterType = 1
  Invert = false
  OverrideMaxVal = 0
  WindowFrom = 80
  WindowTo = 100
  items = 0
FEATURE [Part::MultiFuse] Fusion004008002002002001007002002026012052
  Shapes = -> [Slice024_child006,Box085273,Box085271]
FEATURE [Part::Fillet] Fillet005011017082107
  Base = -> Fusion004008002002002001007002002026012052
  Edges = 12 edges: [Edge1 r=2,Edge4 r=2,Edge8 r=2,Edge18 r=2,Edge43 r=2,Edge46 r=2,Edge49 r=0.89,Edge50 r=2,Edge52 r=2,Edge54 r=0.89,Edge55 r=0.89,Edge56 r=0.89]
FEATURE [Part::Chamfer] Chamfer011006003017092  label="Enclosure Mount PETG fit"
  Base = -> Fillet005011017082107
  Edges = 4 edges r=1.5: [Edge26,Edge31,Edge37,Edge38]
FEATURE [Part::Chamfer] Chamfer011006003017093
  Base = -> Fusion004008002002002001007002002026012050
  Edges = 4 edges r=1.5: [Edge22,Edge23,Edge25,Edge30]
FEATURE [Part::Fillet] Fillet005011017082108  label="Enclosure Mount"
  Base = -> Chamfer011006003017093
  Edges = 8 edges r=1: [Edge55,Edge62,Edge63,Edge65,Edge66,Edge68,Edge69,Edge70]
FEATURE [Part::Box] Box085274  label="Cube356"
  AttacherType = Attacher::AttachEngine3D
  Height = 5
  Length = 198
  Placement = pos=(-5,85,-5) rot=(0,0,1;0rad)
  Width = 35
FEATURE [Part::Box] Box085275  label="Cube357"
  AttacherType = Attacher::AttachEngine3D
  Height = 100
  Length = 5
  Placement = pos=(-5,85,0) rot=(0,0,1;0rad)
  Width = 35
FEATURE [Part::Box] Box085276  label="Cube358"
  AttacherType = Attacher::AttachEngine3D
  Height = 5
  Length = 15
  Placement = pos=(-20,85,95) rot=(0,0,1;0rad)
  Width = 35
FEATURE [Part::Box] Box085277  label="Cube359"
  AttacherType = Attacher::AttachEngine3D
  Height = 15
  Length = 5
  Placement = pos=(188,85,-20) rot=(0,0,1;0rad)
  Width = 35
FEATURE [Part::Cylinder] Cylinder084
  Angle = 360
  AttacherType = Attacher::AttachEngine3D
  Height = 10
  Placement = pos=(-12.5,111,90) rot=(0,0,1;1.5708rad)
  Radius = 1.44
FEATURE [Part::Cylinder] Cylinder085
  Angle = 360
  AttacherType = Attacher::AttachEngine3D
  Height = 10
  Placement = pos=(-12.5,94,90) rot=(0,0,1;1.5708rad)
  Radius = 1.6
FEATURE [Part::Cylinder] Cylinder086
  Angle = 360
  AttacherType = Attacher::AttachEngine3D
  Height = 10
  Placement = pos=(-12.5,94,88) rot=(0,0,1;1.5708rad)
  Radius = 3.1
FEATURE [Part::Cylinder] Cylinder087
  Angle = 360
  AttacherType = Attacher::AttachEngine3D
  Height = 10
  Placement = pos=(-12.5,111,88) rot=(0,0,1;1.5708rad)
  Radius = 2.7
FEATURE [Part::MultiFuse] Fusion004008002002002001007002002026012054
  Shapes = -> [Cylinder084,Cylinder087]
FEATURE [Part::MultiFuse] Fusion004008002002002001007002002026012055
  Shapes = -> [Cylinder085,Cylinder086]
FEATURE [Part::Cylinder] Cylinder088
  Angle = 360
  AttacherType = Attacher::AttachEngine3D
  Height = 10
  Placement = pos=(183,94,-12.5) rot=(0,1,0;1.5708rad)
  Radius = 1.44
FEATURE [Part::Cylinder] Cylinder089
  Angle = 360
  AttacherType = Attacher::AttachEngine3D
  Height = 10
  Placement = pos=(183,111,-12.5) rot=(0,1,0;1.5708rad)
  Radius = 1.44
FEATURE [Part::Cylinder] Cylinder090
  Angle = 360
  AttacherType = Attacher::AttachEngine3D
  Height = 10
  Placement = pos=(181,111,-12.5) rot=(0,1,0;1.5708rad)
  Radius = 2.7
FEATURE [Part::Cylinder] Cylinder091
  Angle = 360
  AttacherType = Attacher::AttachEngine3D
  Height = 10
  Placement = pos=(181,94,-12.5) rot=(0,1,0;1.5708rad)
  Radius = 2.7
FEATURE [Part::MultiFuse] Fusion004008002002002001007002002026012056
  Shapes = -> [Cylinder088,Cylinder091]
FEATURE [Part::MultiFuse] Fusion004008002002002001007002002026012057
  Shapes = -> [Cylinder089,Cylinder090]
FEATURE [Part::MultiFuse] Fusion004008002002002001007002002026012058
  Shapes = -> [Box085274,Box085275,Box085276,Box085277]
FEATURE [Part::Box] Box085278  label="Cube360"
  AttacherType = Attacher::AttachEngine3D
  Height = 3
  Length = 10
  Placement = pos=(-17.5,90.9,95) rot=(0,0,1;0rad)
  Width = 6.2
FEATURE [Part::Box] Box085279  label="Cube361"
  AttacherType = Attacher::AttachEngine3D
  Height = 5
  Length = 7
  Placement = pos=(-16,92.4,95) rot=(0,0,1;0rad)
  Width = 3.2
FEATURE [Part::Box] Box085280  label="Cube362"
  AttacherType = Attacher::AttachEngine3D
  Height = 5
  Length = 11
  Placement = pos=(-18,88.9,95) rot=(0,0,1;0rad)
  Width = 10
FEATURE [Part::Fillet] Fillet005011017082109
  Base = -> Box085279
  Edges = 4 edges r=1.5: [Edge1,Edge3,Edge5,Edge7]
FEATURE [Part::Fillet] Fillet005011017082110
  Base = -> Box085278
  Edges = 4 edges r=3.09: [Edge1,Edge3,Edge5,Edge7]
FEATURE [Part::MultiFuse] Fusion004008002002002001007002002026012059
  Shapes = -> [Fillet005011017082109,Fillet005011017082110]
FEATURE [Part::Box] Box085281  label="Cube363"
  AttacherType = Attacher::AttachEngine3D
  Height = 5
  Length = 7
  Placement = pos=(-16,109.4,95) rot=(0,0,1;0rad)
  Width = 3.2
FEATURE [Part::Box] Box085282  label="Cube364"
  AttacherType = Attacher::AttachEngine3D
  Height = 3
  Length = 10
  Placement = pos=(-17.5,107.9,95) rot=(0,0,1;0rad)
  Width = 6.2
FEATURE [Part::Fillet] Fillet005011017082111
  Base = -> Box085281
  Edges = 4 edges r=1.5: [Edge1,Edge3,Edge5,Edge7]
FEATURE [Part::Fillet] Fillet005011017082112
  Base = -> Box085282
  Edges = 4 edges r=3.09: [Edge1,Edge3,Edge5,Edge7]
FEATURE [Part::MultiFuse] Fusion004008002002002001007002002026012060
  Shapes = -> [Fillet005011017082111,Fillet005011017082112]
FEATURE [Part::Box] Box085283  label="Cube365"
  AttacherType = Attacher::AttachEngine3D
  Height = 7
  Length = 5
  Placement = pos=(188,92.4,-16) rot=(0,0,1;0rad)
  Width = 3.2
FEATURE [Part::Box] Box085284  label="Cube366"
  AttacherType = Attacher::AttachEngine3D
  Height = 10
  Length = 3
  Placement = pos=(188,90.9,-17.5) rot=(0,0,1;0rad)
  Width = 6.2
FEATURE [Part::Fillet] Fillet005011017082113
  Base = -> Box085283
  Edges = 4 edges r=1.59: [Edge9,Edge10,Edge11,Edge12]
FEATURE [Part::Fillet] Fillet005011017082114
  Base = -> Box085284
  Edges = 4 edges r=3.09: [Edge9,Edge10,Edge11,Edge12]
FEATURE [Part::MultiFuse] Fusion004008002002002001007002002026012061
  Shapes = -> [Fillet005011017082113,Fillet005011017082114]
FEATURE [Part::Box] Box085285  label="Cube367"
  AttacherType = Attacher::AttachEngine3D
  Height = 7
  Length = 5
  Placement = pos=(188,109.4,-16) rot=(0,0,1;0rad)
  Width = 3.2
FEATURE [Part::Fillet] Fillet005011017082115
  Base = -> Box085285
  Edges = 4 edges r=1.59: [Edge9,Edge10,Edge11,Edge12]
FEATURE [Part::Box] Box085286  label="Cube368"
  AttacherType = Attacher::AttachEngine3D
  Height = 10
  Length = 3
  Placement = pos=(188,107.9,-17.5) rot=(0,0,1;0rad)
  Width = 6.2
FEATURE [Part::Fillet] Fillet005011017082116
  Base = -> Box085286
  Edges = 4 edges r=3.09: [Edge9,Edge10,Edge11,Edge12]
FEATURE [Part::MultiFuse] Fusion004008002002002001007002002026012062
  Shapes = -> [Fillet005011017082115,Fillet005011017082116]
FEATURE [Part::Fillet] Fillet005011017082117
  Base = -> Fusion004008002002002001007002002026012058
  Edges = 7 edges: [Edge4 r=4,Edge11 r=2,Edge18 r=2,Edge19 r=4,Edge34 r=4,Edge42 r=4,Edge44 r=4]
FEATURE [Part::FeaturePython] Slice029  # WARN: FeaturePython — macro-defined, semantics opaque (R4)
  Base = -> Fillet005011017082117
  Mode = 1
  Tolerance = 0
  Tools = -> [Fusion004008002002002001007002002026012059,Fusion004008002002002001007002002026012060,Fusion004008002002002001007002002026012061,Fusion004008002002002001007002002026012062]
FEATURE [Part::FeaturePython] Slice029_child0  label="Slice029.0"  # WARN: FeaturePython — macro-defined, semantics opaque (R4)
  Base = -> Slice029
  FilterType = 1
  Invert = false
  OverrideMaxVal = 0
  WindowFrom = 80
  WindowTo = 100
  items = 0
FEATURE [Part::FeaturePython] Slice029_child1  label="Slice029.1"  # WARN: FeaturePython — macro-defined, semantics opaque (R4)
  Base = -> Slice029
  FilterType = 1
  Invert = false
  OverrideMaxVal = 0
  WindowFrom = 80
  WindowTo = 100
  items = 1
FEATURE [Part::FeaturePython] Slice029_child2  label="Slice029.2"  # WARN: FeaturePython — macro-defined, semantics opaque (R4)
  Base = -> Slice029
  FilterType = 1
  Invert = false
  OverrideMaxVal = 0
  WindowFrom = 80
  WindowTo = 100
  items = 2
FEATURE [Part::FeaturePython] Slice029_child3  label="Slice029.3"  # WARN: FeaturePython — macro-defined, semantics opaque (R4)
  Base = -> Slice029
  FilterType = 1
  Invert = false
  OverrideMaxVal = 0
  WindowFrom = 80
  WindowTo = 100
  items = 3
FEATURE [Part::FeaturePython] Slice029_child4  label="Slice029.4"  # WARN: FeaturePython — macro-defined, semantics opaque (R4)
  Base = -> Slice029
  FilterType = 1
  Invert = false
  OverrideMaxVal = 0
  WindowFrom = 80
  WindowTo = 100
  items = 4
FEATURE [App::DocumentObjectGroup] GrExplode_Slice029  label="Exploded Slice029"
  Group = -> [Slice029_child0,Slice029_child1,Slice029_child2,Slice029_child3,Slice029_child4]
